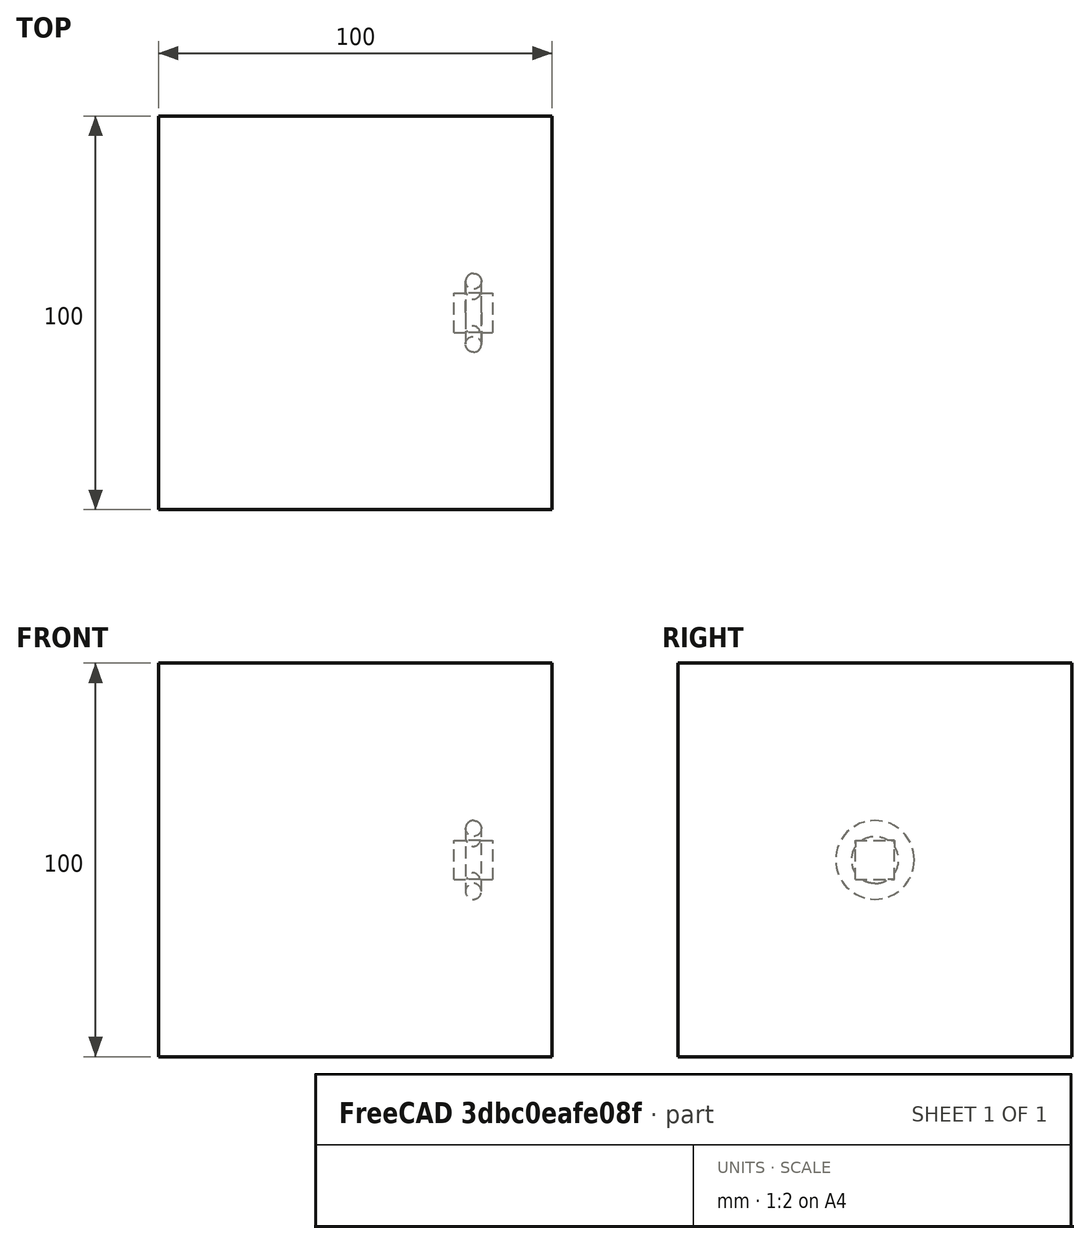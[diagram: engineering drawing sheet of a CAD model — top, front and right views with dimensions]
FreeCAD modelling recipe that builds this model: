
FCSTD DOCUMENT  (FreeCAD 0.21R33694 (Git))
Label: polarArray-7
License: All rights reserved
objects: App::DocumentObjectGroupPython×1251, Part::FeaturePython×4, App::Part×2, Part::MultiFuse×1
note: 4 computed .brp shape members not serialized (recipe doc carries the construction recipe); baked Part::Feature solids carry a one-line shape summary decoded from their .brp

FEATURE [App::DocumentObjectGroupPython] HALFPI  # scripted group (container) (typed FeaturePython)
  name = HALFPI
  value = pi/2.
FEATURE [App::DocumentObjectGroupPython] PI  # scripted group (container) (typed FeaturePython)
  name = PI
  value = 1.*pi
FEATURE [App::DocumentObjectGroupPython] TWOPI  # scripted group (container) (typed FeaturePython)
  name = TWOPI
  value = 2.*pi
FEATURE [App::DocumentObjectGroupPython] Constants  # scripted group (container) (typed FeaturePython)
  Group = -> [HALFPI,PI,TWOPI]
FEATURE [App::DocumentObjectGroupPython] Variables  # scripted group (container) (typed FeaturePython)
FEATURE [App::DocumentObjectGroupPython] Quantities  # scripted group (container) (typed FeaturePython)
FEATURE [App::DocumentObjectGroupPython] Isotopes  # scripted group (container) (typed FeaturePython)
FEATURE [App::DocumentObjectGroupPython] Elements  # scripted group (container) (typed FeaturePython)
FEATURE [App::DocumentObjectGroupPython] Matrix  # scripted group (container) (typed FeaturePython)
FEATURE [App::DocumentObjectGroupPython] Surfaces  # scripted group (container) (typed FeaturePython)
FEATURE [App::DocumentObjectGroupPython] Opticals  # scripted group (container) (typed FeaturePython)
  Group = -> [Matrix,Surfaces]
FEATURE [App::DocumentObjectGroupPython] G4Isotopes  # scripted group (container) (typed FeaturePython)
FEATURE [App::DocumentObjectGroupPython] H_element  # scripted group (container) (typed FeaturePython)
  Z = 1
  atom_value = 1.008
  formula = H
  name = H_element
FEATURE [App::DocumentObjectGroupPython] He_element  # scripted group (container) (typed FeaturePython)
  Z = 2
  atom_value = 4.0026
  formula = He
  name = He_element
FEATURE [App::DocumentObjectGroupPython] Li_element  # scripted group (container) (typed FeaturePython)
  Z = 3
  atom_value = 6.94
  formula = Li
  name = Li_element
FEATURE [App::DocumentObjectGroupPython] Be_element  # scripted group (container) (typed FeaturePython)
  Z = 4
  atom_value = 9.01218
  formula = Be
  name = Be_element
FEATURE [App::DocumentObjectGroupPython] B_element  # scripted group (container) (typed FeaturePython)
  Z = 5
  atom_value = 10.81
  formula = B
  name = B_element
FEATURE [App::DocumentObjectGroupPython] C_element  # scripted group (container) (typed FeaturePython)
  Z = 6
  atom_value = 12.011
  formula = C
  name = C_element
FEATURE [App::DocumentObjectGroupPython] N_element  # scripted group (container) (typed FeaturePython)
  Z = 7
  atom_value = 14.007
  formula = N
  name = N_element
FEATURE [App::DocumentObjectGroupPython] O_element  # scripted group (container) (typed FeaturePython)
  Z = 8
  atom_value = 15.999
  formula = O
  name = O_element
FEATURE [App::DocumentObjectGroupPython] F_element  # scripted group (container) (typed FeaturePython)
  Z = 9
  atom_value = 18.9984
  formula = F
  name = F_element
FEATURE [App::DocumentObjectGroupPython] Ne_element  # scripted group (container) (typed FeaturePython)
  Z = 10
  atom_value = 20.1797
  formula = Ne
  name = Ne_element
FEATURE [App::DocumentObjectGroupPython] Na_element  # scripted group (container) (typed FeaturePython)
  Z = 11
  atom_value = 22.9898
  formula = Na
  name = Na_element
FEATURE [App::DocumentObjectGroupPython] Mg_element  # scripted group (container) (typed FeaturePython)
  Z = 12
  atom_value = 24.305
  formula = Mg
  name = Mg_element
FEATURE [App::DocumentObjectGroupPython] Al_element  # scripted group (container) (typed FeaturePython)
  Z = 13
  atom_value = 26.9815
  formula = Al
  name = Al_element
FEATURE [App::DocumentObjectGroupPython] Si_element  # scripted group (container) (typed FeaturePython)
  Z = 14
  atom_value = 28.085
  formula = Si
  name = Si_element
FEATURE [App::DocumentObjectGroupPython] P_element  # scripted group (container) (typed FeaturePython)
  Z = 15
  atom_value = 30.9738
  formula = P
  name = P_element
FEATURE [App::DocumentObjectGroupPython] S_element  # scripted group (container) (typed FeaturePython)
  Z = 16
  atom_value = 32.06
  formula = S
  name = S_element
FEATURE [App::DocumentObjectGroupPython] Cl_element  # scripted group (container) (typed FeaturePython)
  Z = 17
  atom_value = 35.45
  formula = Cl
  name = Cl_element
FEATURE [App::DocumentObjectGroupPython] Ar_element  # scripted group (container) (typed FeaturePython)
  Z = 18
  atom_value = 39.95
  formula = Ar
  name = Ar_element
FEATURE [App::DocumentObjectGroupPython] K_element  # scripted group (container) (typed FeaturePython)
  Z = 19
  atom_value = 39.0983
  formula = K
  name = K_element
FEATURE [App::DocumentObjectGroupPython] Ca_element  # scripted group (container) (typed FeaturePython)
  Z = 20
  atom_value = 40.078
  formula = Ca
  name = Ca_element
FEATURE [App::DocumentObjectGroupPython] Sc_element  # scripted group (container) (typed FeaturePython)
  Z = 21
  atom_value = 44.9559
  formula = Sc
  name = Sc_element
FEATURE [App::DocumentObjectGroupPython] Ti_element  # scripted group (container) (typed FeaturePython)
  Z = 22
  atom_value = 47.867
  formula = Ti
  name = Ti_element
FEATURE [App::DocumentObjectGroupPython] V_element  # scripted group (container) (typed FeaturePython)
  Z = 23
  atom_value = 50.9415
  formula = V
  name = V_element
FEATURE [App::DocumentObjectGroupPython] Cr_element  # scripted group (container) (typed FeaturePython)
  Z = 24
  atom_value = 51.9961
  formula = Cr
  name = Cr_element
FEATURE [App::DocumentObjectGroupPython] Mn_element  # scripted group (container) (typed FeaturePython)
  Z = 25
  atom_value = 54.938
  formula = Mn
  name = Mn_element
FEATURE [App::DocumentObjectGroupPython] Fe_element  # scripted group (container) (typed FeaturePython)
  Z = 26
  atom_value = 55.845
  formula = Fe
  name = Fe_element
FEATURE [App::DocumentObjectGroupPython] Co_element  # scripted group (container) (typed FeaturePython)
  Z = 27
  atom_value = 58.9332
  formula = Co
  name = Co_element
FEATURE [App::DocumentObjectGroupPython] Ni_element  # scripted group (container) (typed FeaturePython)
  Z = 28
  atom_value = 58.6934
  formula = Ni
  name = Ni_element
FEATURE [App::DocumentObjectGroupPython] Cu_element  # scripted group (container) (typed FeaturePython)
  Z = 29
  atom_value = 63.546
  formula = Cu
  name = Cu_element
FEATURE [App::DocumentObjectGroupPython] Zn_element  # scripted group (container) (typed FeaturePython)
  Z = 30
  atom_value = 65.38
  formula = Zn
  name = Zn_element
FEATURE [App::DocumentObjectGroupPython] Ga_element  # scripted group (container) (typed FeaturePython)
  Z = 31
  atom_value = 69.723
  formula = Ga
  name = Ga_element
FEATURE [App::DocumentObjectGroupPython] Ge_element  # scripted group (container) (typed FeaturePython)
  Z = 32
  atom_value = 72.63
  formula = Ge
  name = Ge_element
FEATURE [App::DocumentObjectGroupPython] As_element  # scripted group (container) (typed FeaturePython)
  Z = 33
  atom_value = 74.9216
  formula = As
  name = As_element
FEATURE [App::DocumentObjectGroupPython] Se_element  # scripted group (container) (typed FeaturePython)
  Z = 34
  atom_value = 78.971
  formula = Se
  name = Se_element
FEATURE [App::DocumentObjectGroupPython] Br_element  # scripted group (container) (typed FeaturePython)
  Z = 35
  atom_value = 79.904
  formula = Br
  name = Br_element
FEATURE [App::DocumentObjectGroupPython] Kr_element  # scripted group (container) (typed FeaturePython)
  Z = 36
  atom_value = 83.798
  formula = Kr
  name = Kr_element
FEATURE [App::DocumentObjectGroupPython] Rb_element  # scripted group (container) (typed FeaturePython)
  Z = 37
  atom_value = 85.4678
  formula = Rb
  name = Rb_element
FEATURE [App::DocumentObjectGroupPython] Sr_element  # scripted group (container) (typed FeaturePython)
  Z = 38
  atom_value = 87.62
  formula = Sr
  name = Sr_element
FEATURE [App::DocumentObjectGroupPython] Y_element  # scripted group (container) (typed FeaturePython)
  Z = 39
  atom_value = 88.9058
  formula = Y
  name = Y_element
FEATURE [App::DocumentObjectGroupPython] Zr_element  # scripted group (container) (typed FeaturePython)
  Z = 40
  atom_value = 91.224
  formula = Zr
  name = Zr_element
FEATURE [App::DocumentObjectGroupPython] Nb_element  # scripted group (container) (typed FeaturePython)
  Z = 41
  atom_value = 92.9064
  formula = Nb
  name = Nb_element
FEATURE [App::DocumentObjectGroupPython] Mo_element  # scripted group (container) (typed FeaturePython)
  Z = 42
  atom_value = 95.95
  formula = Mo
  name = Mo_element
FEATURE [App::DocumentObjectGroupPython] Tc_element  # scripted group (container) (typed FeaturePython)
  Z = 43
  atom_value = 97
  formula = Tc
  name = Tc_element
FEATURE [App::DocumentObjectGroupPython] Ru_element  # scripted group (container) (typed FeaturePython)
  Z = 44
  atom_value = 101.07
  formula = Ru
  name = Ru_element
FEATURE [App::DocumentObjectGroupPython] Rh_element  # scripted group (container) (typed FeaturePython)
  Z = 45
  atom_value = 102.905
  formula = Rh
  name = Rh_element
FEATURE [App::DocumentObjectGroupPython] Pd_element  # scripted group (container) (typed FeaturePython)
  Z = 46
  atom_value = 106.42
  formula = Pd
  name = Pd_element
FEATURE [App::DocumentObjectGroupPython] Ag_element  # scripted group (container) (typed FeaturePython)
  Z = 47
  atom_value = 107.868
  formula = Ag
  name = Ag_element
FEATURE [App::DocumentObjectGroupPython] Cd_element  # scripted group (container) (typed FeaturePython)
  Z = 48
  atom_value = 112.414
  formula = Cd
  name = Cd_element
FEATURE [App::DocumentObjectGroupPython] In_element  # scripted group (container) (typed FeaturePython)
  Z = 49
  atom_value = 114.818
  formula = In
  name = In_element
FEATURE [App::DocumentObjectGroupPython] Sn_element  # scripted group (container) (typed FeaturePython)
  Z = 50
  atom_value = 118.71
  formula = Sn
  name = Sn_element
FEATURE [App::DocumentObjectGroupPython] Sb_element  # scripted group (container) (typed FeaturePython)
  Z = 51
  atom_value = 121.76
  formula = Sb
  name = Sb_element
FEATURE [App::DocumentObjectGroupPython] Te_element  # scripted group (container) (typed FeaturePython)
  Z = 52
  atom_value = 127.6
  formula = Te
  name = Te_element
FEATURE [App::DocumentObjectGroupPython] I_element  # scripted group (container) (typed FeaturePython)
  Z = 53
  atom_value = 126.904
  formula = I
  name = I_element
FEATURE [App::DocumentObjectGroupPython] Xe_element  # scripted group (container) (typed FeaturePython)
  Z = 54
  atom_value = 131.293
  formula = Xe
  name = Xe_element
FEATURE [App::DocumentObjectGroupPython] Cs_element  # scripted group (container) (typed FeaturePython)
  Z = 55
  atom_value = 132.905
  formula = Cs
  name = Cs_element
FEATURE [App::DocumentObjectGroupPython] Ba_element  # scripted group (container) (typed FeaturePython)
  Z = 56
  atom_value = 137.327
  formula = Ba
  name = Ba_element
FEATURE [App::DocumentObjectGroupPython] La_element  # scripted group (container) (typed FeaturePython)
  Z = 57
  atom_value = 138.905
  formula = La
  name = La_element
FEATURE [App::DocumentObjectGroupPython] Ce_element  # scripted group (container) (typed FeaturePython)
  Z = 58
  atom_value = 140.116
  formula = Ce
  name = Ce_element
FEATURE [App::DocumentObjectGroupPython] Pr_element  # scripted group (container) (typed FeaturePython)
  Z = 59
  atom_value = 140.908
  formula = Pr
  name = Pr_element
FEATURE [App::DocumentObjectGroupPython] Nd_element  # scripted group (container) (typed FeaturePython)
  Z = 60
  atom_value = 144.242
  formula = Nd
  name = Nd_element
FEATURE [App::DocumentObjectGroupPython] Pm_element  # scripted group (container) (typed FeaturePython)
  Z = 61
  atom_value = 145
  formula = Pm
  name = Pm_element
FEATURE [App::DocumentObjectGroupPython] Sm_element  # scripted group (container) (typed FeaturePython)
  Z = 62
  atom_value = 150.36
  formula = Sm
  name = Sm_element
FEATURE [App::DocumentObjectGroupPython] Eu_element  # scripted group (container) (typed FeaturePython)
  Z = 63
  atom_value = 151.964
  formula = Eu
  name = Eu_element
FEATURE [App::DocumentObjectGroupPython] Gd_element  # scripted group (container) (typed FeaturePython)
  Z = 64
  atom_value = 157.25
  formula = Gd
  name = Gd_element
FEATURE [App::DocumentObjectGroupPython] Tb_element  # scripted group (container) (typed FeaturePython)
  Z = 65
  atom_value = 158.925
  formula = Tb
  name = Tb_element
FEATURE [App::DocumentObjectGroupPython] Dy_element  # scripted group (container) (typed FeaturePython)
  Z = 66
  atom_value = 162.5
  formula = Dy
  name = Dy_element
FEATURE [App::DocumentObjectGroupPython] Ho_element  # scripted group (container) (typed FeaturePython)
  Z = 67
  atom_value = 164.93
  formula = Ho
  name = Ho_element
FEATURE [App::DocumentObjectGroupPython] Er_element  # scripted group (container) (typed FeaturePython)
  Z = 68
  atom_value = 167.259
  formula = Er
  name = Er_element
FEATURE [App::DocumentObjectGroupPython] Tm_element  # scripted group (container) (typed FeaturePython)
  Z = 69
  atom_value = 168.934
  formula = Tm
  name = Tm_element
FEATURE [App::DocumentObjectGroupPython] Yb_element  # scripted group (container) (typed FeaturePython)
  Z = 70
  atom_value = 173.045
  formula = Yb
  name = Yb_element
FEATURE [App::DocumentObjectGroupPython] Lu_element  # scripted group (container) (typed FeaturePython)
  Z = 71
  atom_value = 174.967
  formula = Lu
  name = Lu_element
FEATURE [App::DocumentObjectGroupPython] Hf_element  # scripted group (container) (typed FeaturePython)
  Z = 72
  atom_value = 178.49
  formula = Hf
  name = Hf_element
FEATURE [App::DocumentObjectGroupPython] Ta_element  # scripted group (container) (typed FeaturePython)
  Z = 73
  atom_value = 180.948
  formula = Ta
  name = Ta_element
FEATURE [App::DocumentObjectGroupPython] W_element  # scripted group (container) (typed FeaturePython)
  Z = 74
  atom_value = 183.84
  formula = W
  name = W_element
FEATURE [App::DocumentObjectGroupPython] Re_element  # scripted group (container) (typed FeaturePython)
  Z = 75
  atom_value = 186.207
  formula = Re
  name = Re_element
FEATURE [App::DocumentObjectGroupPython] Os_element  # scripted group (container) (typed FeaturePython)
  Z = 76
  atom_value = 190.23
  formula = Os
  name = Os_element
FEATURE [App::DocumentObjectGroupPython] Ir_element  # scripted group (container) (typed FeaturePython)
  Z = 77
  atom_value = 192.217
  formula = Ir
  name = Ir_element
FEATURE [App::DocumentObjectGroupPython] Pt_element  # scripted group (container) (typed FeaturePython)
  Z = 78
  atom_value = 195.084
  formula = Pt
  name = Pt_element
FEATURE [App::DocumentObjectGroupPython] Au_element  # scripted group (container) (typed FeaturePython)
  Z = 79
  atom_value = 196.967
  formula = Au
  name = Au_element
FEATURE [App::DocumentObjectGroupPython] Hg_element  # scripted group (container) (typed FeaturePython)
  Z = 80
  atom_value = 200.592
  formula = Hg
  name = Hg_element
FEATURE [App::DocumentObjectGroupPython] Tl_element  # scripted group (container) (typed FeaturePython)
  Z = 81
  atom_value = 204.38
  formula = Tl
  name = Tl_element
FEATURE [App::DocumentObjectGroupPython] Pb_element  # scripted group (container) (typed FeaturePython)
  Z = 82
  atom_value = 207.2
  formula = Pb
  name = Pb_element
FEATURE [App::DocumentObjectGroupPython] Bi_element  # scripted group (container) (typed FeaturePython)
  Z = 83
  atom_value = 208.98
  formula = Bi
  name = Bi_element
FEATURE [App::DocumentObjectGroupPython] Po_element  # scripted group (container) (typed FeaturePython)
  Z = 84
  atom_value = 209
  formula = Po
  name = Po_element
FEATURE [App::DocumentObjectGroupPython] At_element  # scripted group (container) (typed FeaturePython)
  Z = 85
  atom_value = 210
  formula = At
  name = At_element
FEATURE [App::DocumentObjectGroupPython] Rn_element  # scripted group (container) (typed FeaturePython)
  Z = 86
  atom_value = 222
  formula = Rn
  name = Rn_element
FEATURE [App::DocumentObjectGroupPython] Fr_element  # scripted group (container) (typed FeaturePython)
  Z = 87
  atom_value = 223
  formula = Fr
  name = Fr_element
FEATURE [App::DocumentObjectGroupPython] Ra_element  # scripted group (container) (typed FeaturePython)
  Z = 88
  atom_value = 226
  formula = Ra
  name = Ra_element
FEATURE [App::DocumentObjectGroupPython] Ac_element  # scripted group (container) (typed FeaturePython)
  Z = 89
  atom_value = 227
  formula = Ac
  name = Ac_element
FEATURE [App::DocumentObjectGroupPython] Th_element  # scripted group (container) (typed FeaturePython)
  Z = 90
  atom_value = 232.038
  formula = Th
  name = Th_element
FEATURE [App::DocumentObjectGroupPython] Pa_element  # scripted group (container) (typed FeaturePython)
  Z = 91
  atom_value = 231.036
  formula = Pa
  name = Pa_element
FEATURE [App::DocumentObjectGroupPython] U_element  # scripted group (container) (typed FeaturePython)
  Z = 92
  atom_value = 238.029
  formula = U
  name = U_element
FEATURE [App::DocumentObjectGroupPython] Np_element  # scripted group (container) (typed FeaturePython)
  Z = 93
  atom_value = 237
  formula = Np
  name = Np_element
FEATURE [App::DocumentObjectGroupPython] Pu_element  # scripted group (container) (typed FeaturePython)
  Z = 94
  atom_value = 244
  formula = Pu
  name = Pu_element
FEATURE [App::DocumentObjectGroupPython] Am_element  # scripted group (container) (typed FeaturePython)
  Z = 95
  atom_value = 243
  formula = Am
  name = Am_element
FEATURE [App::DocumentObjectGroupPython] Cm_element  # scripted group (container) (typed FeaturePython)
  Z = 96
  atom_value = 247
  formula = Cm
  name = Cm_element
FEATURE [App::DocumentObjectGroupPython] Bk_element  # scripted group (container) (typed FeaturePython)
  Z = 97
  atom_value = 247
  formula = Bk
  name = Bk_element
FEATURE [App::DocumentObjectGroupPython] Cf_element  # scripted group (container) (typed FeaturePython)
  Z = 98
  atom_value = 251
  formula = Cf
  name = Cf_element
FEATURE [App::DocumentObjectGroupPython] G4Elements  # scripted group (container) (typed FeaturePython)
  Group = -> [H_element,He_element,Li_element,Be_element,B_element,C_element,N_element,O_element,F_element,Ne_element,Na_element,Mg_element,Al_element,Si_element,P_element,S_element,Cl_element,Ar_element,K_element,Ca_element,Sc_element,Ti_element,V_element,Cr_element,Mn_element,Fe_element,Co_element,Ni_element,Cu_element,Zn_element,Ga_element,Ge_element,As_element,Se_element,Br_element,Kr_element,Rb_element,+61 more]
FEATURE [App::DocumentObjectGroupPython] H_element001  label="H_element : 0.101"  # scripted group (container) (typed FeaturePython)
  n = 0.101327
FEATURE [App::DocumentObjectGroupPython] C_element001  label="C_element : 0.775"  # scripted group (container) (typed FeaturePython)
  n = 0.7755
FEATURE [App::DocumentObjectGroupPython] N_element001  label="N_element : 0.035"  # scripted group (container) (typed FeaturePython)
  n = 0.035057
FEATURE [App::DocumentObjectGroupPython] O_element001  label="O_element : 0.052"  # scripted group (container) (typed FeaturePython)
  n = 0.0523159
FEATURE [App::DocumentObjectGroupPython] F_element001  label="F_element : 0.017"  # scripted group (container) (typed FeaturePython)
  n = 0.017422
FEATURE [App::DocumentObjectGroupPython] Ca_element001  label="Ca_element : 0.018"  # scripted group (container) (typed FeaturePython)
  n = 0.018378
FEATURE [App::DocumentObjectGroupPython] G4_A_150_TISSUE  label="G4_A-150_TISSUE"  # scripted group (container) (typed FeaturePython)
  Dunit = g/cm3
  Dvalue = 1.127
  Group = -> [H_element001,C_element001,N_element001,O_element001,F_element001,Ca_element001]
  conduct = 2
  density = 1
  expand = 3
  formula = G4_A-150_TISSUE
  name = G4_A-150_TISSUE
  specific = 4
FEATURE [App::DocumentObjectGroupPython] C_element002  label="C_element : 3"  # scripted group (container) (typed FeaturePython)
  n = 3
  ref = C_element
FEATURE [App::DocumentObjectGroupPython] H_element002  label="H_element : 6"  # scripted group (container) (typed FeaturePython)
  n = 6
  ref = H_element
FEATURE [App::DocumentObjectGroupPython] O_element002  label="O_element : 1"  # scripted group (container) (typed FeaturePython)
  n = 1
  ref = O_element
FEATURE [App::DocumentObjectGroupPython] G4_ACETONE  # scripted group (container) (typed FeaturePython)
  Dunit = g/cm3
  Dvalue = 0.7899
  Group = -> [C_element002,H_element002,O_element002]
  conduct = 2
  density = 1
  expand = 3
  formula = G4_ACETONE
  name = G4_ACETONE
  specific = 4
FEATURE [App::DocumentObjectGroupPython] C_element003  label="C_element : 2"  # scripted group (container) (typed FeaturePython)
  n = 2
  ref = C_element
FEATURE [App::DocumentObjectGroupPython] H_element003  label="H_element : 2"  # scripted group (container) (typed FeaturePython)
  n = 2
  ref = H_element
FEATURE [App::DocumentObjectGroupPython] G4_ACETYLENE  # scripted group (container) (typed FeaturePython)
  Dunit = g/cm3
  Dvalue = 0.0010967
  Group = -> [C_element003,H_element003]
  conduct = 2
  density = 1
  expand = 3
  formula = G4_ACETYLENE
  name = G4_ACETYLENE
  specific = 4
FEATURE [App::DocumentObjectGroupPython] C_element004  label="C_element : 5"  # scripted group (container) (typed FeaturePython)
  n = 5
  ref = C_element
FEATURE [App::DocumentObjectGroupPython] H_element004  label="H_element : 5"  # scripted group (container) (typed FeaturePython)
  n = 5
  ref = H_element
FEATURE [App::DocumentObjectGroupPython] N_element002  label="N_element : 5"  # scripted group (container) (typed FeaturePython)
  n = 5
  ref = N_element
FEATURE [App::DocumentObjectGroupPython] G4_ADENINE  # scripted group (container) (typed FeaturePython)
  Dunit = g/cm3
  Dvalue = 1.6
  Group = -> [C_element004,H_element004,N_element002]
  conduct = 2
  density = 1
  expand = 3
  formula = G4_ADENINE
  name = G4_ADENINE
  specific = 4
FEATURE [App::DocumentObjectGroupPython] H_element005  label="H_element : 0.114"  # scripted group (container) (typed FeaturePython)
  n = 0.114
FEATURE [App::DocumentObjectGroupPython] C_element005  label="C_element : 0.598"  # scripted group (container) (typed FeaturePython)
  n = 0.598
FEATURE [App::DocumentObjectGroupPython] N_element003  label="N_element : 0.007"  # scripted group (container) (typed FeaturePython)
  n = 0.007
FEATURE [App::DocumentObjectGroupPython] O_element003  label="O_element : 0.278"  # scripted group (container) (typed FeaturePython)
  n = 0.278
FEATURE [App::DocumentObjectGroupPython] Na_element001  label="Na_element : 0.001"  # scripted group (container) (typed FeaturePython)
  n = 0.001
FEATURE [App::DocumentObjectGroupPython] S_element001  label="S_element : 0.001"  # scripted group (container) (typed FeaturePython)
  n = 0.001
FEATURE [App::DocumentObjectGroupPython] Cl_element001  label="Cl_element : 0.001"  # scripted group (container) (typed FeaturePython)
  n = 0.001
FEATURE [App::DocumentObjectGroupPython] G4_ADIPOSE_TISSUE_ICRP  # scripted group (container) (typed FeaturePython)
  Dunit = g/cm3
  Dvalue = 0.95
  Group = -> [H_element005,C_element005,N_element003,O_element003,Na_element001,S_element001,Cl_element001]
  conduct = 2
  density = 1
  expand = 3
  formula = G4_ADIPOSE_TISSUE_ICRP
  name = G4_ADIPOSE_TISSUE_ICRP
  specific = 4
FEATURE [App::DocumentObjectGroupPython] C_element006  label="C_element : 0.000"  # scripted group (container) (typed FeaturePython)
  n = 0.000124
FEATURE [App::DocumentObjectGroupPython] N_element004  label="N_element : 0.755"  # scripted group (container) (typed FeaturePython)
  n = 0.755268
FEATURE [App::DocumentObjectGroupPython] O_element004  label="O_element : 0.232"  # scripted group (container) (typed FeaturePython)
  n = 0.231781
FEATURE [App::DocumentObjectGroupPython] Ar_element001  label="Ar_element : 0.013"  # scripted group (container) (typed FeaturePython)
  n = 0.012827
FEATURE [App::DocumentObjectGroupPython] G4_AIR  # scripted group (container) (typed FeaturePython)
  Dunit = g/cm3
  Dvalue = 0.00120479
  Group = -> [C_element006,N_element004,O_element004,Ar_element001]
  conduct = 2
  density = 1
  expand = 3
  formula = G4_AIR
  name = G4_AIR
  specific = 4
FEATURE [App::DocumentObjectGroupPython] C_element007  label="C_element : 006"  # scripted group (container) (typed FeaturePython)
  n = 3
  ref = C_element
FEATURE [App::DocumentObjectGroupPython] H_element006  label="H_element : 7"  # scripted group (container) (typed FeaturePython)
  n = 7
  ref = H_element
FEATURE [App::DocumentObjectGroupPython] N_element005  label="N_element : 1"  # scripted group (container) (typed FeaturePython)
  n = 1
  ref = N_element
FEATURE [App::DocumentObjectGroupPython] O_element005  label="O_element : 2"  # scripted group (container) (typed FeaturePython)
  n = 2
  ref = O_element
FEATURE [App::DocumentObjectGroupPython] G4_ALANINE  # scripted group (container) (typed FeaturePython)
  Dunit = g/cm3
  Dvalue = 1.42
  Group = -> [C_element007,H_element006,N_element005,O_element005]
  conduct = 2
  density = 1
  expand = 3
  formula = G4_ALANINE
  name = G4_ALANINE
  specific = 4
FEATURE [App::DocumentObjectGroupPython] Al_element001  label="Al_element : 2"  # scripted group (container) (typed FeaturePython)
  n = 2
  ref = Al_element
FEATURE [App::DocumentObjectGroupPython] O_element006  label="O_element : 3"  # scripted group (container) (typed FeaturePython)
  n = 3
  ref = O_element
FEATURE [App::DocumentObjectGroupPython] G4_ALUMINUM_OXIDE  # scripted group (container) (typed FeaturePython)
  Dunit = g/cm3
  Dvalue = 3.97
  Group = -> [Al_element001,O_element006]
  conduct = 2
  density = 1
  expand = 3
  formula = G4_ALUMINUM_OXIDE
  name = G4_ALUMINUM_OXIDE
  specific = 4
FEATURE [App::DocumentObjectGroupPython] H_element007  label="H_element : 0.106"  # scripted group (container) (typed FeaturePython)
  n = 0.10593
FEATURE [App::DocumentObjectGroupPython] C_element008  label="C_element : 0.789"  # scripted group (container) (typed FeaturePython)
  n = 0.788974
FEATURE [App::DocumentObjectGroupPython] O_element007  label="O_element : 0.105"  # scripted group (container) (typed FeaturePython)
  n = 0.105096
FEATURE [App::DocumentObjectGroupPython] G4_AMBER  # scripted group (container) (typed FeaturePython)
  Dunit = g/cm3
  Dvalue = 1.1
  Group = -> [H_element007,C_element008,O_element007]
  conduct = 2
  density = 1
  expand = 3
  formula = G4_AMBER
  name = G4_AMBER
  specific = 4
FEATURE [App::DocumentObjectGroupPython] N_element006  label="N_element : 006"  # scripted group (container) (typed FeaturePython)
  n = 1
  ref = N_element
FEATURE [App::DocumentObjectGroupPython] H_element008  label="H_element : 3"  # scripted group (container) (typed FeaturePython)
  n = 3
  ref = H_element
FEATURE [App::DocumentObjectGroupPython] G4_AMMONIA  # scripted group (container) (typed FeaturePython)
  Dunit = g/cm3
  Dvalue = 0.000826019
  Group = -> [N_element006,H_element008]
  conduct = 2
  density = 1
  expand = 3
  formula = G4_AMMONIA
  name = G4_AMMONIA
  specific = 4
FEATURE [App::DocumentObjectGroupPython] C_element009  label="C_element : 6"  # scripted group (container) (typed FeaturePython)
  n = 6
  ref = C_element
FEATURE [App::DocumentObjectGroupPython] H_element009  label="H_element : 008"  # scripted group (container) (typed FeaturePython)
  n = 7
  ref = H_element
FEATURE [App::DocumentObjectGroupPython] N_element007  label="N_element : 007"  # scripted group (container) (typed FeaturePython)
  n = 1
  ref = N_element
FEATURE [App::DocumentObjectGroupPython] G4_ANILINE  # scripted group (container) (typed FeaturePython)
  Dunit = g/cm3
  Dvalue = 1.0235
  Group = -> [C_element009,H_element009,N_element007]
  conduct = 2
  density = 1
  expand = 3
  formula = G4_ANILINE
  name = G4_ANILINE
  specific = 4
FEATURE [App::DocumentObjectGroupPython] C_element010  label="C_element : 14"  # scripted group (container) (typed FeaturePython)
  n = 14
  ref = C_element
FEATURE [App::DocumentObjectGroupPython] H_element010  label="H_element : 10"  # scripted group (container) (typed FeaturePython)
  n = 10
  ref = H_element
FEATURE [App::DocumentObjectGroupPython] G4_ANTHRACENE  # scripted group (container) (typed FeaturePython)
  Dunit = g/cm3
  Dvalue = 1.283
  Group = -> [C_element010,H_element010]
  conduct = 2
  density = 1
  expand = 3
  formula = G4_ANTHRACENE
  name = G4_ANTHRACENE
  specific = 4
FEATURE [App::DocumentObjectGroupPython] H_element011  label="H_element : 0.065"  # scripted group (container) (typed FeaturePython)
  n = 0.0654709
FEATURE [App::DocumentObjectGroupPython] C_element011  label="C_element : 0.537"  # scripted group (container) (typed FeaturePython)
  n = 0.536944
FEATURE [App::DocumentObjectGroupPython] N_element008  label="N_element : 0.021"  # scripted group (container) (typed FeaturePython)
  n = 0.0215
FEATURE [App::DocumentObjectGroupPython] O_element008  label="O_element : 0.032"  # scripted group (container) (typed FeaturePython)
  n = 0.032085
FEATURE [App::DocumentObjectGroupPython] F_element002  label="F_element : 0.167"  # scripted group (container) (typed FeaturePython)
  n = 0.167411
FEATURE [App::DocumentObjectGroupPython] Ca_element002  label="Ca_element : 0.177"  # scripted group (container) (typed FeaturePython)
  n = 0.176589
FEATURE [App::DocumentObjectGroupPython] G4_B_100_BONE  label="G4_B-100_BONE"  # scripted group (container) (typed FeaturePython)
  Dunit = g/cm3
  Dvalue = 1.45
  Group = -> [H_element011,C_element011,N_element008,O_element008,F_element002,Ca_element002]
  conduct = 2
  density = 1
  expand = 3
  formula = G4_B-100_BONE
  name = G4_B-100_BONE
  specific = 4
FEATURE [App::DocumentObjectGroupPython] H_element012  label="H_element : 0.057"  # scripted group (container) (typed FeaturePython)
  n = 0.057441
FEATURE [App::DocumentObjectGroupPython] C_element012  label="C_element : 0.790"  # scripted group (container) (typed FeaturePython)
  n = 0.774591
FEATURE [App::DocumentObjectGroupPython] O_element009  label="O_element : 0.168"  # scripted group (container) (typed FeaturePython)
  n = 0.167968
FEATURE [App::DocumentObjectGroupPython] G4_BAKELITE  # scripted group (container) (typed FeaturePython)
  Dunit = g/cm3
  Dvalue = 1.25
  Group = -> [H_element012,C_element012,O_element009]
  conduct = 2
  density = 1
  expand = 3
  formula = G4_BAKELITE
  name = G4_BAKELITE
  specific = 4
FEATURE [App::DocumentObjectGroupPython] Ba_element001  label="Ba_element : 1"  # scripted group (container) (typed FeaturePython)
  n = 1
  ref = Ba_element
FEATURE [App::DocumentObjectGroupPython] F_element003  label="F_element : 2"  # scripted group (container) (typed FeaturePython)
  n = 2
  ref = F_element
FEATURE [App::DocumentObjectGroupPython] G4_BARIUM_FLUORIDE  # scripted group (container) (typed FeaturePython)
  Dunit = g/cm3
  Dvalue = 4.89
  Group = -> [Ba_element001,F_element003]
  conduct = 2
  density = 1
  expand = 3
  formula = G4_BARIUM_FLUORIDE
  name = G4_BARIUM_FLUORIDE
  specific = 4
FEATURE [App::DocumentObjectGroupPython] Ba_element002  label="Ba_element : 002"  # scripted group (container) (typed FeaturePython)
  n = 1
  ref = Ba_element
FEATURE [App::DocumentObjectGroupPython] S_element002  label="S_element : 1"  # scripted group (container) (typed FeaturePython)
  n = 1
  ref = S_element
FEATURE [App::DocumentObjectGroupPython] O_element010  label="O_element : 4"  # scripted group (container) (typed FeaturePython)
  n = 4
  ref = O_element
FEATURE [App::DocumentObjectGroupPython] G4_BARIUM_SULFATE  # scripted group (container) (typed FeaturePython)
  Dunit = g/cm3
  Dvalue = 4.5
  Group = -> [Ba_element002,S_element002,O_element010]
  conduct = 2
  density = 1
  expand = 3
  formula = G4_BARIUM_SULFATE
  name = G4_BARIUM_SULFATE
  specific = 4
FEATURE [App::DocumentObjectGroupPython] C_element013  label="C_element : 007"  # scripted group (container) (typed FeaturePython)
  n = 6
  ref = C_element
FEATURE [App::DocumentObjectGroupPython] H_element013  label="H_element : 009"  # scripted group (container) (typed FeaturePython)
  n = 6
  ref = H_element
FEATURE [App::DocumentObjectGroupPython] G4_BENZENE  # scripted group (container) (typed FeaturePython)
  Dunit = g/cm3
  Dvalue = 0.87865
  Group = -> [C_element013,H_element013]
  conduct = 2
  density = 1
  expand = 3
  formula = G4_BENZENE
  name = G4_BENZENE
  specific = 4
FEATURE [App::DocumentObjectGroupPython] Be_element001  label="Be_element : 1"  # scripted group (container) (typed FeaturePython)
  n = 1
  ref = Be_element
FEATURE [App::DocumentObjectGroupPython] O_element011  label="O_element : 005"  # scripted group (container) (typed FeaturePython)
  n = 1
  ref = O_element
FEATURE [App::DocumentObjectGroupPython] G4_BERYLLIUM_OXIDE  # scripted group (container) (typed FeaturePython)
  Dunit = g/cm3
  Dvalue = 3.01
  Group = -> [Be_element001,O_element011]
  conduct = 2
  density = 1
  expand = 3
  formula = G4_BERYLLIUM_OXIDE
  name = G4_BERYLLIUM_OXIDE
  specific = 4
FEATURE [App::DocumentObjectGroupPython] Bi_element001  label="Bi_element : 4"  # scripted group (container) (typed FeaturePython)
  n = 4
  ref = Bi_element
FEATURE [App::DocumentObjectGroupPython] Ge_element001  label="Ge_element : 3"  # scripted group (container) (typed FeaturePython)
  n = 3
  ref = Ge_element
FEATURE [App::DocumentObjectGroupPython] O_element012  label="O_element : 12"  # scripted group (container) (typed FeaturePython)
  n = 12
  ref = O_element
FEATURE [App::DocumentObjectGroupPython] G4_BGO  # scripted group (container) (typed FeaturePython)
  Dunit = g/cm3
  Dvalue = 7.13
  Group = -> [Bi_element001,Ge_element001,O_element012]
  conduct = 2
  density = 1
  expand = 3
  formula = G4_BGO
  name = G4_BGO
  specific = 4
FEATURE [App::DocumentObjectGroupPython] H_element014  label="H_element : 0.102"  # scripted group (container) (typed FeaturePython)
  n = 0.102
FEATURE [App::DocumentObjectGroupPython] C_element014  label="C_element : 0.110"  # scripted group (container) (typed FeaturePython)
  n = 0.11
FEATURE [App::DocumentObjectGroupPython] N_element009  label="N_element : 0.033"  # scripted group (container) (typed FeaturePython)
  n = 0.033
FEATURE [App::DocumentObjectGroupPython] O_element013  label="O_element : 0.745"  # scripted group (container) (typed FeaturePython)
  n = 0.745
FEATURE [App::DocumentObjectGroupPython] Na_element002  label="Na_element : 0.002"  # scripted group (container) (typed FeaturePython)
  n = 0.001
FEATURE [App::DocumentObjectGroupPython] P_element001  label="P_element : 0.001"  # scripted group (container) (typed FeaturePython)
  n = 0.001
FEATURE [App::DocumentObjectGroupPython] S_element003  label="S_element : 0.002"  # scripted group (container) (typed FeaturePython)
  n = 0.002
FEATURE [App::DocumentObjectGroupPython] Cl_element002  label="Cl_element : 0.003"  # scripted group (container) (typed FeaturePython)
  n = 0.003
FEATURE [App::DocumentObjectGroupPython] K_element001  label="K_element : 0.002"  # scripted group (container) (typed FeaturePython)
  n = 0.002
FEATURE [App::DocumentObjectGroupPython] Fe_element001  label="Fe_element : 0.001"  # scripted group (container) (typed FeaturePython)
  n = 0.001
FEATURE [App::DocumentObjectGroupPython] G4_BLOOD_ICRP  # scripted group (container) (typed FeaturePython)
  Dunit = g/cm3
  Dvalue = 1.06
  Group = -> [H_element014,C_element014,N_element009,O_element013,Na_element002,P_element001,S_element003,Cl_element002,K_element001,Fe_element001]
  conduct = 2
  density = 1
  expand = 3
  formula = G4_BLOOD_ICRP
  name = G4_BLOOD_ICRP
  specific = 4
FEATURE [App::DocumentObjectGroupPython] H_element015  label="H_element : 0.064"  # scripted group (container) (typed FeaturePython)
  n = 0.064
FEATURE [App::DocumentObjectGroupPython] C_element015  label="C_element : 0.278"  # scripted group (container) (typed FeaturePython)
  n = 0.278
FEATURE [App::DocumentObjectGroupPython] N_element010  label="N_element : 0.027"  # scripted group (container) (typed FeaturePython)
  n = 0.027
FEATURE [App::DocumentObjectGroupPython] O_element014  label="O_element : 0.410"  # scripted group (container) (typed FeaturePython)
  n = 0.41
FEATURE [App::DocumentObjectGroupPython] Mg_element001  label="Mg_element : 0.002"  # scripted group (container) (typed FeaturePython)
  n = 0.002
FEATURE [App::DocumentObjectGroupPython] P_element002  label="P_element : 0.070"  # scripted group (container) (typed FeaturePython)
  n = 0.07
FEATURE [App::DocumentObjectGroupPython] S_element004  label="S_element : 0.003"  # scripted group (container) (typed FeaturePython)
  n = 0.002
FEATURE [App::DocumentObjectGroupPython] Ca_element003  label="Ca_element : 0.147"  # scripted group (container) (typed FeaturePython)
  n = 0.147
FEATURE [App::DocumentObjectGroupPython] G4_BONE_COMPACT_ICRU  # scripted group (container) (typed FeaturePython)
  Dunit = g/cm3
  Dvalue = 1.85
  Group = -> [H_element015,C_element015,N_element010,O_element014,Mg_element001,P_element002,S_element004,Ca_element003]
  conduct = 2
  density = 1
  expand = 3
  formula = G4_BONE_COMPACT_ICRU
  name = G4_BONE_COMPACT_ICRU
  specific = 4
FEATURE [App::DocumentObjectGroupPython] H_element016  label="H_element : 0.034"  # scripted group (container) (typed FeaturePython)
  n = 0.034
FEATURE [App::DocumentObjectGroupPython] C_element016  label="C_element : 0.155"  # scripted group (container) (typed FeaturePython)
  n = 0.155
FEATURE [App::DocumentObjectGroupPython] N_element011  label="N_element : 0.042"  # scripted group (container) (typed FeaturePython)
  n = 0.042
FEATURE [App::DocumentObjectGroupPython] O_element015  label="O_element : 0.435"  # scripted group (container) (typed FeaturePython)
  n = 0.435
FEATURE [App::DocumentObjectGroupPython] Na_element003  label="Na_element : 0.003"  # scripted group (container) (typed FeaturePython)
  n = 0.001
FEATURE [App::DocumentObjectGroupPython] Mg_element002  label="Mg_element : 0.003"  # scripted group (container) (typed FeaturePython)
  n = 0.002
FEATURE [App::DocumentObjectGroupPython] P_element003  label="P_element : 0.103"  # scripted group (container) (typed FeaturePython)
  n = 0.103
FEATURE [App::DocumentObjectGroupPython] S_element005  label="S_element : 0.004"  # scripted group (container) (typed FeaturePython)
  n = 0.003
FEATURE [App::DocumentObjectGroupPython] Ca_element004  label="Ca_element : 0.225"  # scripted group (container) (typed FeaturePython)
  n = 0.225
FEATURE [App::DocumentObjectGroupPython] G4_BONE_CORTICAL_ICRP  # scripted group (container) (typed FeaturePython)
  Dunit = g/cm3
  Dvalue = 1.92
  Group = -> [H_element016,C_element016,N_element011,O_element015,Na_element003,Mg_element002,P_element003,S_element005,Ca_element004]
  conduct = 2
  density = 1
  expand = 3
  formula = G4_BONE_CORTICAL_ICRP
  name = G4_BONE_CORTICAL_ICRP
  specific = 4
FEATURE [App::DocumentObjectGroupPython] B_element001  label="B_element : 4"  # scripted group (container) (typed FeaturePython)
  n = 4
  ref = B_element
FEATURE [App::DocumentObjectGroupPython] C_element017  label="C_element : 1"  # scripted group (container) (typed FeaturePython)
  n = 1
  ref = C_element
FEATURE [App::DocumentObjectGroupPython] G4_BORON_CARBIDE  # scripted group (container) (typed FeaturePython)
  Dunit = g/cm3
  Dvalue = 2.52
  Group = -> [B_element001,C_element017]
  conduct = 2
  density = 1
  expand = 3
  formula = G4_BORON_CARBIDE
  name = G4_BORON_CARBIDE
  specific = 4
FEATURE [App::DocumentObjectGroupPython] B_element002  label="B_element : 2"  # scripted group (container) (typed FeaturePython)
  n = 2
  ref = B_element
FEATURE [App::DocumentObjectGroupPython] O_element016  label="O_element : 006"  # scripted group (container) (typed FeaturePython)
  n = 3
  ref = O_element
FEATURE [App::DocumentObjectGroupPython] G4_BORON_OXIDE  # scripted group (container) (typed FeaturePython)
  Dunit = g/cm3
  Dvalue = 1.812
  Group = -> [B_element002,O_element016]
  conduct = 2
  density = 1
  expand = 3
  formula = G4_BORON_OXIDE
  name = G4_BORON_OXIDE
  specific = 4
FEATURE [App::DocumentObjectGroupPython] H_element017  label="H_element : 0.107"  # scripted group (container) (typed FeaturePython)
  n = 0.107
FEATURE [App::DocumentObjectGroupPython] C_element018  label="C_element : 0.145"  # scripted group (container) (typed FeaturePython)
  n = 0.145
FEATURE [App::DocumentObjectGroupPython] N_element012  label="N_element : 0.022"  # scripted group (container) (typed FeaturePython)
  n = 0.022
FEATURE [App::DocumentObjectGroupPython] O_element017  label="O_element : 0.712"  # scripted group (container) (typed FeaturePython)
  n = 0.712
FEATURE [App::DocumentObjectGroupPython] Na_element004  label="Na_element : 0.004"  # scripted group (container) (typed FeaturePython)
  n = 0.002
FEATURE [App::DocumentObjectGroupPython] P_element004  label="P_element : 0.004"  # scripted group (container) (typed FeaturePython)
  n = 0.004
FEATURE [App::DocumentObjectGroupPython] S_element006  label="S_element : 0.005"  # scripted group (container) (typed FeaturePython)
  n = 0.002
FEATURE [App::DocumentObjectGroupPython] Cl_element003  label="Cl_element : 0.004"  # scripted group (container) (typed FeaturePython)
  n = 0.003
FEATURE [App::DocumentObjectGroupPython] K_element002  label="K_element : 0.003"  # scripted group (container) (typed FeaturePython)
  n = 0.003
FEATURE [App::DocumentObjectGroupPython] G4_BRAIN_ICRP  # scripted group (container) (typed FeaturePython)
  Dunit = g/cm3
  Dvalue = 1.04
  Group = -> [H_element017,C_element018,N_element012,O_element017,Na_element004,P_element004,S_element006,Cl_element003,K_element002]
  conduct = 2
  density = 1
  expand = 3
  formula = G4_BRAIN_ICRP
  name = G4_BRAIN_ICRP
  specific = 4
FEATURE [App::DocumentObjectGroupPython] C_element019  label="C_element : 4"  # scripted group (container) (typed FeaturePython)
  n = 4
  ref = C_element
FEATURE [App::DocumentObjectGroupPython] H_element018  label="H_element : 010"  # scripted group (container) (typed FeaturePython)
  n = 10
  ref = H_element
FEATURE [App::DocumentObjectGroupPython] G4_BUTANE  # scripted group (container) (typed FeaturePython)
  Dunit = g/cm3
  Dvalue = 0.00249343
  Group = -> [C_element019,H_element018]
  conduct = 2
  density = 1
  expand = 3
  formula = G4_BUTANE
  name = G4_BUTANE
  specific = 4
FEATURE [App::DocumentObjectGroupPython] C_element020  label="C_element : 008"  # scripted group (container) (typed FeaturePython)
  n = 4
  ref = C_element
FEATURE [App::DocumentObjectGroupPython] H_element019  label="H_element : 011"  # scripted group (container) (typed FeaturePython)
  n = 10
  ref = H_element
FEATURE [App::DocumentObjectGroupPython] O_element018  label="O_element : 007"  # scripted group (container) (typed FeaturePython)
  n = 1
  ref = O_element
FEATURE [App::DocumentObjectGroupPython] G4_N_BUTYL_ALCOHOL  label="G4_N-BUTYL_ALCOHOL"  # scripted group (container) (typed FeaturePython)
  Dunit = g/cm3
  Dvalue = 0.8098
  Group = -> [C_element020,H_element019,O_element018]
  conduct = 2
  density = 1
  expand = 3
  formula = G4_N-BUTYL_ALCOHOL
  name = G4_N-BUTYL_ALCOHOL
  specific = 4
FEATURE [App::DocumentObjectGroupPython] H_element020  label="H_element : 0.025"  # scripted group (container) (typed FeaturePython)
  n = 0.02468
FEATURE [App::DocumentObjectGroupPython] C_element021  label="C_element : 0.502"  # scripted group (container) (typed FeaturePython)
  n = 0.501611
FEATURE [App::DocumentObjectGroupPython] O_element019  label="O_element : 0.005"  # scripted group (container) (typed FeaturePython)
  n = 0.004527
FEATURE [App::DocumentObjectGroupPython] F_element004  label="F_element : 0.465"  # scripted group (container) (typed FeaturePython)
  n = 0.465209
FEATURE [App::DocumentObjectGroupPython] Si_element001  label="Si_element : 0.004"  # scripted group (container) (typed FeaturePython)
  n = 0.003973
FEATURE [App::DocumentObjectGroupPython] G4_C_552  label="G4_C-552"  # scripted group (container) (typed FeaturePython)
  Dunit = g/cm3
  Dvalue = 1.76
  Group = -> [H_element020,C_element021,O_element019,F_element004,Si_element001]
  conduct = 2
  density = 1
  expand = 3
  formula = G4_C-552
  name = G4_C-552
  specific = 4
FEATURE [App::DocumentObjectGroupPython] Cd_element001  label="Cd_element : 1"  # scripted group (container) (typed FeaturePython)
  n = 1
  ref = Cd_element
FEATURE [App::DocumentObjectGroupPython] Te_element001  label="Te_element : 1"  # scripted group (container) (typed FeaturePython)
  n = 1
  ref = Te_element
FEATURE [App::DocumentObjectGroupPython] G4_CADMIUM_TELLURIDE  # scripted group (container) (typed FeaturePython)
  Dunit = g/cm3
  Dvalue = 6.2
  Group = -> [Cd_element001,Te_element001]
  conduct = 2
  density = 1
  expand = 3
  formula = G4_CADMIUM_TELLURIDE
  name = G4_CADMIUM_TELLURIDE
  specific = 4
FEATURE [App::DocumentObjectGroupPython] Cd_element002  label="Cd_element : 002"  # scripted group (container) (typed FeaturePython)
  n = 1
  ref = Cd_element
FEATURE [App::DocumentObjectGroupPython] W_element001  label="W_element : 1"  # scripted group (container) (typed FeaturePython)
  n = 1
  ref = W_element
FEATURE [App::DocumentObjectGroupPython] O_element020  label="O_element : 008"  # scripted group (container) (typed FeaturePython)
  n = 4
  ref = O_element
FEATURE [App::DocumentObjectGroupPython] G4_CADMIUM_TUNGSTATE  # scripted group (container) (typed FeaturePython)
  Dunit = g/cm3
  Dvalue = 7.9
  Group = -> [Cd_element002,W_element001,O_element020]
  conduct = 2
  density = 1
  expand = 3
  formula = G4_CADMIUM_TUNGSTATE
  name = G4_CADMIUM_TUNGSTATE
  specific = 4
FEATURE [App::DocumentObjectGroupPython] Ca_element005  label="Ca_element : 1"  # scripted group (container) (typed FeaturePython)
  n = 1
  ref = Ca_element
FEATURE [App::DocumentObjectGroupPython] C_element022  label="C_element : 009"  # scripted group (container) (typed FeaturePython)
  n = 1
  ref = C_element
FEATURE [App::DocumentObjectGroupPython] O_element021  label="O_element : 009"  # scripted group (container) (typed FeaturePython)
  n = 3
  ref = O_element
FEATURE [App::DocumentObjectGroupPython] G4_CALCIUM_CARBONATE  # scripted group (container) (typed FeaturePython)
  Dunit = g/cm3
  Dvalue = 2.8
  Group = -> [Ca_element005,C_element022,O_element021]
  conduct = 2
  density = 1
  expand = 3
  formula = G4_CALCIUM_CARBONATE
  name = G4_CALCIUM_CARBONATE
  specific = 4
FEATURE [App::DocumentObjectGroupPython] Ca_element006  label="Ca_element : 002"  # scripted group (container) (typed FeaturePython)
  n = 1
  ref = Ca_element
FEATURE [App::DocumentObjectGroupPython] F_element005  label="F_element : 003"  # scripted group (container) (typed FeaturePython)
  n = 2
  ref = F_element
FEATURE [App::DocumentObjectGroupPython] G4_CALCIUM_FLUORIDE  # scripted group (container) (typed FeaturePython)
  Dunit = g/cm3
  Dvalue = 3.18
  Group = -> [Ca_element006,F_element005]
  conduct = 2
  density = 1
  expand = 3
  formula = G4_CALCIUM_FLUORIDE
  name = G4_CALCIUM_FLUORIDE
  specific = 4
FEATURE [App::DocumentObjectGroupPython] Ca_element007  label="Ca_element : 003"  # scripted group (container) (typed FeaturePython)
  n = 1
  ref = Ca_element
FEATURE [App::DocumentObjectGroupPython] O_element022  label="O_element : 010"  # scripted group (container) (typed FeaturePython)
  n = 1
  ref = O_element
FEATURE [App::DocumentObjectGroupPython] G4_CALCIUM_OXIDE  # scripted group (container) (typed FeaturePython)
  Dunit = g/cm3
  Dvalue = 3.3
  Group = -> [Ca_element007,O_element022]
  conduct = 2
  density = 1
  expand = 3
  formula = G4_CALCIUM_OXIDE
  name = G4_CALCIUM_OXIDE
  specific = 4
FEATURE [App::DocumentObjectGroupPython] Ca_element008  label="Ca_element : 004"  # scripted group (container) (typed FeaturePython)
  n = 1
  ref = Ca_element
FEATURE [App::DocumentObjectGroupPython] S_element007  label="S_element : 002"  # scripted group (container) (typed FeaturePython)
  n = 1
  ref = S_element
FEATURE [App::DocumentObjectGroupPython] O_element023  label="O_element : 011"  # scripted group (container) (typed FeaturePython)
  n = 4
  ref = O_element
FEATURE [App::DocumentObjectGroupPython] G4_CALCIUM_SULFATE  # scripted group (container) (typed FeaturePython)
  Dunit = g/cm3
  Dvalue = 2.96
  Group = -> [Ca_element008,S_element007,O_element023]
  conduct = 2
  density = 1
  expand = 3
  formula = G4_CALCIUM_SULFATE
  name = G4_CALCIUM_SULFATE
  specific = 4
FEATURE [App::DocumentObjectGroupPython] Ca_element009  label="Ca_element : 005"  # scripted group (container) (typed FeaturePython)
  n = 1
  ref = Ca_element
FEATURE [App::DocumentObjectGroupPython] W_element002  label="W_element : 002"  # scripted group (container) (typed FeaturePython)
  n = 1
  ref = W_element
FEATURE [App::DocumentObjectGroupPython] O_element024  label="O_element : 012"  # scripted group (container) (typed FeaturePython)
  n = 4
  ref = O_element
FEATURE [App::DocumentObjectGroupPython] G4_CALCIUM_TUNGSTATE  # scripted group (container) (typed FeaturePython)
  Dunit = g/cm3
  Dvalue = 6.062
  Group = -> [Ca_element009,W_element002,O_element024]
  conduct = 2
  density = 1
  expand = 3
  formula = G4_CALCIUM_TUNGSTATE
  name = G4_CALCIUM_TUNGSTATE
  specific = 4
FEATURE [App::DocumentObjectGroupPython] C_element023  label="C_element : 010"  # scripted group (container) (typed FeaturePython)
  n = 1
  ref = C_element
FEATURE [App::DocumentObjectGroupPython] O_element025  label="O_element : 013"  # scripted group (container) (typed FeaturePython)
  n = 2
  ref = O_element
FEATURE [App::DocumentObjectGroupPython] G4_CARBON_DIOXIDE  # scripted group (container) (typed FeaturePython)
  Dunit = g/cm3
  Dvalue = 0.00184212
  Group = -> [C_element023,O_element025]
  conduct = 2
  density = 1
  expand = 3
  formula = G4_CARBON_DIOXIDE
  name = G4_CARBON_DIOXIDE
  specific = 4
FEATURE [App::DocumentObjectGroupPython] C_element024  label="C_element : 011"  # scripted group (container) (typed FeaturePython)
  n = 1
  ref = C_element
FEATURE [App::DocumentObjectGroupPython] Cl_element004  label="Cl_element : 4"  # scripted group (container) (typed FeaturePython)
  n = 4
  ref = Cl_element
FEATURE [App::DocumentObjectGroupPython] G4_CARBON_TETRACHLORIDE  # scripted group (container) (typed FeaturePython)
  Dunit = g/cm3
  Dvalue = 1.594
  Group = -> [C_element024,Cl_element004]
  conduct = 2
  density = 1
  expand = 3
  formula = G4_CARBON_TETRACHLORIDE
  name = G4_CARBON_TETRACHLORIDE
  specific = 4
FEATURE [App::DocumentObjectGroupPython] C_element025  label="C_element : 012"  # scripted group (container) (typed FeaturePython)
  n = 6
  ref = C_element
FEATURE [App::DocumentObjectGroupPython] H_element021  label="H_element : 012"  # scripted group (container) (typed FeaturePython)
  n = 10
  ref = H_element
FEATURE [App::DocumentObjectGroupPython] O_element026  label="O_element : 5"  # scripted group (container) (typed FeaturePython)
  n = 5
  ref = O_element
FEATURE [App::DocumentObjectGroupPython] G4_CELLULOSE_CELLOPHANE  # scripted group (container) (typed FeaturePython)
  Dunit = g/cm3
  Dvalue = 1.42
  Group = -> [C_element025,H_element021,O_element026]
  conduct = 2
  density = 1
  expand = 3
  formula = G4_CELLULOSE_CELLOPHANE
  name = G4_CELLULOSE_CELLOPHANE
  specific = 4
FEATURE [App::DocumentObjectGroupPython] H_element022  label="H_element : 0.067"  # scripted group (container) (typed FeaturePython)
  n = 0.067125
FEATURE [App::DocumentObjectGroupPython] C_element026  label="C_element : 0.545"  # scripted group (container) (typed FeaturePython)
  n = 0.545403
FEATURE [App::DocumentObjectGroupPython] O_element027  label="O_element : 0.387"  # scripted group (container) (typed FeaturePython)
  n = 0.387472
FEATURE [App::DocumentObjectGroupPython] G4_CELLULOSE_BUTYRATE  # scripted group (container) (typed FeaturePython)
  Dunit = g/cm3
  Dvalue = 1.2
  Group = -> [H_element022,C_element026,O_element027]
  conduct = 2
  density = 1
  expand = 3
  formula = G4_CELLULOSE_BUTYRATE
  name = G4_CELLULOSE_BUTYRATE
  specific = 4
FEATURE [App::DocumentObjectGroupPython] H_element023  label="H_element : 0.029"  # scripted group (container) (typed FeaturePython)
  n = 0.029216
FEATURE [App::DocumentObjectGroupPython] C_element027  label="C_element : 0.271"  # scripted group (container) (typed FeaturePython)
  n = 0.271296
FEATURE [App::DocumentObjectGroupPython] N_element013  label="N_element : 0.121"  # scripted group (container) (typed FeaturePython)
  n = 0.121276
FEATURE [App::DocumentObjectGroupPython] O_element028  label="O_element : 0.578"  # scripted group (container) (typed FeaturePython)
  n = 0.578212
FEATURE [App::DocumentObjectGroupPython] G4_CELLULOSE_NITRATE  # scripted group (container) (typed FeaturePython)
  Dunit = g/cm3
  Dvalue = 1.49
  Group = -> [H_element023,C_element027,N_element013,O_element028]
  conduct = 2
  density = 1
  expand = 3
  formula = G4_CELLULOSE_NITRATE
  name = G4_CELLULOSE_NITRATE
  specific = 4
FEATURE [App::DocumentObjectGroupPython] H_element024  label="H_element : 0.108"  # scripted group (container) (typed FeaturePython)
  n = 0.107596
FEATURE [App::DocumentObjectGroupPython] N_element014  label="N_element : 0.001"  # scripted group (container) (typed FeaturePython)
  n = 0.0008
FEATURE [App::DocumentObjectGroupPython] O_element029  label="O_element : 0.875"  # scripted group (container) (typed FeaturePython)
  n = 0.874976
FEATURE [App::DocumentObjectGroupPython] S_element008  label="S_element : 0.015"  # scripted group (container) (typed FeaturePython)
  n = 0.014627
FEATURE [App::DocumentObjectGroupPython] Ce_element001  label="Ce_element : 0.002"  # scripted group (container) (typed FeaturePython)
  n = 0.002001
FEATURE [App::DocumentObjectGroupPython] G4_CERIC_SULFATE  # scripted group (container) (typed FeaturePython)
  Dunit = g/cm3
  Dvalue = 1.03
  Group = -> [H_element024,N_element014,O_element029,S_element008,Ce_element001]
  conduct = 2
  density = 1
  expand = 3
  formula = G4_CERIC_SULFATE
  name = G4_CERIC_SULFATE
  specific = 4
FEATURE [App::DocumentObjectGroupPython] Cs_element001  label="Cs_element : 1"  # scripted group (container) (typed FeaturePython)
  n = 1
  ref = Cs_element
FEATURE [App::DocumentObjectGroupPython] F_element006  label="F_element : 1"  # scripted group (container) (typed FeaturePython)
  n = 1
  ref = F_element
FEATURE [App::DocumentObjectGroupPython] G4_CESIUM_FLUORIDE  # scripted group (container) (typed FeaturePython)
  Dunit = g/cm3
  Dvalue = 4.115
  Group = -> [Cs_element001,F_element006]
  conduct = 2
  density = 1
  expand = 3
  formula = G4_CESIUM_FLUORIDE
  name = G4_CESIUM_FLUORIDE
  specific = 4
FEATURE [App::DocumentObjectGroupPython] Cs_element002  label="Cs_element : 002"  # scripted group (container) (typed FeaturePython)
  n = 1
  ref = Cs_element
FEATURE [App::DocumentObjectGroupPython] I_element001  label="I_element : 1"  # scripted group (container) (typed FeaturePython)
  n = 1
  ref = I_element
FEATURE [App::DocumentObjectGroupPython] G4_CESIUM_IODIDE  # scripted group (container) (typed FeaturePython)
  Dunit = g/cm3
  Dvalue = 4.51
  Group = -> [Cs_element002,I_element001]
  conduct = 2
  density = 1
  expand = 3
  formula = G4_CESIUM_IODIDE
  name = G4_CESIUM_IODIDE
  specific = 4
FEATURE [App::DocumentObjectGroupPython] C_element028  label="C_element : 013"  # scripted group (container) (typed FeaturePython)
  n = 6
  ref = C_element
FEATURE [App::DocumentObjectGroupPython] H_element025  label="H_element : 013"  # scripted group (container) (typed FeaturePython)
  n = 5
  ref = H_element
FEATURE [App::DocumentObjectGroupPython] Cl_element005  label="Cl_element : 1"  # scripted group (container) (typed FeaturePython)
  n = 1
  ref = Cl_element
FEATURE [App::DocumentObjectGroupPython] G4_CHLOROBENZENE  # scripted group (container) (typed FeaturePython)
  Dunit = g/cm3
  Dvalue = 1.1058
  Group = -> [C_element028,H_element025,Cl_element005]
  conduct = 2
  density = 1
  expand = 3
  formula = G4_CHLOROBENZENE
  name = G4_CHLOROBENZENE
  specific = 4
FEATURE [App::DocumentObjectGroupPython] C_element029  label="C_element : 014"  # scripted group (container) (typed FeaturePython)
  n = 1
  ref = C_element
FEATURE [App::DocumentObjectGroupPython] H_element026  label="H_element : 1"  # scripted group (container) (typed FeaturePython)
  n = 1
  ref = H_element
FEATURE [App::DocumentObjectGroupPython] Cl_element006  label="Cl_element : 3"  # scripted group (container) (typed FeaturePython)
  n = 3
  ref = Cl_element
FEATURE [App::DocumentObjectGroupPython] G4_CHLOROFORM  # scripted group (container) (typed FeaturePython)
  Dunit = g/cm3
  Dvalue = 1.4832
  Group = -> [C_element029,H_element026,Cl_element006]
  conduct = 2
  density = 1
  expand = 3
  formula = G4_CHLOROFORM
  name = G4_CHLOROFORM
  specific = 4
FEATURE [App::DocumentObjectGroupPython] H_element027  label="H_element : 0.010"  # scripted group (container) (typed FeaturePython)
  n = 0.01
FEATURE [App::DocumentObjectGroupPython] C_element030  label="C_element : 0.001"  # scripted group (container) (typed FeaturePython)
  n = 0.001
FEATURE [App::DocumentObjectGroupPython] O_element030  label="O_element : 0.529"  # scripted group (container) (typed FeaturePython)
  n = 0.529107
FEATURE [App::DocumentObjectGroupPython] Na_element005  label="Na_element : 0.016"  # scripted group (container) (typed FeaturePython)
  n = 0.016
FEATURE [App::DocumentObjectGroupPython] Mg_element003  label="Mg_element : 0.004"  # scripted group (container) (typed FeaturePython)
  n = 0.002
FEATURE [App::DocumentObjectGroupPython] Al_element002  label="Al_element : 0.034"  # scripted group (container) (typed FeaturePython)
  n = 0.033872
FEATURE [App::DocumentObjectGroupPython] Si_element002  label="Si_element : 0.337"  # scripted group (container) (typed FeaturePython)
  n = 0.337021
FEATURE [App::DocumentObjectGroupPython] K_element003  label="K_element : 0.013"  # scripted group (container) (typed FeaturePython)
  n = 0.013
FEATURE [App::DocumentObjectGroupPython] Ca_element010  label="Ca_element : 0.044"  # scripted group (container) (typed FeaturePython)
  n = 0.044
FEATURE [App::DocumentObjectGroupPython] Fe_element002  label="Fe_element : 0.014"  # scripted group (container) (typed FeaturePython)
  n = 0.014
FEATURE [App::DocumentObjectGroupPython] G4_CONCRETE  # scripted group (container) (typed FeaturePython)
  Dunit = g/cm3
  Dvalue = 2.3
  Group = -> [H_element027,C_element030,O_element030,Na_element005,Mg_element003,Al_element002,Si_element002,K_element003,Ca_element010,Fe_element002]
  conduct = 2
  density = 1
  expand = 3
  formula = G4_CONCRETE
  name = G4_CONCRETE
  specific = 4
FEATURE [App::DocumentObjectGroupPython] C_element031  label="C_element : 015"  # scripted group (container) (typed FeaturePython)
  n = 6
  ref = C_element
FEATURE [App::DocumentObjectGroupPython] H_element028  label="H_element : 12"  # scripted group (container) (typed FeaturePython)
  n = 12
  ref = H_element
FEATURE [App::DocumentObjectGroupPython] G4_CYCLOHEXANE  # scripted group (container) (typed FeaturePython)
  Dunit = g/cm3
  Dvalue = 0.779
  Group = -> [C_element031,H_element028]
  conduct = 2
  density = 1
  expand = 3
  formula = G4_CYCLOHEXANE
  name = G4_CYCLOHEXANE
  specific = 4
FEATURE [App::DocumentObjectGroupPython] C_element032  label="C_element : 016"  # scripted group (container) (typed FeaturePython)
  n = 6
  ref = C_element
FEATURE [App::DocumentObjectGroupPython] H_element029  label="H_element : 4"  # scripted group (container) (typed FeaturePython)
  n = 4
  ref = H_element
FEATURE [App::DocumentObjectGroupPython] Cl_element007  label="Cl_element : 2"  # scripted group (container) (typed FeaturePython)
  n = 2
  ref = Cl_element
FEATURE [App::DocumentObjectGroupPython] G4_1_2_DICHLOROBENZENE  label="G4_1.2-DICHLOROBENZENE"  # scripted group (container) (typed FeaturePython)
  Dunit = g/cm3
  Dvalue = 1.3048
  Group = -> [C_element032,H_element029,Cl_element007]
  conduct = 2
  density = 1
  expand = 3
  formula = G4_1.2-DICHLOROBENZENE
  name = G4_1.2-DICHLOROBENZENE
  specific = 4
FEATURE [App::DocumentObjectGroupPython] C_element033  label="C_element : 017"  # scripted group (container) (typed FeaturePython)
  n = 4
  ref = C_element
FEATURE [App::DocumentObjectGroupPython] H_element030  label="H_element : 8"  # scripted group (container) (typed FeaturePython)
  n = 8
  ref = H_element
FEATURE [App::DocumentObjectGroupPython] O_element031  label="O_element : 014"  # scripted group (container) (typed FeaturePython)
  n = 1
  ref = O_element
FEATURE [App::DocumentObjectGroupPython] Cl_element008  label="Cl_element : 005"  # scripted group (container) (typed FeaturePython)
  n = 2
  ref = Cl_element
FEATURE [App::DocumentObjectGroupPython] G4_DICHLORODIETHYL_ETHER  # scripted group (container) (typed FeaturePython)
  Dunit = g/cm3
  Dvalue = 1.2199
  Group = -> [C_element033,H_element030,O_element031,Cl_element008]
  conduct = 2
  density = 1
  expand = 3
  formula = G4_DICHLORODIETHYL_ETHER
  name = G4_DICHLORODIETHYL_ETHER
  specific = 4
FEATURE [App::DocumentObjectGroupPython] C_element034  label="C_element : 018"  # scripted group (container) (typed FeaturePython)
  n = 2
  ref = C_element
FEATURE [App::DocumentObjectGroupPython] H_element031  label="H_element : 014"  # scripted group (container) (typed FeaturePython)
  n = 4
  ref = H_element
FEATURE [App::DocumentObjectGroupPython] Cl_element009  label="Cl_element : 006"  # scripted group (container) (typed FeaturePython)
  n = 2
  ref = Cl_element
FEATURE [App::DocumentObjectGroupPython] G4_1_2_DICHLOROETHANE  label="G4_1.2-DICHLOROETHANE"  # scripted group (container) (typed FeaturePython)
  Dunit = g/cm3
  Dvalue = 1.2351
  Group = -> [C_element034,H_element031,Cl_element009]
  conduct = 2
  density = 1
  expand = 3
  formula = G4_1.2-DICHLOROETHANE
  name = G4_1.2-DICHLOROETHANE
  specific = 4
FEATURE [App::DocumentObjectGroupPython] C_element035  label="C_element : 019"  # scripted group (container) (typed FeaturePython)
  n = 4
  ref = C_element
FEATURE [App::DocumentObjectGroupPython] H_element032  label="H_element : 015"  # scripted group (container) (typed FeaturePython)
  n = 10
  ref = H_element
FEATURE [App::DocumentObjectGroupPython] O_element032  label="O_element : 015"  # scripted group (container) (typed FeaturePython)
  n = 1
  ref = O_element
FEATURE [App::DocumentObjectGroupPython] G4_DIETHYL_ETHER  # scripted group (container) (typed FeaturePython)
  Dunit = g/cm3
  Dvalue = 0.71378
  Group = -> [C_element035,H_element032,O_element032]
  conduct = 2
  density = 1
  expand = 3
  formula = G4_DIETHYL_ETHER
  name = G4_DIETHYL_ETHER
  specific = 4
FEATURE [App::DocumentObjectGroupPython] C_element036  label="C_element : 020"  # scripted group (container) (typed FeaturePython)
  n = 3
  ref = C_element
FEATURE [App::DocumentObjectGroupPython] H_element033  label="H_element : 016"  # scripted group (container) (typed FeaturePython)
  n = 7
  ref = H_element
FEATURE [App::DocumentObjectGroupPython] N_element015  label="N_element : 008"  # scripted group (container) (typed FeaturePython)
  n = 1
  ref = N_element
FEATURE [App::DocumentObjectGroupPython] O_element033  label="O_element : 016"  # scripted group (container) (typed FeaturePython)
  n = 1
  ref = O_element
FEATURE [App::DocumentObjectGroupPython] G4_N_N_DIMETHYL_FORMAMIDE  label="G4_N.N-DIMETHYL_FORMAMIDE"  # scripted group (container) (typed FeaturePython)
  Dunit = g/cm3
  Dvalue = 0.9487
  Group = -> [C_element036,H_element033,N_element015,O_element033]
  conduct = 2
  density = 1
  expand = 3
  formula = G4_N.N-DIMETHYL_FORMAMIDE
  name = G4_N.N-DIMETHYL_FORMAMIDE
  specific = 4
FEATURE [App::DocumentObjectGroupPython] C_element037  label="C_element : 021"  # scripted group (container) (typed FeaturePython)
  n = 2
  ref = C_element
FEATURE [App::DocumentObjectGroupPython] H_element034  label="H_element : 017"  # scripted group (container) (typed FeaturePython)
  n = 6
  ref = H_element
FEATURE [App::DocumentObjectGroupPython] O_element034  label="O_element : 017"  # scripted group (container) (typed FeaturePython)
  n = 1
  ref = O_element
FEATURE [App::DocumentObjectGroupPython] S_element009  label="S_element : 003"  # scripted group (container) (typed FeaturePython)
  n = 1
  ref = S_element
FEATURE [App::DocumentObjectGroupPython] G4_DIMETHYL_SULFOXIDE  # scripted group (container) (typed FeaturePython)
  Dunit = g/cm3
  Dvalue = 1.1014
  Group = -> [C_element037,H_element034,O_element034,S_element009]
  conduct = 2
  density = 1
  expand = 3
  formula = G4_DIMETHYL_SULFOXIDE
  name = G4_DIMETHYL_SULFOXIDE
  specific = 4
FEATURE [App::DocumentObjectGroupPython] C_element038  label="C_element : 022"  # scripted group (container) (typed FeaturePython)
  n = 2
  ref = C_element
FEATURE [App::DocumentObjectGroupPython] H_element035  label="H_element : 018"  # scripted group (container) (typed FeaturePython)
  n = 6
  ref = H_element
FEATURE [App::DocumentObjectGroupPython] G4_ETHANE  # scripted group (container) (typed FeaturePython)
  Dunit = g/cm3
  Dvalue = 0.00125324
  Group = -> [C_element038,H_element035]
  conduct = 2
  density = 1
  expand = 3
  formula = G4_ETHANE
  name = G4_ETHANE
  specific = 4
FEATURE [App::DocumentObjectGroupPython] C_element039  label="C_element : 023"  # scripted group (container) (typed FeaturePython)
  n = 2
  ref = C_element
FEATURE [App::DocumentObjectGroupPython] H_element036  label="H_element : 019"  # scripted group (container) (typed FeaturePython)
  n = 6
  ref = H_element
FEATURE [App::DocumentObjectGroupPython] O_element035  label="O_element : 018"  # scripted group (container) (typed FeaturePython)
  n = 1
  ref = O_element
FEATURE [App::DocumentObjectGroupPython] G4_ETHYL_ALCOHOL  # scripted group (container) (typed FeaturePython)
  Dunit = g/cm3
  Dvalue = 0.7893
  Group = -> [C_element039,H_element036,O_element035]
  conduct = 2
  density = 1
  expand = 3
  formula = G4_ETHYL_ALCOHOL
  name = G4_ETHYL_ALCOHOL
  specific = 4
FEATURE [App::DocumentObjectGroupPython] H_element037  label="H_element : 0.090"  # scripted group (container) (typed FeaturePython)
  n = 0.090027
FEATURE [App::DocumentObjectGroupPython] C_element040  label="C_element : 0.585"  # scripted group (container) (typed FeaturePython)
  n = 0.585182
FEATURE [App::DocumentObjectGroupPython] O_element036  label="O_element : 0.325"  # scripted group (container) (typed FeaturePython)
  n = 0.324791
FEATURE [App::DocumentObjectGroupPython] G4_ETHYL_CELLULOSE  # scripted group (container) (typed FeaturePython)
  Dunit = g/cm3
  Dvalue = 1.13
  Group = -> [H_element037,C_element040,O_element036]
  conduct = 2
  density = 1
  expand = 3
  formula = G4_ETHYL_CELLULOSE
  name = G4_ETHYL_CELLULOSE
  specific = 4
FEATURE [App::DocumentObjectGroupPython] C_element041  label="C_element : 024"  # scripted group (container) (typed FeaturePython)
  n = 2
  ref = C_element
FEATURE [App::DocumentObjectGroupPython] H_element038  label="H_element : 020"  # scripted group (container) (typed FeaturePython)
  n = 4
  ref = H_element
FEATURE [App::DocumentObjectGroupPython] G4_ETHYLENE  # scripted group (container) (typed FeaturePython)
  Dunit = g/cm3
  Dvalue = 0.00117497
  Group = -> [C_element041,H_element038]
  conduct = 2
  density = 1
  expand = 3
  formula = G4_ETHYLENE
  name = G4_ETHYLENE
  specific = 4
FEATURE [App::DocumentObjectGroupPython] H_element039  label="H_element : 0.096"  # scripted group (container) (typed FeaturePython)
  n = 0.096
FEATURE [App::DocumentObjectGroupPython] C_element042  label="C_element : 0.195"  # scripted group (container) (typed FeaturePython)
  n = 0.195
FEATURE [App::DocumentObjectGroupPython] N_element016  label="N_element : 0.057"  # scripted group (container) (typed FeaturePython)
  n = 0.057
FEATURE [App::DocumentObjectGroupPython] O_element037  label="O_element : 0.646"  # scripted group (container) (typed FeaturePython)
  n = 0.646
FEATURE [App::DocumentObjectGroupPython] Na_element006  label="Na_element : 0.017"  # scripted group (container) (typed FeaturePython)
  n = 0.001
FEATURE [App::DocumentObjectGroupPython] P_element005  label="P_element : 0.104"  # scripted group (container) (typed FeaturePython)
  n = 0.001
FEATURE [App::DocumentObjectGroupPython] S_element010  label="S_element : 0.016"  # scripted group (container) (typed FeaturePython)
  n = 0.003
FEATURE [App::DocumentObjectGroupPython] Cl_element010  label="Cl_element : 0.005"  # scripted group (container) (typed FeaturePython)
  n = 0.001
FEATURE [App::DocumentObjectGroupPython] G4_EYE_LENS_ICRP  # scripted group (container) (typed FeaturePython)
  Dunit = g/cm3
  Dvalue = 1.07
  Group = -> [H_element039,C_element042,N_element016,O_element037,Na_element006,P_element005,S_element010,Cl_element010]
  conduct = 2
  density = 1
  expand = 3
  formula = G4_EYE_LENS_ICRP
  name = G4_EYE_LENS_ICRP
  specific = 4
FEATURE [App::DocumentObjectGroupPython] Fe_element003  label="Fe_element : 2"  # scripted group (container) (typed FeaturePython)
  n = 2
  ref = Fe_element
FEATURE [App::DocumentObjectGroupPython] O_element038  label="O_element : 019"  # scripted group (container) (typed FeaturePython)
  n = 3
  ref = O_element
FEATURE [App::DocumentObjectGroupPython] G4_FERRIC_OXIDE  # scripted group (container) (typed FeaturePython)
  Dunit = g/cm3
  Dvalue = 5.2
  Group = -> [Fe_element003,O_element038]
  conduct = 2
  density = 1
  expand = 3
  formula = G4_FERRIC_OXIDE
  name = G4_FERRIC_OXIDE
  specific = 4
FEATURE [App::DocumentObjectGroupPython] Fe_element004  label="Fe_element : 1"  # scripted group (container) (typed FeaturePython)
  n = 1
  ref = Fe_element
FEATURE [App::DocumentObjectGroupPython] B_element003  label="B_element : 1"  # scripted group (container) (typed FeaturePython)
  n = 1
  ref = B_element
FEATURE [App::DocumentObjectGroupPython] G4_FERROBORIDE  # scripted group (container) (typed FeaturePython)
  Dunit = g/cm3
  Dvalue = 7.15
  Group = -> [Fe_element004,B_element003]
  conduct = 2
  density = 1
  expand = 3
  formula = G4_FERROBORIDE
  name = G4_FERROBORIDE
  specific = 4
FEATURE [App::DocumentObjectGroupPython] Fe_element005  label="Fe_element : 003"  # scripted group (container) (typed FeaturePython)
  n = 1
  ref = Fe_element
FEATURE [App::DocumentObjectGroupPython] O_element039  label="O_element : 020"  # scripted group (container) (typed FeaturePython)
  n = 1
  ref = O_element
FEATURE [App::DocumentObjectGroupPython] G4_FERROUS_OXIDE  # scripted group (container) (typed FeaturePython)
  Dunit = g/cm3
  Dvalue = 5.7
  Group = -> [Fe_element005,O_element039]
  conduct = 2
  density = 1
  expand = 3
  formula = G4_FERROUS_OXIDE
  name = G4_FERROUS_OXIDE
  specific = 4
FEATURE [App::DocumentObjectGroupPython] H_element040  label="H_element : 0.115"  # scripted group (container) (typed FeaturePython)
  n = 0.108259
FEATURE [App::DocumentObjectGroupPython] N_element017  label="N_element : 0.000"  # scripted group (container) (typed FeaturePython)
  n = 2.7e-05
FEATURE [App::DocumentObjectGroupPython] O_element040  label="O_element : 0.879"  # scripted group (container) (typed FeaturePython)
  n = 0.878636
FEATURE [App::DocumentObjectGroupPython] Na_element007  label="Na_element : 0.000"  # scripted group (container) (typed FeaturePython)
  n = 2.2e-05
FEATURE [App::DocumentObjectGroupPython] S_element011  label="S_element : 0.013"  # scripted group (container) (typed FeaturePython)
  n = 0.012968
FEATURE [App::DocumentObjectGroupPython] Cl_element011  label="Cl_element : 0.000"  # scripted group (container) (typed FeaturePython)
  n = 3.4e-05
FEATURE [App::DocumentObjectGroupPython] Fe_element006  label="Fe_element : 0.000"  # scripted group (container) (typed FeaturePython)
  n = 5.4e-05
FEATURE [App::DocumentObjectGroupPython] G4_FERROUS_SULFATE  # scripted group (container) (typed FeaturePython)
  Dunit = g/cm3
  Dvalue = 1.024
  Group = -> [H_element040,N_element017,O_element040,Na_element007,S_element011,Cl_element011,Fe_element006]
  conduct = 2
  density = 1
  expand = 3
  formula = G4_FERROUS_SULFATE
  name = G4_FERROUS_SULFATE
  specific = 4
FEATURE [App::DocumentObjectGroupPython] C_element043  label="C_element : 0.099"  # scripted group (container) (typed FeaturePython)
  n = 0.099335
FEATURE [App::DocumentObjectGroupPython] F_element007  label="F_element : 0.314"  # scripted group (container) (typed FeaturePython)
  n = 0.314247
FEATURE [App::DocumentObjectGroupPython] Cl_element012  label="Cl_element : 0.586"  # scripted group (container) (typed FeaturePython)
  n = 0.586418
FEATURE [App::DocumentObjectGroupPython] G4_FREON_12  label="G4_FREON-12"  # scripted group (container) (typed FeaturePython)
  Dunit = g/cm3
  Dvalue = 1.12
  Group = -> [C_element043,F_element007,Cl_element012]
  conduct = 2
  density = 1
  expand = 3
  formula = G4_FREON-12
  name = G4_FREON-12
  specific = 4
FEATURE [App::DocumentObjectGroupPython] C_element044  label="C_element : 0.057"  # scripted group (container) (typed FeaturePython)
  n = 0.057245
FEATURE [App::DocumentObjectGroupPython] F_element008  label="F_element : 0.181"  # scripted group (container) (typed FeaturePython)
  n = 0.181096
FEATURE [App::DocumentObjectGroupPython] Br_element001  label="Br_element : 0.762"  # scripted group (container) (typed FeaturePython)
  n = 0.761659
FEATURE [App::DocumentObjectGroupPython] G4_FREON_12B2  label="G4_FREON-12B2"  # scripted group (container) (typed FeaturePython)
  Dunit = g/cm3
  Dvalue = 1.8
  Group = -> [C_element044,F_element008,Br_element001]
  conduct = 2
  density = 1
  expand = 3
  formula = G4_FREON-12B2
  name = G4_FREON-12B2
  specific = 4
FEATURE [App::DocumentObjectGroupPython] C_element045  label="C_element : 0.115"  # scripted group (container) (typed FeaturePython)
  n = 0.114983
FEATURE [App::DocumentObjectGroupPython] F_element009  label="F_element : 0.546"  # scripted group (container) (typed FeaturePython)
  n = 0.545621
FEATURE [App::DocumentObjectGroupPython] Cl_element013  label="Cl_element : 0.339"  # scripted group (container) (typed FeaturePython)
  n = 0.339396
FEATURE [App::DocumentObjectGroupPython] G4_FREON_13  label="G4_FREON-13"  # scripted group (container) (typed FeaturePython)
  Dunit = g/cm3
  Dvalue = 0.95
  Group = -> [C_element045,F_element009,Cl_element013]
  conduct = 2
  density = 1
  expand = 3
  formula = G4_FREON-13
  name = G4_FREON-13
  specific = 4
FEATURE [App::DocumentObjectGroupPython] C_element046  label="C_element : 025"  # scripted group (container) (typed FeaturePython)
  n = 1
  ref = C_element
FEATURE [App::DocumentObjectGroupPython] F_element010  label="F_element : 3"  # scripted group (container) (typed FeaturePython)
  n = 3
  ref = F_element
FEATURE [App::DocumentObjectGroupPython] Br_element002  label="Br_element : 1"  # scripted group (container) (typed FeaturePython)
  n = 1
  ref = Br_element
FEATURE [App::DocumentObjectGroupPython] G4_FREON_13B1  label="G4_FREON-13B1"  # scripted group (container) (typed FeaturePython)
  Dunit = g/cm3
  Dvalue = 1.5
  Group = -> [C_element046,F_element010,Br_element002]
  conduct = 2
  density = 1
  expand = 3
  formula = G4_FREON-13B1
  name = G4_FREON-13B1
  specific = 4
FEATURE [App::DocumentObjectGroupPython] C_element047  label="C_element : 0.061"  # scripted group (container) (typed FeaturePython)
  n = 0.061309
FEATURE [App::DocumentObjectGroupPython] F_element011  label="F_element : 0.291"  # scripted group (container) (typed FeaturePython)
  n = 0.290924
FEATURE [App::DocumentObjectGroupPython] I_element002  label="I_element : 0.648"  # scripted group (container) (typed FeaturePython)
  n = 0.647767
FEATURE [App::DocumentObjectGroupPython] G4_FREON_13I1  label="G4_FREON-13I1"  # scripted group (container) (typed FeaturePython)
  Dunit = g/cm3
  Dvalue = 1.8
  Group = -> [C_element047,F_element011,I_element002]
  conduct = 2
  density = 1
  expand = 3
  formula = G4_FREON-13I1
  name = G4_FREON-13I1
  specific = 4
FEATURE [App::DocumentObjectGroupPython] Gd_element001  label="Gd_element : 2"  # scripted group (container) (typed FeaturePython)
  n = 2
  ref = Gd_element
FEATURE [App::DocumentObjectGroupPython] O_element041  label="O_element : 021"  # scripted group (container) (typed FeaturePython)
  n = 2
  ref = O_element
FEATURE [App::DocumentObjectGroupPython] S_element012  label="S_element : 004"  # scripted group (container) (typed FeaturePython)
  n = 1
  ref = S_element
FEATURE [App::DocumentObjectGroupPython] G4_GADOLINIUM_OXYSULFIDE  # scripted group (container) (typed FeaturePython)
  Dunit = g/cm3
  Dvalue = 7.44
  Group = -> [Gd_element001,O_element041,S_element012]
  conduct = 2
  density = 1
  expand = 3
  formula = G4_GADOLINIUM_OXYSULFIDE
  name = G4_GADOLINIUM_OXYSULFIDE
  specific = 4
FEATURE [App::DocumentObjectGroupPython] Ga_element001  label="Ga_element : 1"  # scripted group (container) (typed FeaturePython)
  n = 1
  ref = Ga_element
FEATURE [App::DocumentObjectGroupPython] As_element001  label="As_element : 1"  # scripted group (container) (typed FeaturePython)
  n = 1
  ref = As_element
FEATURE [App::DocumentObjectGroupPython] G4_GALLIUM_ARSENIDE  # scripted group (container) (typed FeaturePython)
  Dunit = g/cm3
  Dvalue = 5.31
  Group = -> [Ga_element001,As_element001]
  conduct = 2
  density = 1
  expand = 3
  formula = G4_GALLIUM_ARSENIDE
  name = G4_GALLIUM_ARSENIDE
  specific = 4
FEATURE [App::DocumentObjectGroupPython] H_element041  label="H_element : 0.081"  # scripted group (container) (typed FeaturePython)
  n = 0.08118
FEATURE [App::DocumentObjectGroupPython] C_element048  label="C_element : 0.416"  # scripted group (container) (typed FeaturePython)
  n = 0.41606
FEATURE [App::DocumentObjectGroupPython] N_element018  label="N_element : 0.111"  # scripted group (container) (typed FeaturePython)
  n = 0.11124
FEATURE [App::DocumentObjectGroupPython] O_element042  label="O_element : 0.381"  # scripted group (container) (typed FeaturePython)
  n = 0.38064
FEATURE [App::DocumentObjectGroupPython] S_element013  label="S_element : 0.011"  # scripted group (container) (typed FeaturePython)
  n = 0.01088
FEATURE [App::DocumentObjectGroupPython] G4_GEL_PHOTO_EMULSION  # scripted group (container) (typed FeaturePython)
  Dunit = g/cm3
  Dvalue = 1.2914
  Group = -> [H_element041,C_element048,N_element018,O_element042,S_element013]
  conduct = 2
  density = 1
  expand = 3
  formula = G4_GEL_PHOTO_EMULSION
  name = G4_GEL_PHOTO_EMULSION
  specific = 4
FEATURE [App::DocumentObjectGroupPython] B_element004  label="B_element : 0.040"  # scripted group (container) (typed FeaturePython)
  n = 0.0400639
FEATURE [App::DocumentObjectGroupPython] O_element043  label="O_element : 0.540"  # scripted group (container) (typed FeaturePython)
  n = 0.539561
FEATURE [App::DocumentObjectGroupPython] Na_element008  label="Na_element : 0.028"  # scripted group (container) (typed FeaturePython)
  n = 0.0281909
FEATURE [App::DocumentObjectGroupPython] Al_element003  label="Al_element : 0.012"  # scripted group (container) (typed FeaturePython)
  n = 0.011644
FEATURE [App::DocumentObjectGroupPython] Si_element003  label="Si_element : 0.377"  # scripted group (container) (typed FeaturePython)
  n = 0.377219
FEATURE [App::DocumentObjectGroupPython] K_element004  label="K_element : 0.014"  # scripted group (container) (typed FeaturePython)
  n = 0.00332099
FEATURE [App::DocumentObjectGroupPython] G4_Pyrex_Glass  # scripted group (container) (typed FeaturePython)
  Dunit = g/cm3
  Dvalue = 2.23
  Group = -> [B_element004,O_element043,Na_element008,Al_element003,Si_element003,K_element004]
  conduct = 2
  density = 1
  expand = 3
  formula = G4_Pyrex_Glass
  name = G4_Pyrex_Glass
  specific = 4
FEATURE [App::DocumentObjectGroupPython] O_element044  label="O_element : 0.156"  # scripted group (container) (typed FeaturePython)
  n = 0.156453
FEATURE [App::DocumentObjectGroupPython] Si_element004  label="Si_element : 0.081"  # scripted group (container) (typed FeaturePython)
  n = 0.080866
FEATURE [App::DocumentObjectGroupPython] Ti_element001  label="Ti_element : 0.008"  # scripted group (container) (typed FeaturePython)
  n = 0.008092
FEATURE [App::DocumentObjectGroupPython] As_element002  label="As_element : 0.003"  # scripted group (container) (typed FeaturePython)
  n = 0.002651
FEATURE [App::DocumentObjectGroupPython] Pb_element001  label="Pb_element : 0.752"  # scripted group (container) (typed FeaturePython)
  n = 0.751938
FEATURE [App::DocumentObjectGroupPython] G4_GLASS_LEAD  # scripted group (container) (typed FeaturePython)
  Dunit = g/cm3
  Dvalue = 6.22
  Group = -> [O_element044,Si_element004,Ti_element001,As_element002,Pb_element001]
  conduct = 2
  density = 1
  expand = 3
  formula = G4_GLASS_LEAD
  name = G4_GLASS_LEAD
  specific = 4
FEATURE [App::DocumentObjectGroupPython] O_element045  label="O_element : 0.460"  # scripted group (container) (typed FeaturePython)
  n = 0.4598
FEATURE [App::DocumentObjectGroupPython] Na_element009  label="Na_element : 0.096"  # scripted group (container) (typed FeaturePython)
  n = 0.0964411
FEATURE [App::DocumentObjectGroupPython] Si_element005  label="Si_element : 0.378"  # scripted group (container) (typed FeaturePython)
  n = 0.336553
FEATURE [App::DocumentObjectGroupPython] Ca_element011  label="Ca_element : 0.107"  # scripted group (container) (typed FeaturePython)
  n = 0.107205
FEATURE [App::DocumentObjectGroupPython] G4_GLASS_PLATE  # scripted group (container) (typed FeaturePython)
  Dunit = g/cm3
  Dvalue = 2.4
  Group = -> [O_element045,Na_element009,Si_element005,Ca_element011]
  conduct = 2
  density = 1
  expand = 3
  formula = G4_GLASS_PLATE
  name = G4_GLASS_PLATE
  specific = 4
FEATURE [App::DocumentObjectGroupPython] C_element049  label="C_element : 026"  # scripted group (container) (typed FeaturePython)
  n = 5
  ref = C_element
FEATURE [App::DocumentObjectGroupPython] H_element042  label="H_element : 021"  # scripted group (container) (typed FeaturePython)
  n = 10
  ref = H_element
FEATURE [App::DocumentObjectGroupPython] N_element019  label="N_element : 2"  # scripted group (container) (typed FeaturePython)
  n = 2
  ref = N_element
FEATURE [App::DocumentObjectGroupPython] O_element046  label="O_element : 022"  # scripted group (container) (typed FeaturePython)
  n = 3
  ref = O_element
FEATURE [App::DocumentObjectGroupPython] G4_GLUTAMINE  # scripted group (container) (typed FeaturePython)
  Dunit = g/cm3
  Dvalue = 1.46
  Group = -> [C_element049,H_element042,N_element019,O_element046]
  conduct = 2
  density = 1
  expand = 3
  formula = G4_GLUTAMINE
  name = G4_GLUTAMINE
  specific = 4
FEATURE [App::DocumentObjectGroupPython] C_element050  label="C_element : 027"  # scripted group (container) (typed FeaturePython)
  n = 3
  ref = C_element
FEATURE [App::DocumentObjectGroupPython] H_element043  label="H_element : 022"  # scripted group (container) (typed FeaturePython)
  n = 8
  ref = H_element
FEATURE [App::DocumentObjectGroupPython] O_element047  label="O_element : 023"  # scripted group (container) (typed FeaturePython)
  n = 3
  ref = O_element
FEATURE [App::DocumentObjectGroupPython] G4_GLYCEROL  # scripted group (container) (typed FeaturePython)
  Dunit = g/cm3
  Dvalue = 1.2613
  Group = -> [C_element050,H_element043,O_element047]
  conduct = 2
  density = 1
  expand = 3
  formula = G4_GLYCEROL
  name = G4_GLYCEROL
  specific = 4
FEATURE [App::DocumentObjectGroupPython] C_element051  label="C_element : 028"  # scripted group (container) (typed FeaturePython)
  n = 5
  ref = C_element
FEATURE [App::DocumentObjectGroupPython] H_element044  label="H_element : 023"  # scripted group (container) (typed FeaturePython)
  n = 5
  ref = H_element
FEATURE [App::DocumentObjectGroupPython] N_element020  label="N_element : 009"  # scripted group (container) (typed FeaturePython)
  n = 5
  ref = N_element
FEATURE [App::DocumentObjectGroupPython] O_element048  label="O_element : 024"  # scripted group (container) (typed FeaturePython)
  n = 1
  ref = O_element
FEATURE [App::DocumentObjectGroupPython] G4_GUANINE  # scripted group (container) (typed FeaturePython)
  Dunit = g/cm3
  Dvalue = 2.2
  Group = -> [C_element051,H_element044,N_element020,O_element048]
  conduct = 2
  density = 1
  expand = 3
  formula = G4_GUANINE
  name = G4_GUANINE
  specific = 4
FEATURE [App::DocumentObjectGroupPython] Ca_element012  label="Ca_element : 006"  # scripted group (container) (typed FeaturePython)
  n = 1
  ref = Ca_element
FEATURE [App::DocumentObjectGroupPython] S_element014  label="S_element : 005"  # scripted group (container) (typed FeaturePython)
  n = 1
  ref = S_element
FEATURE [App::DocumentObjectGroupPython] O_element049  label="O_element : 6"  # scripted group (container) (typed FeaturePython)
  n = 6
  ref = O_element
FEATURE [App::DocumentObjectGroupPython] H_element045  label="H_element : 024"  # scripted group (container) (typed FeaturePython)
  n = 4
  ref = H_element
FEATURE [App::DocumentObjectGroupPython] G4_GYPSUM  # scripted group (container) (typed FeaturePython)
  Dunit = g/cm3
  Dvalue = 2.32
  Group = -> [Ca_element012,S_element014,O_element049,H_element045]
  conduct = 2
  density = 1
  expand = 3
  formula = G4_GYPSUM
  name = G4_GYPSUM
  specific = 4
FEATURE [App::DocumentObjectGroupPython] C_element052  label="C_element : 7"  # scripted group (container) (typed FeaturePython)
  n = 7
  ref = C_element
FEATURE [App::DocumentObjectGroupPython] H_element046  label="H_element : 16"  # scripted group (container) (typed FeaturePython)
  n = 16
  ref = H_element
FEATURE [App::DocumentObjectGroupPython] G4_N_HEPTANE  label="G4_N-HEPTANE"  # scripted group (container) (typed FeaturePython)
  Dunit = g/cm3
  Dvalue = 0.68376
  Group = -> [C_element052,H_element046]
  conduct = 2
  density = 1
  expand = 3
  formula = G4_N-HEPTANE
  name = G4_N-HEPTANE
  specific = 4
FEATURE [App::DocumentObjectGroupPython] C_element053  label="C_element : 029"  # scripted group (container) (typed FeaturePython)
  n = 6
  ref = C_element
FEATURE [App::DocumentObjectGroupPython] H_element047  label="H_element : 14"  # scripted group (container) (typed FeaturePython)
  n = 14
  ref = H_element
FEATURE [App::DocumentObjectGroupPython] G4_N_HEXANE  label="G4_N-HEXANE"  # scripted group (container) (typed FeaturePython)
  Dunit = g/cm3
  Dvalue = 0.6603
  Group = -> [C_element053,H_element047]
  conduct = 2
  density = 1
  expand = 3
  formula = G4_N-HEXANE
  name = G4_N-HEXANE
  specific = 4
FEATURE [App::DocumentObjectGroupPython] C_element054  label="C_element : 22"  # scripted group (container) (typed FeaturePython)
  n = 22
  ref = C_element
FEATURE [App::DocumentObjectGroupPython] H_element048  label="H_element : 025"  # scripted group (container) (typed FeaturePython)
  n = 10
  ref = H_element
FEATURE [App::DocumentObjectGroupPython] N_element021  label="N_element : 010"  # scripted group (container) (typed FeaturePython)
  n = 2
  ref = N_element
FEATURE [App::DocumentObjectGroupPython] O_element050  label="O_element : 025"  # scripted group (container) (typed FeaturePython)
  n = 5
  ref = O_element
FEATURE [App::DocumentObjectGroupPython] G4_KAPTON  # scripted group (container) (typed FeaturePython)
  Dunit = g/cm3
  Dvalue = 1.42
  Group = -> [C_element054,H_element048,N_element021,O_element050]
  conduct = 2
  density = 1
  expand = 3
  formula = G4_KAPTON
  name = G4_KAPTON
  specific = 4
FEATURE [App::DocumentObjectGroupPython] La_element001  label="La_element : 1"  # scripted group (container) (typed FeaturePython)
  n = 1
  ref = La_element
FEATURE [App::DocumentObjectGroupPython] Br_element003  label="Br_element : 002"  # scripted group (container) (typed FeaturePython)
  n = 1
  ref = Br_element
FEATURE [App::DocumentObjectGroupPython] O_element051  label="O_element : 026"  # scripted group (container) (typed FeaturePython)
  n = 1
  ref = O_element
FEATURE [App::DocumentObjectGroupPython] G4_LANTHANUM_OXYBROMIDE  # scripted group (container) (typed FeaturePython)
  Dunit = g/cm3
  Dvalue = 6.28
  Group = -> [La_element001,Br_element003,O_element051]
  conduct = 2
  density = 1
  expand = 3
  formula = G4_LANTHANUM_OXYBROMIDE
  name = G4_LANTHANUM_OXYBROMIDE
  specific = 4
FEATURE [App::DocumentObjectGroupPython] La_element002  label="La_element : 2"  # scripted group (container) (typed FeaturePython)
  n = 2
  ref = La_element
FEATURE [App::DocumentObjectGroupPython] O_element052  label="O_element : 027"  # scripted group (container) (typed FeaturePython)
  n = 2
  ref = O_element
FEATURE [App::DocumentObjectGroupPython] S_element015  label="S_element : 006"  # scripted group (container) (typed FeaturePython)
  n = 1
  ref = S_element
FEATURE [App::DocumentObjectGroupPython] G4_LANTHANUM_OXYSULFIDE  # scripted group (container) (typed FeaturePython)
  Dunit = g/cm3
  Dvalue = 5.86
  Group = -> [La_element002,O_element052,S_element015]
  conduct = 2
  density = 1
  expand = 3
  formula = G4_LANTHANUM_OXYSULFIDE
  name = G4_LANTHANUM_OXYSULFIDE
  specific = 4
FEATURE [App::DocumentObjectGroupPython] O_element053  label="O_element : 0.072"  # scripted group (container) (typed FeaturePython)
  n = 0.071682
FEATURE [App::DocumentObjectGroupPython] Pb_element002  label="Pb_element : 0.928"  # scripted group (container) (typed FeaturePython)
  n = 0.928318
FEATURE [App::DocumentObjectGroupPython] G4_LEAD_OXIDE  # scripted group (container) (typed FeaturePython)
  Dunit = g/cm3
  Dvalue = 9.53
  Group = -> [O_element053,Pb_element002]
  conduct = 2
  density = 1
  expand = 3
  formula = G4_LEAD_OXIDE
  name = G4_LEAD_OXIDE
  specific = 4
FEATURE [App::DocumentObjectGroupPython] Li_element001  label="Li_element : 1"  # scripted group (container) (typed FeaturePython)
  n = 1
  ref = Li_element
FEATURE [App::DocumentObjectGroupPython] N_element022  label="N_element : 011"  # scripted group (container) (typed FeaturePython)
  n = 1
  ref = N_element
FEATURE [App::DocumentObjectGroupPython] H_element049  label="H_element : 026"  # scripted group (container) (typed FeaturePython)
  n = 2
  ref = H_element
FEATURE [App::DocumentObjectGroupPython] G4_LITHIUM_AMIDE  # scripted group (container) (typed FeaturePython)
  Dunit = g/cm3
  Dvalue = 1.178
  Group = -> [Li_element001,N_element022,H_element049]
  conduct = 2
  density = 1
  expand = 3
  formula = G4_LITHIUM_AMIDE
  name = G4_LITHIUM_AMIDE
  specific = 4
FEATURE [App::DocumentObjectGroupPython] Li_element002  label="Li_element : 2"  # scripted group (container) (typed FeaturePython)
  n = 2
  ref = Li_element
FEATURE [App::DocumentObjectGroupPython] C_element055  label="C_element : 030"  # scripted group (container) (typed FeaturePython)
  n = 1
  ref = C_element
FEATURE [App::DocumentObjectGroupPython] O_element054  label="O_element : 028"  # scripted group (container) (typed FeaturePython)
  n = 3
  ref = O_element
FEATURE [App::DocumentObjectGroupPython] G4_LITHIUM_CARBONATE  # scripted group (container) (typed FeaturePython)
  Dunit = g/cm3
  Dvalue = 2.11
  Group = -> [Li_element002,C_element055,O_element054]
  conduct = 2
  density = 1
  expand = 3
  formula = G4_LITHIUM_CARBONATE
  name = G4_LITHIUM_CARBONATE
  specific = 4
FEATURE [App::DocumentObjectGroupPython] Li_element003  label="Li_element : 003"  # scripted group (container) (typed FeaturePython)
  n = 1
  ref = Li_element
FEATURE [App::DocumentObjectGroupPython] F_element012  label="F_element : 004"  # scripted group (container) (typed FeaturePython)
  n = 1
  ref = F_element
FEATURE [App::DocumentObjectGroupPython] G4_LITHIUM_FLUORIDE  # scripted group (container) (typed FeaturePython)
  Dunit = g/cm3
  Dvalue = 2.635
  Group = -> [Li_element003,F_element012]
  conduct = 2
  density = 1
  expand = 3
  formula = G4_LITHIUM_FLUORIDE
  name = G4_LITHIUM_FLUORIDE
  specific = 4
FEATURE [App::DocumentObjectGroupPython] Li_element004  label="Li_element : 004"  # scripted group (container) (typed FeaturePython)
  n = 1
  ref = Li_element
FEATURE [App::DocumentObjectGroupPython] H_element050  label="H_element : 027"  # scripted group (container) (typed FeaturePython)
  n = 1
  ref = H_element
FEATURE [App::DocumentObjectGroupPython] G4_LITHIUM_HYDRIDE  # scripted group (container) (typed FeaturePython)
  Dunit = g/cm3
  Dvalue = 0.82
  Group = -> [Li_element004,H_element050]
  conduct = 2
  density = 1
  expand = 3
  formula = G4_LITHIUM_HYDRIDE
  name = G4_LITHIUM_HYDRIDE
  specific = 4
FEATURE [App::DocumentObjectGroupPython] Li_element005  label="Li_element : 005"  # scripted group (container) (typed FeaturePython)
  n = 1
  ref = Li_element
FEATURE [App::DocumentObjectGroupPython] I_element003  label="I_element : 002"  # scripted group (container) (typed FeaturePython)
  n = 1
  ref = I_element
FEATURE [App::DocumentObjectGroupPython] G4_LITHIUM_IODIDE  # scripted group (container) (typed FeaturePython)
  Dunit = g/cm3
  Dvalue = 3.494
  Group = -> [Li_element005,I_element003]
  conduct = 2
  density = 1
  expand = 3
  formula = G4_LITHIUM_IODIDE
  name = G4_LITHIUM_IODIDE
  specific = 4
FEATURE [App::DocumentObjectGroupPython] Li_element006  label="Li_element : 006"  # scripted group (container) (typed FeaturePython)
  n = 2
  ref = Li_element
FEATURE [App::DocumentObjectGroupPython] O_element055  label="O_element : 029"  # scripted group (container) (typed FeaturePython)
  n = 1
  ref = O_element
FEATURE [App::DocumentObjectGroupPython] G4_LITHIUM_OXIDE  # scripted group (container) (typed FeaturePython)
  Dunit = g/cm3
  Dvalue = 2.013
  Group = -> [Li_element006,O_element055]
  conduct = 2
  density = 1
  expand = 3
  formula = G4_LITHIUM_OXIDE
  name = G4_LITHIUM_OXIDE
  specific = 4
FEATURE [App::DocumentObjectGroupPython] Li_element007  label="Li_element : 007"  # scripted group (container) (typed FeaturePython)
  n = 2
  ref = Li_element
FEATURE [App::DocumentObjectGroupPython] B_element005  label="B_element : 005"  # scripted group (container) (typed FeaturePython)
  n = 4
  ref = B_element
FEATURE [App::DocumentObjectGroupPython] O_element056  label="O_element : 7"  # scripted group (container) (typed FeaturePython)
  n = 7
  ref = O_element
FEATURE [App::DocumentObjectGroupPython] G4_LITHIUM_TETRABORATE  # scripted group (container) (typed FeaturePython)
  Dunit = g/cm3
  Dvalue = 2.44
  Group = -> [Li_element007,B_element005,O_element056]
  conduct = 2
  density = 1
  expand = 3
  formula = G4_LITHIUM_TETRABORATE
  name = G4_LITHIUM_TETRABORATE
  specific = 4
FEATURE [App::DocumentObjectGroupPython] H_element051  label="H_element : 0.105"  # scripted group (container) (typed FeaturePython)
  n = 0.105
FEATURE [App::DocumentObjectGroupPython] C_element056  label="C_element : 0.083"  # scripted group (container) (typed FeaturePython)
  n = 0.083
FEATURE [App::DocumentObjectGroupPython] N_element023  label="N_element : 0.023"  # scripted group (container) (typed FeaturePython)
  n = 0.023
FEATURE [App::DocumentObjectGroupPython] O_element057  label="O_element : 0.779"  # scripted group (container) (typed FeaturePython)
  n = 0.779
FEATURE [App::DocumentObjectGroupPython] Na_element010  label="Na_element : 0.097"  # scripted group (container) (typed FeaturePython)
  n = 0.002
FEATURE [App::DocumentObjectGroupPython] P_element006  label="P_element : 0.105"  # scripted group (container) (typed FeaturePython)
  n = 0.001
FEATURE [App::DocumentObjectGroupPython] S_element016  label="S_element : 0.017"  # scripted group (container) (typed FeaturePython)
  n = 0.002
FEATURE [App::DocumentObjectGroupPython] Cl_element014  label="Cl_element : 0.587"  # scripted group (container) (typed FeaturePython)
  n = 0.003
FEATURE [App::DocumentObjectGroupPython] K_element005  label="K_element : 0.015"  # scripted group (container) (typed FeaturePython)
  n = 0.002
FEATURE [App::DocumentObjectGroupPython] G4_LUNG_ICRP  # scripted group (container) (typed FeaturePython)
  Dunit = g/cm3
  Dvalue = 1.04
  Group = -> [H_element051,C_element056,N_element023,O_element057,Na_element010,P_element006,S_element016,Cl_element014,K_element005]
  conduct = 2
  density = 1
  expand = 3
  formula = G4_LUNG_ICRP
  name = G4_LUNG_ICRP
  specific = 4
FEATURE [App::DocumentObjectGroupPython] H_element052  label="H_element : 0.116"  # scripted group (container) (typed FeaturePython)
  n = 0.114318
FEATURE [App::DocumentObjectGroupPython] C_element057  label="C_element : 0.656"  # scripted group (container) (typed FeaturePython)
  n = 0.655824
FEATURE [App::DocumentObjectGroupPython] O_element058  label="O_element : 0.092"  # scripted group (container) (typed FeaturePython)
  n = 0.0921831
FEATURE [App::DocumentObjectGroupPython] Mg_element004  label="Mg_element : 0.135"  # scripted group (container) (typed FeaturePython)
  n = 0.134792
FEATURE [App::DocumentObjectGroupPython] Ca_element013  label="Ca_element : 0.003"  # scripted group (container) (typed FeaturePython)
  n = 0.002883
FEATURE [App::DocumentObjectGroupPython] G4_M3_WAX  # scripted group (container) (typed FeaturePython)
  Dunit = g/cm3
  Dvalue = 1.05
  Group = -> [H_element052,C_element057,O_element058,Mg_element004,Ca_element013]
  conduct = 2
  density = 1
  expand = 3
  formula = G4_M3_WAX
  name = G4_M3_WAX
  specific = 4
FEATURE [App::DocumentObjectGroupPython] Mg_element005  label="Mg_element : 1"  # scripted group (container) (typed FeaturePython)
  n = 1
  ref = Mg_element
FEATURE [App::DocumentObjectGroupPython] C_element058  label="C_element : 031"  # scripted group (container) (typed FeaturePython)
  n = 1
  ref = C_element
FEATURE [App::DocumentObjectGroupPython] O_element059  label="O_element : 030"  # scripted group (container) (typed FeaturePython)
  n = 3
  ref = O_element
FEATURE [App::DocumentObjectGroupPython] G4_MAGNESIUM_CARBONATE  # scripted group (container) (typed FeaturePython)
  Dunit = g/cm3
  Dvalue = 2.958
  Group = -> [Mg_element005,C_element058,O_element059]
  conduct = 2
  density = 1
  expand = 3
  formula = G4_MAGNESIUM_CARBONATE
  name = G4_MAGNESIUM_CARBONATE
  specific = 4
FEATURE [App::DocumentObjectGroupPython] Mg_element006  label="Mg_element : 002"  # scripted group (container) (typed FeaturePython)
  n = 1
  ref = Mg_element
FEATURE [App::DocumentObjectGroupPython] F_element013  label="F_element : 005"  # scripted group (container) (typed FeaturePython)
  n = 2
  ref = F_element
FEATURE [App::DocumentObjectGroupPython] G4_MAGNESIUM_FLUORIDE  # scripted group (container) (typed FeaturePython)
  Dunit = g/cm3
  Dvalue = 3
  Group = -> [Mg_element006,F_element013]
  conduct = 2
  density = 1
  expand = 3
  formula = G4_MAGNESIUM_FLUORIDE
  name = G4_MAGNESIUM_FLUORIDE
  specific = 4
FEATURE [App::DocumentObjectGroupPython] Mg_element007  label="Mg_element : 003"  # scripted group (container) (typed FeaturePython)
  n = 1
  ref = Mg_element
FEATURE [App::DocumentObjectGroupPython] O_element060  label="O_element : 031"  # scripted group (container) (typed FeaturePython)
  n = 1
  ref = O_element
FEATURE [App::DocumentObjectGroupPython] G4_MAGNESIUM_OXIDE  # scripted group (container) (typed FeaturePython)
  Dunit = g/cm3
  Dvalue = 3.58
  Group = -> [Mg_element007,O_element060]
  conduct = 2
  density = 1
  expand = 3
  formula = G4_MAGNESIUM_OXIDE
  name = G4_MAGNESIUM_OXIDE
  specific = 4
FEATURE [App::DocumentObjectGroupPython] Mg_element008  label="Mg_element : 004"  # scripted group (container) (typed FeaturePython)
  n = 1
  ref = Mg_element
FEATURE [App::DocumentObjectGroupPython] B_element006  label="B_element : 006"  # scripted group (container) (typed FeaturePython)
  n = 4
  ref = B_element
FEATURE [App::DocumentObjectGroupPython] O_element061  label="O_element : 032"  # scripted group (container) (typed FeaturePython)
  n = 7
  ref = O_element
FEATURE [App::DocumentObjectGroupPython] G4_MAGNESIUM_TETRABORATE  # scripted group (container) (typed FeaturePython)
  Dunit = g/cm3
  Dvalue = 2.53
  Group = -> [Mg_element008,B_element006,O_element061]
  conduct = 2
  density = 1
  expand = 3
  formula = G4_MAGNESIUM_TETRABORATE
  name = G4_MAGNESIUM_TETRABORATE
  specific = 4
FEATURE [App::DocumentObjectGroupPython] Hg_element001  label="Hg_element : 1"  # scripted group (container) (typed FeaturePython)
  n = 1
  ref = Hg_element
FEATURE [App::DocumentObjectGroupPython] I_element004  label="I_element : 2"  # scripted group (container) (typed FeaturePython)
  n = 2
  ref = I_element
FEATURE [App::DocumentObjectGroupPython] G4_MERCURIC_IODIDE  # scripted group (container) (typed FeaturePython)
  Dunit = g/cm3
  Dvalue = 6.36
  Group = -> [Hg_element001,I_element004]
  conduct = 2
  density = 1
  expand = 3
  formula = G4_MERCURIC_IODIDE
  name = G4_MERCURIC_IODIDE
  specific = 4
FEATURE [App::DocumentObjectGroupPython] C_element059  label="C_element : 032"  # scripted group (container) (typed FeaturePython)
  n = 1
  ref = C_element
FEATURE [App::DocumentObjectGroupPython] H_element053  label="H_element : 028"  # scripted group (container) (typed FeaturePython)
  n = 4
  ref = H_element
FEATURE [App::DocumentObjectGroupPython] G4_METHANE  # scripted group (container) (typed FeaturePython)
  Dunit = g/cm3
  Dvalue = 0.000667151
  Group = -> [C_element059,H_element053]
  conduct = 2
  density = 1
  expand = 3
  formula = G4_METHANE
  name = G4_METHANE
  specific = 4
FEATURE [App::DocumentObjectGroupPython] C_element060  label="C_element : 033"  # scripted group (container) (typed FeaturePython)
  n = 1
  ref = C_element
FEATURE [App::DocumentObjectGroupPython] H_element054  label="H_element : 029"  # scripted group (container) (typed FeaturePython)
  n = 4
  ref = H_element
FEATURE [App::DocumentObjectGroupPython] O_element062  label="O_element : 033"  # scripted group (container) (typed FeaturePython)
  n = 1
  ref = O_element
FEATURE [App::DocumentObjectGroupPython] G4_METHANOL  # scripted group (container) (typed FeaturePython)
  Dunit = g/cm3
  Dvalue = 0.7914
  Group = -> [C_element060,H_element054,O_element062]
  conduct = 2
  density = 1
  expand = 3
  formula = G4_METHANOL
  name = G4_METHANOL
  specific = 4
FEATURE [App::DocumentObjectGroupPython] H_element055  label="H_element : 0.134"  # scripted group (container) (typed FeaturePython)
  n = 0.13404
FEATURE [App::DocumentObjectGroupPython] C_element061  label="C_element : 0.778"  # scripted group (container) (typed FeaturePython)
  n = 0.77796
FEATURE [App::DocumentObjectGroupPython] O_element063  label="O_element : 0.035"  # scripted group (container) (typed FeaturePython)
  n = 0.03502
FEATURE [App::DocumentObjectGroupPython] Mg_element009  label="Mg_element : 0.039"  # scripted group (container) (typed FeaturePython)
  n = 0.038594
FEATURE [App::DocumentObjectGroupPython] Ti_element002  label="Ti_element : 0.014"  # scripted group (container) (typed FeaturePython)
  n = 0.014386
FEATURE [App::DocumentObjectGroupPython] G4_MIX_D_WAX  # scripted group (container) (typed FeaturePython)
  Dunit = g/cm3
  Dvalue = 0.99
  Group = -> [H_element055,C_element061,O_element063,Mg_element009,Ti_element002]
  conduct = 2
  density = 1
  expand = 3
  formula = G4_MIX_D_WAX
  name = G4_MIX_D_WAX
  specific = 4
FEATURE [App::DocumentObjectGroupPython] H_element056  label="H_element : 0.135"  # scripted group (container) (typed FeaturePython)
  n = 0.081192
FEATURE [App::DocumentObjectGroupPython] C_element062  label="C_element : 0.583"  # scripted group (container) (typed FeaturePython)
  n = 0.583442
FEATURE [App::DocumentObjectGroupPython] N_element024  label="N_element : 0.018"  # scripted group (container) (typed FeaturePython)
  n = 0.017798
FEATURE [App::DocumentObjectGroupPython] O_element064  label="O_element : 0.186"  # scripted group (container) (typed FeaturePython)
  n = 0.186381
FEATURE [App::DocumentObjectGroupPython] Mg_element010  label="Mg_element : 0.130"  # scripted group (container) (typed FeaturePython)
  n = 0.130287
FEATURE [App::DocumentObjectGroupPython] Cl_element015  label="Cl_element : 0.588"  # scripted group (container) (typed FeaturePython)
  n = 0.0009
FEATURE [App::DocumentObjectGroupPython] G4_MS20_TISSUE  # scripted group (container) (typed FeaturePython)
  Dunit = g/cm3
  Dvalue = 1
  Group = -> [H_element056,C_element062,N_element024,O_element064,Mg_element010,Cl_element015]
  conduct = 2
  density = 1
  expand = 3
  formula = G4_MS20_TISSUE
  name = G4_MS20_TISSUE
  specific = 4
FEATURE [App::DocumentObjectGroupPython] H_element057  label="H_element : 0.136"  # scripted group (container) (typed FeaturePython)
  n = 0.102
FEATURE [App::DocumentObjectGroupPython] C_element063  label="C_element : 0.143"  # scripted group (container) (typed FeaturePython)
  n = 0.143
FEATURE [App::DocumentObjectGroupPython] N_element025  label="N_element : 0.034"  # scripted group (container) (typed FeaturePython)
  n = 0.034
FEATURE [App::DocumentObjectGroupPython] O_element065  label="O_element : 0.710"  # scripted group (container) (typed FeaturePython)
  n = 0.71
FEATURE [App::DocumentObjectGroupPython] Na_element011  label="Na_element : 0.098"  # scripted group (container) (typed FeaturePython)
  n = 0.001
FEATURE [App::DocumentObjectGroupPython] P_element007  label="P_element : 0.002"  # scripted group (container) (typed FeaturePython)
  n = 0.002
FEATURE [App::DocumentObjectGroupPython] S_element017  label="S_element : 0.018"  # scripted group (container) (typed FeaturePython)
  n = 0.003
FEATURE [App::DocumentObjectGroupPython] Cl_element016  label="Cl_element : 0.589"  # scripted group (container) (typed FeaturePython)
  n = 0.001
FEATURE [App::DocumentObjectGroupPython] K_element006  label="K_element : 0.004"  # scripted group (container) (typed FeaturePython)
  n = 0.004
FEATURE [App::DocumentObjectGroupPython] G4_MUSCLE_SKELETAL_ICRP  # scripted group (container) (typed FeaturePython)
  Dunit = g/cm3
  Dvalue = 1.05
  Group = -> [H_element057,C_element063,N_element025,O_element065,Na_element011,P_element007,S_element017,Cl_element016,K_element006]
  conduct = 2
  density = 1
  expand = 3
  formula = G4_MUSCLE_SKELETAL_ICRP
  name = G4_MUSCLE_SKELETAL_ICRP
  specific = 4
FEATURE [App::DocumentObjectGroupPython] H_element058  label="H_element : 0.137"  # scripted group (container) (typed FeaturePython)
  n = 0.102102
FEATURE [App::DocumentObjectGroupPython] C_element064  label="C_element : 0.123"  # scripted group (container) (typed FeaturePython)
  n = 0.123123
FEATURE [App::DocumentObjectGroupPython] N_element026  label="N_element : 0.756"  # scripted group (container) (typed FeaturePython)
  n = 0.035035
FEATURE [App::DocumentObjectGroupPython] O_element066  label="O_element : 0.730"  # scripted group (container) (typed FeaturePython)
  n = 0.72973
FEATURE [App::DocumentObjectGroupPython] Na_element012  label="Na_element : 0.099"  # scripted group (container) (typed FeaturePython)
  n = 0.001001
FEATURE [App::DocumentObjectGroupPython] P_element008  label="P_element : 0.106"  # scripted group (container) (typed FeaturePython)
  n = 0.002002
FEATURE [App::DocumentObjectGroupPython] S_element018  label="S_element : 0.019"  # scripted group (container) (typed FeaturePython)
  n = 0.004004
FEATURE [App::DocumentObjectGroupPython] K_element007  label="K_element : 0.016"  # scripted group (container) (typed FeaturePython)
  n = 0.003003
FEATURE [App::DocumentObjectGroupPython] G4_MUSCLE_STRIATED_ICRU  # scripted group (container) (typed FeaturePython)
  Dunit = g/cm3
  Dvalue = 1.04
  Group = -> [H_element058,C_element064,N_element026,O_element066,Na_element012,P_element008,S_element018,K_element007]
  conduct = 2
  density = 1
  expand = 3
  formula = G4_MUSCLE_STRIATED_ICRU
  name = G4_MUSCLE_STRIATED_ICRU
  specific = 4
FEATURE [App::DocumentObjectGroupPython] H_element059  label="H_element : 0.098"  # scripted group (container) (typed FeaturePython)
  n = 0.0982341
FEATURE [App::DocumentObjectGroupPython] C_element065  label="C_element : 0.156"  # scripted group (container) (typed FeaturePython)
  n = 0.156214
FEATURE [App::DocumentObjectGroupPython] N_element027  label="N_element : 0.757"  # scripted group (container) (typed FeaturePython)
  n = 0.035451
FEATURE [App::DocumentObjectGroupPython] O_element067  label="O_element : 0.880"  # scripted group (container) (typed FeaturePython)
  n = 0.710101
FEATURE [App::DocumentObjectGroupPython] G4_MUSCLE_WITH_SUCROSE  # scripted group (container) (typed FeaturePython)
  Dunit = g/cm3
  Dvalue = 1.11
  Group = -> [H_element059,C_element065,N_element027,O_element067]
  conduct = 2
  density = 1
  expand = 3
  formula = G4_MUSCLE_WITH_SUCROSE
  name = G4_MUSCLE_WITH_SUCROSE
  specific = 4
FEATURE [App::DocumentObjectGroupPython] H_element060  label="H_element : 0.138"  # scripted group (container) (typed FeaturePython)
  n = 0.101969
FEATURE [App::DocumentObjectGroupPython] C_element066  label="C_element : 0.120"  # scripted group (container) (typed FeaturePython)
  n = 0.120058
FEATURE [App::DocumentObjectGroupPython] N_element028  label="N_element : 0.758"  # scripted group (container) (typed FeaturePython)
  n = 0.035451
FEATURE [App::DocumentObjectGroupPython] O_element068  label="O_element : 0.743"  # scripted group (container) (typed FeaturePython)
  n = 0.742522
FEATURE [App::DocumentObjectGroupPython] G4_MUSCLE_WITHOUT_SUCROSE  # scripted group (container) (typed FeaturePython)
  Dunit = g/cm3
  Dvalue = 1.07
  Group = -> [H_element060,C_element066,N_element028,O_element068]
  conduct = 2
  density = 1
  expand = 3
  formula = G4_MUSCLE_WITHOUT_SUCROSE
  name = G4_MUSCLE_WITHOUT_SUCROSE
  specific = 4
FEATURE [App::DocumentObjectGroupPython] C_element067  label="C_element : 10"  # scripted group (container) (typed FeaturePython)
  n = 10
  ref = C_element
FEATURE [App::DocumentObjectGroupPython] H_element061  label="H_element : 030"  # scripted group (container) (typed FeaturePython)
  n = 8
  ref = H_element
FEATURE [App::DocumentObjectGroupPython] G4_NAPHTHALENE  # scripted group (container) (typed FeaturePython)
  Dunit = g/cm3
  Dvalue = 1.145
  Group = -> [C_element067,H_element061]
  conduct = 2
  density = 1
  expand = 3
  formula = G4_NAPHTHALENE
  name = G4_NAPHTHALENE
  specific = 4
FEATURE [App::DocumentObjectGroupPython] C_element068  label="C_element : 034"  # scripted group (container) (typed FeaturePython)
  n = 6
  ref = C_element
FEATURE [App::DocumentObjectGroupPython] H_element062  label="H_element : 031"  # scripted group (container) (typed FeaturePython)
  n = 5
  ref = H_element
FEATURE [App::DocumentObjectGroupPython] N_element029  label="N_element : 012"  # scripted group (container) (typed FeaturePython)
  n = 1
  ref = N_element
FEATURE [App::DocumentObjectGroupPython] O_element069  label="O_element : 034"  # scripted group (container) (typed FeaturePython)
  n = 2
  ref = O_element
FEATURE [App::DocumentObjectGroupPython] G4_NITROBENZENE  # scripted group (container) (typed FeaturePython)
  Dunit = g/cm3
  Dvalue = 1.19867
  Group = -> [C_element068,H_element062,N_element029,O_element069]
  conduct = 2
  density = 1
  expand = 3
  formula = G4_NITROBENZENE
  name = G4_NITROBENZENE
  specific = 4
FEATURE [App::DocumentObjectGroupPython] N_element030  label="N_element : 013"  # scripted group (container) (typed FeaturePython)
  n = 2
  ref = N_element
FEATURE [App::DocumentObjectGroupPython] O_element070  label="O_element : 035"  # scripted group (container) (typed FeaturePython)
  n = 1
  ref = O_element
FEATURE [App::DocumentObjectGroupPython] G4_NITROUS_OXIDE  # scripted group (container) (typed FeaturePython)
  Dunit = g/cm3
  Dvalue = 0.00183094
  Group = -> [N_element030,O_element070]
  conduct = 2
  density = 1
  expand = 3
  formula = G4_NITROUS_OXIDE
  name = G4_NITROUS_OXIDE
  specific = 4
FEATURE [App::DocumentObjectGroupPython] H_element063  label="H_element : 0.104"  # scripted group (container) (typed FeaturePython)
  n = 0.103509
FEATURE [App::DocumentObjectGroupPython] C_element069  label="C_element : 0.648"  # scripted group (container) (typed FeaturePython)
  n = 0.648416
FEATURE [App::DocumentObjectGroupPython] N_element031  label="N_element : 0.100"  # scripted group (container) (typed FeaturePython)
  n = 0.0995361
FEATURE [App::DocumentObjectGroupPython] O_element071  label="O_element : 0.149"  # scripted group (container) (typed FeaturePython)
  n = 0.148539
FEATURE [App::DocumentObjectGroupPython] G4_NYLON_8062  label="G4_NYLON-8062"  # scripted group (container) (typed FeaturePython)
  Dunit = g/cm3
  Dvalue = 1.08
  Group = -> [H_element063,C_element069,N_element031,O_element071]
  conduct = 2
  density = 1
  expand = 3
  formula = G4_NYLON-8062
  name = G4_NYLON-8062
  specific = 4
FEATURE [App::DocumentObjectGroupPython] C_element070  label="C_element : 035"  # scripted group (container) (typed FeaturePython)
  n = 6
  ref = C_element
FEATURE [App::DocumentObjectGroupPython] H_element064  label="H_element : 11"  # scripted group (container) (typed FeaturePython)
  n = 11
  ref = H_element
FEATURE [App::DocumentObjectGroupPython] N_element032  label="N_element : 014"  # scripted group (container) (typed FeaturePython)
  n = 1
  ref = N_element
FEATURE [App::DocumentObjectGroupPython] O_element072  label="O_element : 036"  # scripted group (container) (typed FeaturePython)
  n = 1
  ref = O_element
FEATURE [App::DocumentObjectGroupPython] G4_NYLON_6_6  label="G4_NYLON-6-6"  # scripted group (container) (typed FeaturePython)
  Dunit = g/cm3
  Dvalue = 1.14
  Group = -> [C_element070,H_element064,N_element032,O_element072]
  conduct = 2
  density = 1
  expand = 3
  formula = G4_NYLON-6-6
  name = G4_NYLON-6-6
  specific = 4
FEATURE [App::DocumentObjectGroupPython] H_element065  label="H_element : 0.139"  # scripted group (container) (typed FeaturePython)
  n = 0.107062
FEATURE [App::DocumentObjectGroupPython] C_element071  label="C_element : 0.680"  # scripted group (container) (typed FeaturePython)
  n = 0.680449
FEATURE [App::DocumentObjectGroupPython] N_element033  label="N_element : 0.099"  # scripted group (container) (typed FeaturePython)
  n = 0.099189
FEATURE [App::DocumentObjectGroupPython] O_element073  label="O_element : 0.113"  # scripted group (container) (typed FeaturePython)
  n = 0.1133
FEATURE [App::DocumentObjectGroupPython] G4_NYLON_6_10  label="G4_NYLON-6-10"  # scripted group (container) (typed FeaturePython)
  Dunit = g/cm3
  Dvalue = 1.14
  Group = -> [H_element065,C_element071,N_element033,O_element073]
  conduct = 2
  density = 1
  expand = 3
  formula = G4_NYLON-6-10
  name = G4_NYLON-6-10
  specific = 4
FEATURE [App::DocumentObjectGroupPython] H_element066  label="H_element : 0.140"  # scripted group (container) (typed FeaturePython)
  n = 0.115476
FEATURE [App::DocumentObjectGroupPython] C_element072  label="C_element : 0.721"  # scripted group (container) (typed FeaturePython)
  n = 0.720818
FEATURE [App::DocumentObjectGroupPython] N_element034  label="N_element : 0.076"  # scripted group (container) (typed FeaturePython)
  n = 0.0764169
FEATURE [App::DocumentObjectGroupPython] O_element074  label="O_element : 0.087"  # scripted group (container) (typed FeaturePython)
  n = 0.0872889
FEATURE [App::DocumentObjectGroupPython] G4_NYLON_11_RILSAN  label="G4_NYLON-11_RILSAN"  # scripted group (container) (typed FeaturePython)
  Dunit = g/cm3
  Dvalue = 1.425
  Group = -> [H_element066,C_element072,N_element034,O_element074]
  conduct = 2
  density = 1
  expand = 3
  formula = G4_NYLON-11_RILSAN
  name = G4_NYLON-11_RILSAN
  specific = 4
FEATURE [App::DocumentObjectGroupPython] C_element073  label="C_element : 8"  # scripted group (container) (typed FeaturePython)
  n = 8
  ref = C_element
FEATURE [App::DocumentObjectGroupPython] H_element067  label="H_element : 18"  # scripted group (container) (typed FeaturePython)
  n = 18
  ref = H_element
FEATURE [App::DocumentObjectGroupPython] G4_OCTANE  # scripted group (container) (typed FeaturePython)
  Dunit = g/cm3
  Dvalue = 0.7026
  Group = -> [C_element073,H_element067]
  conduct = 2
  density = 1
  expand = 3
  formula = G4_OCTANE
  name = G4_OCTANE
  specific = 4
FEATURE [App::DocumentObjectGroupPython] C_element074  label="C_element : 25"  # scripted group (container) (typed FeaturePython)
  n = 25
  ref = C_element
FEATURE [App::DocumentObjectGroupPython] H_element068  label="H_element : 52"  # scripted group (container) (typed FeaturePython)
  n = 52
  ref = H_element
FEATURE [App::DocumentObjectGroupPython] G4_PARAFFIN  # scripted group (container) (typed FeaturePython)
  Dunit = g/cm3
  Dvalue = 0.93
  Group = -> [C_element074,H_element068]
  conduct = 2
  density = 1
  expand = 3
  formula = G4_PARAFFIN
  name = G4_PARAFFIN
  specific = 4
FEATURE [App::DocumentObjectGroupPython] C_element075  label="C_element : 036"  # scripted group (container) (typed FeaturePython)
  n = 5
  ref = C_element
FEATURE [App::DocumentObjectGroupPython] H_element069  label="H_element : 032"  # scripted group (container) (typed FeaturePython)
  n = 12
  ref = H_element
FEATURE [App::DocumentObjectGroupPython] G4_N_PENTANE  label="G4_N-PENTANE"  # scripted group (container) (typed FeaturePython)
  Dunit = g/cm3
  Dvalue = 0.6262
  Group = -> [C_element075,H_element069]
  conduct = 2
  density = 1
  expand = 3
  formula = G4_N-PENTANE
  name = G4_N-PENTANE
  specific = 4
FEATURE [App::DocumentObjectGroupPython] H_element070  label="H_element : 0.014"  # scripted group (container) (typed FeaturePython)
  n = 0.0141
FEATURE [App::DocumentObjectGroupPython] C_element076  label="C_element : 0.072"  # scripted group (container) (typed FeaturePython)
  n = 0.072261
FEATURE [App::DocumentObjectGroupPython] N_element035  label="N_element : 0.019"  # scripted group (container) (typed FeaturePython)
  n = 0.01932
FEATURE [App::DocumentObjectGroupPython] O_element075  label="O_element : 0.066"  # scripted group (container) (typed FeaturePython)
  n = 0.066101
FEATURE [App::DocumentObjectGroupPython] S_element019  label="S_element : 0.020"  # scripted group (container) (typed FeaturePython)
  n = 0.00189
FEATURE [App::DocumentObjectGroupPython] Br_element004  label="Br_element : 0.349"  # scripted group (container) (typed FeaturePython)
  n = 0.349103
FEATURE [App::DocumentObjectGroupPython] Ag_element001  label="Ag_element : 0.474"  # scripted group (container) (typed FeaturePython)
  n = 0.474105
FEATURE [App::DocumentObjectGroupPython] I_element005  label="I_element : 0.003"  # scripted group (container) (typed FeaturePython)
  n = 0.00312
FEATURE [App::DocumentObjectGroupPython] G4_PHOTO_EMULSION  # scripted group (container) (typed FeaturePython)
  Dunit = g/cm3
  Dvalue = 3.815
  Group = -> [H_element070,C_element076,N_element035,O_element075,S_element019,Br_element004,Ag_element001,I_element005]
  conduct = 2
  density = 1
  expand = 3
  formula = G4_PHOTO_EMULSION
  name = G4_PHOTO_EMULSION
  specific = 4
FEATURE [App::DocumentObjectGroupPython] C_element077  label="C_element : 9"  # scripted group (container) (typed FeaturePython)
  n = 9
  ref = C_element
FEATURE [App::DocumentObjectGroupPython] H_element071  label="H_element : 033"  # scripted group (container) (typed FeaturePython)
  n = 10
  ref = H_element
FEATURE [App::DocumentObjectGroupPython] G4_PLASTIC_SC_VINYLTOLUENE  # scripted group (container) (typed FeaturePython)
  Dunit = g/cm3
  Dvalue = 1.032
  Group = -> [C_element077,H_element071]
  conduct = 2
  density = 1
  expand = 3
  formula = G4_PLASTIC_SC_VINYLTOLUENE
  name = G4_PLASTIC_SC_VINYLTOLUENE
  specific = 4
FEATURE [App::DocumentObjectGroupPython] Pu_element001  label="Pu_element : 1"  # scripted group (container) (typed FeaturePython)
  n = 1
  ref = Pu_element
FEATURE [App::DocumentObjectGroupPython] O_element076  label="O_element : 037"  # scripted group (container) (typed FeaturePython)
  n = 2
  ref = O_element
FEATURE [App::DocumentObjectGroupPython] G4_PLUTONIUM_DIOXIDE  # scripted group (container) (typed FeaturePython)
  Dunit = g/cm3
  Dvalue = 11.46
  Group = -> [Pu_element001,O_element076]
  conduct = 2
  density = 1
  expand = 3
  formula = G4_PLUTONIUM_DIOXIDE
  name = G4_PLUTONIUM_DIOXIDE
  specific = 4
FEATURE [App::DocumentObjectGroupPython] C_element078  label="C_element : 037"  # scripted group (container) (typed FeaturePython)
  n = 3
  ref = C_element
FEATURE [App::DocumentObjectGroupPython] H_element072  label="H_element : 034"  # scripted group (container) (typed FeaturePython)
  n = 3
  ref = H_element
FEATURE [App::DocumentObjectGroupPython] N_element036  label="N_element : 015"  # scripted group (container) (typed FeaturePython)
  n = 1
  ref = N_element
FEATURE [App::DocumentObjectGroupPython] G4_POLYACRYLONITRILE  # scripted group (container) (typed FeaturePython)
  Dunit = g/cm3
  Dvalue = 1.17
  Group = -> [C_element078,H_element072,N_element036]
  conduct = 2
  density = 1
  expand = 3
  formula = G4_POLYACRYLONITRILE
  name = G4_POLYACRYLONITRILE
  specific = 4
FEATURE [App::DocumentObjectGroupPython] C_element079  label="C_element : 16"  # scripted group (container) (typed FeaturePython)
  n = 16
  ref = C_element
FEATURE [App::DocumentObjectGroupPython] H_element073  label="H_element : 035"  # scripted group (container) (typed FeaturePython)
  n = 14
  ref = H_element
FEATURE [App::DocumentObjectGroupPython] O_element077  label="O_element : 038"  # scripted group (container) (typed FeaturePython)
  n = 3
  ref = O_element
FEATURE [App::DocumentObjectGroupPython] G4_POLYCARBONATE  # scripted group (container) (typed FeaturePython)
  Dunit = g/cm3
  Dvalue = 1.2
  Group = -> [C_element079,H_element073,O_element077]
  conduct = 2
  density = 1
  expand = 3
  formula = G4_POLYCARBONATE
  name = G4_POLYCARBONATE
  specific = 4
FEATURE [App::DocumentObjectGroupPython] C_element080  label="C_element : 038"  # scripted group (container) (typed FeaturePython)
  n = 8
  ref = C_element
FEATURE [App::DocumentObjectGroupPython] H_element074  label="H_element : 036"  # scripted group (container) (typed FeaturePython)
  n = 7
  ref = H_element
FEATURE [App::DocumentObjectGroupPython] Cl_element017  label="Cl_element : 007"  # scripted group (container) (typed FeaturePython)
  n = 1
  ref = Cl_element
FEATURE [App::DocumentObjectGroupPython] G4_POLYCHLOROSTYRENE  # scripted group (container) (typed FeaturePython)
  Dunit = g/cm3
  Dvalue = 1.3
  Group = -> [C_element080,H_element074,Cl_element017]
  conduct = 2
  density = 1
  expand = 3
  formula = G4_POLYCHLOROSTYRENE
  name = G4_POLYCHLOROSTYRENE
  specific = 4
FEATURE [App::DocumentObjectGroupPython] C_element081  label="C_element : 039"  # scripted group (container) (typed FeaturePython)
  n = 1
  ref = C_element
FEATURE [App::DocumentObjectGroupPython] H_element075  label="H_element : 037"  # scripted group (container) (typed FeaturePython)
  n = 2
  ref = H_element
FEATURE [App::DocumentObjectGroupPython] G4_POLYETHYLENE  # scripted group (container) (typed FeaturePython)
  Dunit = g/cm3
  Dvalue = 0.94
  Group = -> [C_element081,H_element075]
  conduct = 2
  density = 1
  expand = 3
  formula = G4_POLYETHYLENE
  name = G4_POLYETHYLENE
  specific = 4
FEATURE [App::DocumentObjectGroupPython] C_element082  label="C_element : 040"  # scripted group (container) (typed FeaturePython)
  n = 10
  ref = C_element
FEATURE [App::DocumentObjectGroupPython] H_element076  label="H_element : 038"  # scripted group (container) (typed FeaturePython)
  n = 8
  ref = H_element
FEATURE [App::DocumentObjectGroupPython] O_element078  label="O_element : 039"  # scripted group (container) (typed FeaturePython)
  n = 4
  ref = O_element
FEATURE [App::DocumentObjectGroupPython] G4_MYLAR  # scripted group (container) (typed FeaturePython)
  Dunit = g/cm3
  Dvalue = 1.4
  Group = -> [C_element082,H_element076,O_element078]
  conduct = 2
  density = 1
  expand = 3
  formula = G4_MYLAR
  name = G4_MYLAR
  specific = 4
FEATURE [App::DocumentObjectGroupPython] C_element083  label="C_element : 041"  # scripted group (container) (typed FeaturePython)
  n = 5
  ref = C_element
FEATURE [App::DocumentObjectGroupPython] H_element077  label="H_element : 039"  # scripted group (container) (typed FeaturePython)
  n = 8
  ref = H_element
FEATURE [App::DocumentObjectGroupPython] O_element079  label="O_element : 040"  # scripted group (container) (typed FeaturePython)
  n = 2
  ref = O_element
FEATURE [App::DocumentObjectGroupPython] G4_PLEXIGLASS  # scripted group (container) (typed FeaturePython)
  Dunit = g/cm3
  Dvalue = 1.19
  Group = -> [C_element083,H_element077,O_element079]
  conduct = 2
  density = 1
  expand = 3
  formula = G4_PLEXIGLASS
  name = G4_PLEXIGLASS
  specific = 4
FEATURE [App::DocumentObjectGroupPython] C_element084  label="C_element : 042"  # scripted group (container) (typed FeaturePython)
  n = 1
  ref = C_element
FEATURE [App::DocumentObjectGroupPython] H_element078  label="H_element : 040"  # scripted group (container) (typed FeaturePython)
  n = 2
  ref = H_element
FEATURE [App::DocumentObjectGroupPython] O_element080  label="O_element : 041"  # scripted group (container) (typed FeaturePython)
  n = 1
  ref = O_element
FEATURE [App::DocumentObjectGroupPython] G4_POLYOXYMETHYLENE  # scripted group (container) (typed FeaturePython)
  Dunit = g/cm3
  Dvalue = 1.425
  Group = -> [C_element084,H_element078,O_element080]
  conduct = 2
  density = 1
  expand = 3
  formula = G4_POLYOXYMETHYLENE
  name = G4_POLYOXYMETHYLENE
  specific = 4
FEATURE [App::DocumentObjectGroupPython] C_element085  label="C_element : 043"  # scripted group (container) (typed FeaturePython)
  n = 2
  ref = C_element
FEATURE [App::DocumentObjectGroupPython] H_element079  label="H_element : 041"  # scripted group (container) (typed FeaturePython)
  n = 4
  ref = H_element
FEATURE [App::DocumentObjectGroupPython] G4_POLYPROPYLENE  # scripted group (container) (typed FeaturePython)
  Dunit = g/cm3
  Dvalue = 0.9
  Group = -> [C_element085,H_element079]
  conduct = 2
  density = 1
  expand = 3
  formula = G4_POLYPROPYLENE
  name = G4_POLYPROPYLENE
  specific = 4
FEATURE [App::DocumentObjectGroupPython] C_element086  label="C_element : 044"  # scripted group (container) (typed FeaturePython)
  n = 8
  ref = C_element
FEATURE [App::DocumentObjectGroupPython] H_element080  label="H_element : 042"  # scripted group (container) (typed FeaturePython)
  n = 8
  ref = H_element
FEATURE [App::DocumentObjectGroupPython] G4_POLYSTYRENE  # scripted group (container) (typed FeaturePython)
  Dunit = g/cm3
  Dvalue = 1.06
  Group = -> [C_element086,H_element080]
  conduct = 2
  density = 1
  expand = 3
  formula = G4_POLYSTYRENE
  name = G4_POLYSTYRENE
  specific = 4
FEATURE [App::DocumentObjectGroupPython] C_element087  label="C_element : 045"  # scripted group (container) (typed FeaturePython)
  n = 2
  ref = C_element
FEATURE [App::DocumentObjectGroupPython] F_element014  label="F_element : 4"  # scripted group (container) (typed FeaturePython)
  n = 4
  ref = F_element
FEATURE [App::DocumentObjectGroupPython] G4_TEFLON  # scripted group (container) (typed FeaturePython)
  Dunit = g/cm3
  Dvalue = 2.2
  Group = -> [C_element087,F_element014]
  conduct = 2
  density = 1
  expand = 3
  formula = G4_TEFLON
  name = G4_TEFLON
  specific = 4
FEATURE [App::DocumentObjectGroupPython] C_element088  label="C_element : 046"  # scripted group (container) (typed FeaturePython)
  n = 2
  ref = C_element
FEATURE [App::DocumentObjectGroupPython] F_element015  label="F_element : 006"  # scripted group (container) (typed FeaturePython)
  n = 3
  ref = F_element
FEATURE [App::DocumentObjectGroupPython] Cl_element018  label="Cl_element : 008"  # scripted group (container) (typed FeaturePython)
  n = 1
  ref = Cl_element
FEATURE [App::DocumentObjectGroupPython] G4_POLYTRIFLUOROCHLOROETHYLENE  # scripted group (container) (typed FeaturePython)
  Dunit = g/cm3
  Dvalue = 2.1
  Group = -> [C_element088,F_element015,Cl_element018]
  conduct = 2
  density = 1
  expand = 3
  formula = G4_POLYTRIFLUOROCHLOROETHYLENE
  name = G4_POLYTRIFLUOROCHLOROETHYLENE
  specific = 4
FEATURE [App::DocumentObjectGroupPython] C_element089  label="C_element : 047"  # scripted group (container) (typed FeaturePython)
  n = 4
  ref = C_element
FEATURE [App::DocumentObjectGroupPython] H_element081  label="H_element : 043"  # scripted group (container) (typed FeaturePython)
  n = 6
  ref = H_element
FEATURE [App::DocumentObjectGroupPython] O_element081  label="O_element : 042"  # scripted group (container) (typed FeaturePython)
  n = 2
  ref = O_element
FEATURE [App::DocumentObjectGroupPython] G4_POLYVINYL_ACETATE  # scripted group (container) (typed FeaturePython)
  Dunit = g/cm3
  Dvalue = 1.19
  Group = -> [C_element089,H_element081,O_element081]
  conduct = 2
  density = 1
  expand = 3
  formula = G4_POLYVINYL_ACETATE
  name = G4_POLYVINYL_ACETATE
  specific = 4
FEATURE [App::DocumentObjectGroupPython] C_element090  label="C_element : 048"  # scripted group (container) (typed FeaturePython)
  n = 2
  ref = C_element
FEATURE [App::DocumentObjectGroupPython] H_element082  label="H_element : 044"  # scripted group (container) (typed FeaturePython)
  n = 4
  ref = H_element
FEATURE [App::DocumentObjectGroupPython] O_element082  label="O_element : 043"  # scripted group (container) (typed FeaturePython)
  n = 1
  ref = O_element
FEATURE [App::DocumentObjectGroupPython] G4_POLYVINYL_ALCOHOL  # scripted group (container) (typed FeaturePython)
  Dunit = g/cm3
  Dvalue = 1.3
  Group = -> [C_element090,H_element082,O_element082]
  conduct = 2
  density = 1
  expand = 3
  formula = G4_POLYVINYL_ALCOHOL
  name = G4_POLYVINYL_ALCOHOL
  specific = 4
FEATURE [App::DocumentObjectGroupPython] C_element091  label="C_element : 049"  # scripted group (container) (typed FeaturePython)
  n = 8
  ref = C_element
FEATURE [App::DocumentObjectGroupPython] H_element083  label="H_element : 045"  # scripted group (container) (typed FeaturePython)
  n = 14
  ref = H_element
FEATURE [App::DocumentObjectGroupPython] O_element083  label="O_element : 044"  # scripted group (container) (typed FeaturePython)
  n = 2
  ref = O_element
FEATURE [App::DocumentObjectGroupPython] G4_POLYVINYL_BUTYRAL  # scripted group (container) (typed FeaturePython)
  Dunit = g/cm3
  Dvalue = 1.12
  Group = -> [C_element091,H_element083,O_element083]
  conduct = 2
  density = 1
  expand = 3
  formula = G4_POLYVINYL_BUTYRAL
  name = G4_POLYVINYL_BUTYRAL
  specific = 4
FEATURE [App::DocumentObjectGroupPython] C_element092  label="C_element : 050"  # scripted group (container) (typed FeaturePython)
  n = 2
  ref = C_element
FEATURE [App::DocumentObjectGroupPython] H_element084  label="H_element : 046"  # scripted group (container) (typed FeaturePython)
  n = 3
  ref = H_element
FEATURE [App::DocumentObjectGroupPython] Cl_element019  label="Cl_element : 009"  # scripted group (container) (typed FeaturePython)
  n = 1
  ref = Cl_element
FEATURE [App::DocumentObjectGroupPython] G4_POLYVINYL_CHLORIDE  # scripted group (container) (typed FeaturePython)
  Dunit = g/cm3
  Dvalue = 1.3
  Group = -> [C_element092,H_element084,Cl_element019]
  conduct = 2
  density = 1
  expand = 3
  formula = G4_POLYVINYL_CHLORIDE
  name = G4_POLYVINYL_CHLORIDE
  specific = 4
FEATURE [App::DocumentObjectGroupPython] C_element093  label="C_element : 051"  # scripted group (container) (typed FeaturePython)
  n = 2
  ref = C_element
FEATURE [App::DocumentObjectGroupPython] H_element085  label="H_element : 047"  # scripted group (container) (typed FeaturePython)
  n = 2
  ref = H_element
FEATURE [App::DocumentObjectGroupPython] Cl_element020  label="Cl_element : 010"  # scripted group (container) (typed FeaturePython)
  n = 2
  ref = Cl_element
FEATURE [App::DocumentObjectGroupPython] G4_POLYVINYLIDENE_CHLORIDE  # scripted group (container) (typed FeaturePython)
  Dunit = g/cm3
  Dvalue = 1.7
  Group = -> [C_element093,H_element085,Cl_element020]
  conduct = 2
  density = 1
  expand = 3
  formula = G4_POLYVINYLIDENE_CHLORIDE
  name = G4_POLYVINYLIDENE_CHLORIDE
  specific = 4
FEATURE [App::DocumentObjectGroupPython] C_element094  label="C_element : 052"  # scripted group (container) (typed FeaturePython)
  n = 2
  ref = C_element
FEATURE [App::DocumentObjectGroupPython] H_element086  label="H_element : 048"  # scripted group (container) (typed FeaturePython)
  n = 2
  ref = H_element
FEATURE [App::DocumentObjectGroupPython] F_element016  label="F_element : 007"  # scripted group (container) (typed FeaturePython)
  n = 2
  ref = F_element
FEATURE [App::DocumentObjectGroupPython] G4_POLYVINYLIDENE_FLUORIDE  # scripted group (container) (typed FeaturePython)
  Dunit = g/cm3
  Dvalue = 1.76
  Group = -> [C_element094,H_element086,F_element016]
  conduct = 2
  density = 1
  expand = 3
  formula = G4_POLYVINYLIDENE_FLUORIDE
  name = G4_POLYVINYLIDENE_FLUORIDE
  specific = 4
FEATURE [App::DocumentObjectGroupPython] C_element095  label="C_element : 053"  # scripted group (container) (typed FeaturePython)
  n = 6
  ref = C_element
FEATURE [App::DocumentObjectGroupPython] H_element087  label="H_element : 9"  # scripted group (container) (typed FeaturePython)
  n = 9
  ref = H_element
FEATURE [App::DocumentObjectGroupPython] N_element037  label="N_element : 016"  # scripted group (container) (typed FeaturePython)
  n = 1
  ref = N_element
FEATURE [App::DocumentObjectGroupPython] O_element084  label="O_element : 045"  # scripted group (container) (typed FeaturePython)
  n = 1
  ref = O_element
FEATURE [App::DocumentObjectGroupPython] G4_POLYVINYL_PYRROLIDONE  # scripted group (container) (typed FeaturePython)
  Dunit = g/cm3
  Dvalue = 1.25
  Group = -> [C_element095,H_element087,N_element037,O_element084]
  conduct = 2
  density = 1
  expand = 3
  formula = G4_POLYVINYL_PYRROLIDONE
  name = G4_POLYVINYL_PYRROLIDONE
  specific = 4
FEATURE [App::DocumentObjectGroupPython] K_element008  label="K_element : 1"  # scripted group (container) (typed FeaturePython)
  n = 1
  ref = K_element
FEATURE [App::DocumentObjectGroupPython] I_element006  label="I_element : 003"  # scripted group (container) (typed FeaturePython)
  n = 1
  ref = I_element
FEATURE [App::DocumentObjectGroupPython] G4_POTASSIUM_IODIDE  # scripted group (container) (typed FeaturePython)
  Dunit = g/cm3
  Dvalue = 3.13
  Group = -> [K_element008,I_element006]
  conduct = 2
  density = 1
  expand = 3
  formula = G4_POTASSIUM_IODIDE
  name = G4_POTASSIUM_IODIDE
  specific = 4
FEATURE [App::DocumentObjectGroupPython] K_element009  label="K_element : 2"  # scripted group (container) (typed FeaturePython)
  n = 2
  ref = K_element
FEATURE [App::DocumentObjectGroupPython] O_element085  label="O_element : 046"  # scripted group (container) (typed FeaturePython)
  n = 1
  ref = O_element
FEATURE [App::DocumentObjectGroupPython] G4_POTASSIUM_OXIDE  # scripted group (container) (typed FeaturePython)
  Dunit = g/cm3
  Dvalue = 2.32
  Group = -> [K_element009,O_element085]
  conduct = 2
  density = 1
  expand = 3
  formula = G4_POTASSIUM_OXIDE
  name = G4_POTASSIUM_OXIDE
  specific = 4
FEATURE [App::DocumentObjectGroupPython] C_element096  label="C_element : 054"  # scripted group (container) (typed FeaturePython)
  n = 3
  ref = C_element
FEATURE [App::DocumentObjectGroupPython] H_element088  label="H_element : 049"  # scripted group (container) (typed FeaturePython)
  n = 8
  ref = H_element
FEATURE [App::DocumentObjectGroupPython] G4_PROPANE  # scripted group (container) (typed FeaturePython)
  Dunit = g/cm3
  Dvalue = 0.00187939
  Group = -> [C_element096,H_element088]
  conduct = 2
  density = 1
  expand = 3
  formula = G4_PROPANE
  name = G4_PROPANE
  specific = 4
FEATURE [App::DocumentObjectGroupPython] C_element097  label="C_element : 055"  # scripted group (container) (typed FeaturePython)
  n = 3
  ref = C_element
FEATURE [App::DocumentObjectGroupPython] H_element089  label="H_element : 050"  # scripted group (container) (typed FeaturePython)
  n = 8
  ref = H_element
FEATURE [App::DocumentObjectGroupPython] G4_lPROPANE  # scripted group (container) (typed FeaturePython)
  Dunit = g/cm3
  Dvalue = 0.43
  Group = -> [C_element097,H_element089]
  conduct = 2
  density = 1
  expand = 3
  formula = G4_lPROPANE
  name = G4_lPROPANE
  specific = 4
FEATURE [App::DocumentObjectGroupPython] C_element098  label="C_element : 056"  # scripted group (container) (typed FeaturePython)
  n = 3
  ref = C_element
FEATURE [App::DocumentObjectGroupPython] H_element090  label="H_element : 051"  # scripted group (container) (typed FeaturePython)
  n = 8
  ref = H_element
FEATURE [App::DocumentObjectGroupPython] O_element086  label="O_element : 047"  # scripted group (container) (typed FeaturePython)
  n = 1
  ref = O_element
FEATURE [App::DocumentObjectGroupPython] G4_N_PROPYL_ALCOHOL  label="G4_N-PROPYL_ALCOHOL"  # scripted group (container) (typed FeaturePython)
  Dunit = g/cm3
  Dvalue = 0.8035
  Group = -> [C_element098,H_element090,O_element086]
  conduct = 2
  density = 1
  expand = 3
  formula = G4_N-PROPYL_ALCOHOL
  name = G4_N-PROPYL_ALCOHOL
  specific = 4
FEATURE [App::DocumentObjectGroupPython] C_element099  label="C_element : 057"  # scripted group (container) (typed FeaturePython)
  n = 5
  ref = C_element
FEATURE [App::DocumentObjectGroupPython] H_element091  label="H_element : 052"  # scripted group (container) (typed FeaturePython)
  n = 5
  ref = H_element
FEATURE [App::DocumentObjectGroupPython] N_element038  label="N_element : 017"  # scripted group (container) (typed FeaturePython)
  n = 1
  ref = N_element
FEATURE [App::DocumentObjectGroupPython] G4_PYRIDINE  # scripted group (container) (typed FeaturePython)
  Dunit = g/cm3
  Dvalue = 0.9819
  Group = -> [C_element099,H_element091,N_element038]
  conduct = 2
  density = 1
  expand = 3
  formula = G4_PYRIDINE
  name = G4_PYRIDINE
  specific = 4
FEATURE [App::DocumentObjectGroupPython] H_element092  label="H_element : 0.144"  # scripted group (container) (typed FeaturePython)
  n = 0.143711
FEATURE [App::DocumentObjectGroupPython] C_element100  label="C_element : 0.856"  # scripted group (container) (typed FeaturePython)
  n = 0.856289
FEATURE [App::DocumentObjectGroupPython] G4_RUBBER_BUTYL  # scripted group (container) (typed FeaturePython)
  Dunit = g/cm3
  Dvalue = 0.92
  Group = -> [H_element092,C_element100]
  conduct = 2
  density = 1
  expand = 3
  formula = G4_RUBBER_BUTYL
  name = G4_RUBBER_BUTYL
  specific = 4
FEATURE [App::DocumentObjectGroupPython] H_element093  label="H_element : 0.118"  # scripted group (container) (typed FeaturePython)
  n = 0.118371
FEATURE [App::DocumentObjectGroupPython] C_element101  label="C_element : 0.882"  # scripted group (container) (typed FeaturePython)
  n = 0.881629
FEATURE [App::DocumentObjectGroupPython] G4_RUBBER_NATURAL  # scripted group (container) (typed FeaturePython)
  Dunit = g/cm3
  Dvalue = 0.92
  Group = -> [H_element093,C_element101]
  conduct = 2
  density = 1
  expand = 3
  formula = G4_RUBBER_NATURAL
  name = G4_RUBBER_NATURAL
  specific = 4
FEATURE [App::DocumentObjectGroupPython] H_element094  label="H_element : 0.145"  # scripted group (container) (typed FeaturePython)
  n = 0.05692
FEATURE [App::DocumentObjectGroupPython] C_element102  label="C_element : 0.543"  # scripted group (container) (typed FeaturePython)
  n = 0.542646
FEATURE [App::DocumentObjectGroupPython] Cl_element021  label="Cl_element : 0.400"  # scripted group (container) (typed FeaturePython)
  n = 0.400434
FEATURE [App::DocumentObjectGroupPython] G4_RUBBER_NEOPRENE  # scripted group (container) (typed FeaturePython)
  Dunit = g/cm3
  Dvalue = 1.23
  Group = -> [H_element094,C_element102,Cl_element021]
  conduct = 2
  density = 1
  expand = 3
  formula = G4_RUBBER_NEOPRENE
  name = G4_RUBBER_NEOPRENE
  specific = 4
FEATURE [App::DocumentObjectGroupPython] Si_element006  label="Si_element : 1"  # scripted group (container) (typed FeaturePython)
  n = 1
  ref = Si_element
FEATURE [App::DocumentObjectGroupPython] O_element087  label="O_element : 048"  # scripted group (container) (typed FeaturePython)
  n = 2
  ref = O_element
FEATURE [App::DocumentObjectGroupPython] G4_SILICON_DIOXIDE  # scripted group (container) (typed FeaturePython)
  Dunit = g/cm3
  Dvalue = 2.32
  Group = -> [Si_element006,O_element087]
  conduct = 2
  density = 1
  expand = 3
  formula = G4_SILICON_DIOXIDE
  name = G4_SILICON_DIOXIDE
  specific = 4
FEATURE [App::DocumentObjectGroupPython] Ag_element002  label="Ag_element : 1"  # scripted group (container) (typed FeaturePython)
  n = 1
  ref = Ag_element
FEATURE [App::DocumentObjectGroupPython] Br_element005  label="Br_element : 003"  # scripted group (container) (typed FeaturePython)
  n = 1
  ref = Br_element
FEATURE [App::DocumentObjectGroupPython] G4_SILVER_BROMIDE  # scripted group (container) (typed FeaturePython)
  Dunit = g/cm3
  Dvalue = 6.473
  Group = -> [Ag_element002,Br_element005]
  conduct = 2
  density = 1
  expand = 3
  formula = G4_SILVER_BROMIDE
  name = G4_SILVER_BROMIDE
  specific = 4
FEATURE [App::DocumentObjectGroupPython] Ag_element003  label="Ag_element : 002"  # scripted group (container) (typed FeaturePython)
  n = 1
  ref = Ag_element
FEATURE [App::DocumentObjectGroupPython] Cl_element022  label="Cl_element : 011"  # scripted group (container) (typed FeaturePython)
  n = 1
  ref = Cl_element
FEATURE [App::DocumentObjectGroupPython] G4_SILVER_CHLORIDE  # scripted group (container) (typed FeaturePython)
  Dunit = g/cm3
  Dvalue = 5.56
  Group = -> [Ag_element003,Cl_element022]
  conduct = 2
  density = 1
  expand = 3
  formula = G4_SILVER_CHLORIDE
  name = G4_SILVER_CHLORIDE
  specific = 4
FEATURE [App::DocumentObjectGroupPython] Br_element006  label="Br_element : 0.423"  # scripted group (container) (typed FeaturePython)
  n = 0.422895
FEATURE [App::DocumentObjectGroupPython] Ag_element004  label="Ag_element : 0.574"  # scripted group (container) (typed FeaturePython)
  n = 0.573748
FEATURE [App::DocumentObjectGroupPython] I_element007  label="I_element : 0.649"  # scripted group (container) (typed FeaturePython)
  n = 0.003357
FEATURE [App::DocumentObjectGroupPython] G4_SILVER_HALIDES  # scripted group (container) (typed FeaturePython)
  Dunit = g/cm3
  Dvalue = 6.47
  Group = -> [Br_element006,Ag_element004,I_element007]
  conduct = 2
  density = 1
  expand = 3
  formula = G4_SILVER_HALIDES
  name = G4_SILVER_HALIDES
  specific = 4
FEATURE [App::DocumentObjectGroupPython] Ag_element005  label="Ag_element : 003"  # scripted group (container) (typed FeaturePython)
  n = 1
  ref = Ag_element
FEATURE [App::DocumentObjectGroupPython] I_element008  label="I_element : 004"  # scripted group (container) (typed FeaturePython)
  n = 1
  ref = I_element
FEATURE [App::DocumentObjectGroupPython] G4_SILVER_IODIDE  # scripted group (container) (typed FeaturePython)
  Dunit = g/cm3
  Dvalue = 6.01
  Group = -> [Ag_element005,I_element008]
  conduct = 2
  density = 1
  expand = 3
  formula = G4_SILVER_IODIDE
  name = G4_SILVER_IODIDE
  specific = 4
FEATURE [App::DocumentObjectGroupPython] H_element095  label="H_element : 0.100"  # scripted group (container) (typed FeaturePython)
  n = 0.1
FEATURE [App::DocumentObjectGroupPython] C_element103  label="C_element : 0.204"  # scripted group (container) (typed FeaturePython)
  n = 0.204
FEATURE [App::DocumentObjectGroupPython] N_element039  label="N_element : 0.759"  # scripted group (container) (typed FeaturePython)
  n = 0.042
FEATURE [App::DocumentObjectGroupPython] O_element088  label="O_element : 0.645"  # scripted group (container) (typed FeaturePython)
  n = 0.645
FEATURE [App::DocumentObjectGroupPython] Na_element013  label="Na_element : 0.100"  # scripted group (container) (typed FeaturePython)
  n = 0.002
FEATURE [App::DocumentObjectGroupPython] P_element009  label="P_element : 0.107"  # scripted group (container) (typed FeaturePython)
  n = 0.001
FEATURE [App::DocumentObjectGroupPython] S_element020  label="S_element : 0.021"  # scripted group (container) (typed FeaturePython)
  n = 0.002
FEATURE [App::DocumentObjectGroupPython] Cl_element023  label="Cl_element : 0.590"  # scripted group (container) (typed FeaturePython)
  n = 0.003
FEATURE [App::DocumentObjectGroupPython] K_element010  label="K_element : 0.001"  # scripted group (container) (typed FeaturePython)
  n = 0.001
FEATURE [App::DocumentObjectGroupPython] G4_SKIN_ICRP  # scripted group (container) (typed FeaturePython)
  Dunit = g/cm3
  Dvalue = 1.09
  Group = -> [H_element095,C_element103,N_element039,O_element088,Na_element013,P_element009,S_element020,Cl_element023,K_element010]
  conduct = 2
  density = 1
  expand = 3
  formula = G4_SKIN_ICRP
  name = G4_SKIN_ICRP
  specific = 4
FEATURE [App::DocumentObjectGroupPython] Na_element014  label="Na_element : 2"  # scripted group (container) (typed FeaturePython)
  n = 2
  ref = Na_element
FEATURE [App::DocumentObjectGroupPython] C_element104  label="C_element : 058"  # scripted group (container) (typed FeaturePython)
  n = 1
  ref = C_element
FEATURE [App::DocumentObjectGroupPython] O_element089  label="O_element : 049"  # scripted group (container) (typed FeaturePython)
  n = 3
  ref = O_element
FEATURE [App::DocumentObjectGroupPython] G4_SODIUM_CARBONATE  # scripted group (container) (typed FeaturePython)
  Dunit = g/cm3
  Dvalue = 2.532
  Group = -> [Na_element014,C_element104,O_element089]
  conduct = 2
  density = 1
  expand = 3
  formula = G4_SODIUM_CARBONATE
  name = G4_SODIUM_CARBONATE
  specific = 4
FEATURE [App::DocumentObjectGroupPython] Na_element015  label="Na_element : 1"  # scripted group (container) (typed FeaturePython)
  n = 1
  ref = Na_element
FEATURE [App::DocumentObjectGroupPython] I_element009  label="I_element : 005"  # scripted group (container) (typed FeaturePython)
  n = 1
  ref = I_element
FEATURE [App::DocumentObjectGroupPython] G4_SODIUM_IODIDE  # scripted group (container) (typed FeaturePython)
  Dunit = g/cm3
  Dvalue = 3.667
  Group = -> [Na_element015,I_element009]
  conduct = 2
  density = 1
  expand = 3
  formula = G4_SODIUM_IODIDE
  name = G4_SODIUM_IODIDE
  specific = 4
FEATURE [App::DocumentObjectGroupPython] Na_element016  label="Na_element : 003"  # scripted group (container) (typed FeaturePython)
  n = 2
  ref = Na_element
FEATURE [App::DocumentObjectGroupPython] O_element090  label="O_element : 050"  # scripted group (container) (typed FeaturePython)
  n = 1
  ref = O_element
FEATURE [App::DocumentObjectGroupPython] G4_SODIUM_MONOXIDE  # scripted group (container) (typed FeaturePython)
  Dunit = g/cm3
  Dvalue = 2.27
  Group = -> [Na_element016,O_element090]
  conduct = 2
  density = 1
  expand = 3
  formula = G4_SODIUM_MONOXIDE
  name = G4_SODIUM_MONOXIDE
  specific = 4
FEATURE [App::DocumentObjectGroupPython] Na_element017  label="Na_element : 004"  # scripted group (container) (typed FeaturePython)
  n = 1
  ref = Na_element
FEATURE [App::DocumentObjectGroupPython] N_element040  label="N_element : 018"  # scripted group (container) (typed FeaturePython)
  n = 1
  ref = N_element
FEATURE [App::DocumentObjectGroupPython] O_element091  label="O_element : 051"  # scripted group (container) (typed FeaturePython)
  n = 3
  ref = O_element
FEATURE [App::DocumentObjectGroupPython] G4_SODIUM_NITRATE  # scripted group (container) (typed FeaturePython)
  Dunit = g/cm3
  Dvalue = 2.261
  Group = -> [Na_element017,N_element040,O_element091]
  conduct = 2
  density = 1
  expand = 3
  formula = G4_SODIUM_NITRATE
  name = G4_SODIUM_NITRATE
  specific = 4
FEATURE [App::DocumentObjectGroupPython] C_element105  label="C_element : 059"  # scripted group (container) (typed FeaturePython)
  n = 14
  ref = C_element
FEATURE [App::DocumentObjectGroupPython] H_element096  label="H_element : 053"  # scripted group (container) (typed FeaturePython)
  n = 12
  ref = H_element
FEATURE [App::DocumentObjectGroupPython] G4_STILBENE  # scripted group (container) (typed FeaturePython)
  Dunit = g/cm3
  Dvalue = 0.9707
  Group = -> [C_element105,H_element096]
  conduct = 2
  density = 1
  expand = 3
  formula = G4_STILBENE
  name = G4_STILBENE
  specific = 4
FEATURE [App::DocumentObjectGroupPython] C_element106  label="C_element : 12"  # scripted group (container) (typed FeaturePython)
  n = 12
  ref = C_element
FEATURE [App::DocumentObjectGroupPython] H_element097  label="H_element : 22"  # scripted group (container) (typed FeaturePython)
  n = 22
  ref = H_element
FEATURE [App::DocumentObjectGroupPython] O_element092  label="O_element : 11"  # scripted group (container) (typed FeaturePython)
  n = 11
  ref = O_element
FEATURE [App::DocumentObjectGroupPython] G4_SUCROSE  # scripted group (container) (typed FeaturePython)
  Dunit = g/cm3
  Dvalue = 1.5805
  Group = -> [C_element106,H_element097,O_element092]
  conduct = 2
  density = 1
  expand = 3
  formula = G4_SUCROSE
  name = G4_SUCROSE
  specific = 4
FEATURE [App::DocumentObjectGroupPython] C_element107  label="C_element : 18"  # scripted group (container) (typed FeaturePython)
  n = 18
  ref = C_element
FEATURE [App::DocumentObjectGroupPython] H_element098  label="H_element : 054"  # scripted group (container) (typed FeaturePython)
  n = 14
  ref = H_element
FEATURE [App::DocumentObjectGroupPython] G4_TERPHENYL  # scripted group (container) (typed FeaturePython)
  Dunit = g/cm3
  Dvalue = 1.24
  Group = -> [C_element107,H_element098]
  conduct = 2
  density = 1
  expand = 3
  formula = G4_TERPHENYL
  name = G4_TERPHENYL
  specific = 4
FEATURE [App::DocumentObjectGroupPython] H_element099  label="H_element : 0.146"  # scripted group (container) (typed FeaturePython)
  n = 0.106
FEATURE [App::DocumentObjectGroupPython] C_element108  label="C_element : 0.883"  # scripted group (container) (typed FeaturePython)
  n = 0.099
FEATURE [App::DocumentObjectGroupPython] N_element041  label="N_element : 0.020"  # scripted group (container) (typed FeaturePython)
  n = 0.02
FEATURE [App::DocumentObjectGroupPython] O_element093  label="O_element : 0.766"  # scripted group (container) (typed FeaturePython)
  n = 0.766
FEATURE [App::DocumentObjectGroupPython] Na_element018  label="Na_element : 0.101"  # scripted group (container) (typed FeaturePython)
  n = 0.002
FEATURE [App::DocumentObjectGroupPython] P_element010  label="P_element : 0.108"  # scripted group (container) (typed FeaturePython)
  n = 0.001
FEATURE [App::DocumentObjectGroupPython] S_element021  label="S_element : 0.022"  # scripted group (container) (typed FeaturePython)
  n = 0.002
FEATURE [App::DocumentObjectGroupPython] Cl_element024  label="Cl_element : 0.002"  # scripted group (container) (typed FeaturePython)
  n = 0.002
FEATURE [App::DocumentObjectGroupPython] K_element011  label="K_element : 0.017"  # scripted group (container) (typed FeaturePython)
  n = 0.002
FEATURE [App::DocumentObjectGroupPython] G4_TESTIS_ICRP  # scripted group (container) (typed FeaturePython)
  Dunit = g/cm3
  Dvalue = 1.04
  Group = -> [H_element099,C_element108,N_element041,O_element093,Na_element018,P_element010,S_element021,Cl_element024,K_element011]
  conduct = 2
  density = 1
  expand = 3
  formula = G4_TESTIS_ICRP
  name = G4_TESTIS_ICRP
  specific = 4
FEATURE [App::DocumentObjectGroupPython] C_element109  label="C_element : 060"  # scripted group (container) (typed FeaturePython)
  n = 2
  ref = C_element
FEATURE [App::DocumentObjectGroupPython] Cl_element025  label="Cl_element : 012"  # scripted group (container) (typed FeaturePython)
  n = 4
  ref = Cl_element
FEATURE [App::DocumentObjectGroupPython] G4_TETRACHLOROETHYLENE  # scripted group (container) (typed FeaturePython)
  Dunit = g/cm3
  Dvalue = 1.625
  Group = -> [C_element109,Cl_element025]
  conduct = 2
  density = 1
  expand = 3
  formula = G4_TETRACHLOROETHYLENE
  name = G4_TETRACHLOROETHYLENE
  specific = 4
FEATURE [App::DocumentObjectGroupPython] Tl_element001  label="Tl_element : 1"  # scripted group (container) (typed FeaturePython)
  n = 1
  ref = Tl_element
FEATURE [App::DocumentObjectGroupPython] Cl_element026  label="Cl_element : 013"  # scripted group (container) (typed FeaturePython)
  n = 1
  ref = Cl_element
FEATURE [App::DocumentObjectGroupPython] G4_THALLIUM_CHLORIDE  # scripted group (container) (typed FeaturePython)
  Dunit = g/cm3
  Dvalue = 7.004
  Group = -> [Tl_element001,Cl_element026]
  conduct = 2
  density = 1
  expand = 3
  formula = G4_THALLIUM_CHLORIDE
  name = G4_THALLIUM_CHLORIDE
  specific = 4
FEATURE [App::DocumentObjectGroupPython] H_element100  label="H_element : 0.147"  # scripted group (container) (typed FeaturePython)
  n = 0.105
FEATURE [App::DocumentObjectGroupPython] C_element110  label="C_element : 0.256"  # scripted group (container) (typed FeaturePython)
  n = 0.256
FEATURE [App::DocumentObjectGroupPython] N_element042  label="N_element : 0.760"  # scripted group (container) (typed FeaturePython)
  n = 0.027
FEATURE [App::DocumentObjectGroupPython] O_element094  label="O_element : 0.602"  # scripted group (container) (typed FeaturePython)
  n = 0.602
FEATURE [App::DocumentObjectGroupPython] Na_element019  label="Na_element : 0.102"  # scripted group (container) (typed FeaturePython)
  n = 0.001
FEATURE [App::DocumentObjectGroupPython] P_element011  label="P_element : 0.109"  # scripted group (container) (typed FeaturePython)
  n = 0.002
FEATURE [App::DocumentObjectGroupPython] S_element022  label="S_element : 0.023"  # scripted group (container) (typed FeaturePython)
  n = 0.003
FEATURE [App::DocumentObjectGroupPython] Cl_element027  label="Cl_element : 0.591"  # scripted group (container) (typed FeaturePython)
  n = 0.002
FEATURE [App::DocumentObjectGroupPython] K_element012  label="K_element : 0.018"  # scripted group (container) (typed FeaturePython)
  n = 0.002
FEATURE [App::DocumentObjectGroupPython] G4_TISSUE_SOFT_ICRP  # scripted group (container) (typed FeaturePython)
  Dunit = g/cm3
  Dvalue = 1.03
  Group = -> [H_element100,C_element110,N_element042,O_element094,Na_element019,P_element011,S_element022,Cl_element027,K_element012]
  conduct = 2
  density = 1
  expand = 3
  formula = G4_TISSUE_SOFT_ICRP
  name = G4_TISSUE_SOFT_ICRP
  specific = 4
FEATURE [App::DocumentObjectGroupPython] H_element101  label="H_element : 0.148"  # scripted group (container) (typed FeaturePython)
  n = 0.101
FEATURE [App::DocumentObjectGroupPython] C_element111  label="C_element : 0.111"  # scripted group (container) (typed FeaturePython)
  n = 0.111
FEATURE [App::DocumentObjectGroupPython] N_element043  label="N_element : 0.026"  # scripted group (container) (typed FeaturePython)
  n = 0.026
FEATURE [App::DocumentObjectGroupPython] O_element095  label="O_element : 0.762"  # scripted group (container) (typed FeaturePython)
  n = 0.762
FEATURE [App::DocumentObjectGroupPython] G4_TISSUE_SOFT_ICRU_4  label="G4_TISSUE_SOFT_ICRU-4"  # scripted group (container) (typed FeaturePython)
  Dunit = g/cm3
  Dvalue = 1
  Group = -> [H_element101,C_element111,N_element043,O_element095]
  conduct = 2
  density = 1
  expand = 3
  formula = G4_TISSUE_SOFT_ICRU-4
  name = G4_TISSUE_SOFT_ICRU-4
  specific = 4
FEATURE [App::DocumentObjectGroupPython] H_element102  label="H_element : 0.149"  # scripted group (container) (typed FeaturePython)
  n = 0.101869
FEATURE [App::DocumentObjectGroupPython] C_element112  label="C_element : 0.456"  # scripted group (container) (typed FeaturePython)
  n = 0.456179
FEATURE [App::DocumentObjectGroupPython] N_element044  label="N_element : 0.761"  # scripted group (container) (typed FeaturePython)
  n = 0.035172
FEATURE [App::DocumentObjectGroupPython] O_element096  label="O_element : 0.407"  # scripted group (container) (typed FeaturePython)
  n = 0.40678
FEATURE [App::DocumentObjectGroupPython] G4_TISSUE_METHANE  label="G4_TISSUE-METHANE"  # scripted group (container) (typed FeaturePython)
  Dunit = g/cm3
  Dvalue = 0.00106409
  Group = -> [H_element102,C_element112,N_element044,O_element096]
  conduct = 2
  density = 1
  expand = 3
  formula = G4_TISSUE-METHANE
  name = G4_TISSUE-METHANE
  specific = 4
FEATURE [App::DocumentObjectGroupPython] H_element103  label="H_element : 0.103"  # scripted group (container) (typed FeaturePython)
  n = 0.102672
FEATURE [App::DocumentObjectGroupPython] C_element113  label="C_element : 0.569"  # scripted group (container) (typed FeaturePython)
  n = 0.56894
FEATURE [App::DocumentObjectGroupPython] N_element045  label="N_element : 0.762"  # scripted group (container) (typed FeaturePython)
  n = 0.035022
FEATURE [App::DocumentObjectGroupPython] O_element097  label="O_element : 0.293"  # scripted group (container) (typed FeaturePython)
  n = 0.293366
FEATURE [App::DocumentObjectGroupPython] G4_TISSUE_PROPANE  label="G4_TISSUE-PROPANE"  # scripted group (container) (typed FeaturePython)
  Dunit = g/cm3
  Dvalue = 0.00182628
  Group = -> [H_element103,C_element113,N_element045,O_element097]
  conduct = 2
  density = 1
  expand = 3
  formula = G4_TISSUE-PROPANE
  name = G4_TISSUE-PROPANE
  specific = 4
FEATURE [App::DocumentObjectGroupPython] Ti_element003  label="Ti_element : 1"  # scripted group (container) (typed FeaturePython)
  n = 1
  ref = Ti_element
FEATURE [App::DocumentObjectGroupPython] O_element098  label="O_element : 052"  # scripted group (container) (typed FeaturePython)
  n = 2
  ref = O_element
FEATURE [App::DocumentObjectGroupPython] G4_TITANIUM_DIOXIDE  # scripted group (container) (typed FeaturePython)
  Dunit = g/cm3
  Dvalue = 4.26
  Group = -> [Ti_element003,O_element098]
  conduct = 2
  density = 1
  expand = 3
  formula = G4_TITANIUM_DIOXIDE
  name = G4_TITANIUM_DIOXIDE
  specific = 4
FEATURE [App::DocumentObjectGroupPython] C_element114  label="C_element : 061"  # scripted group (container) (typed FeaturePython)
  n = 7
  ref = C_element
FEATURE [App::DocumentObjectGroupPython] H_element104  label="H_element : 055"  # scripted group (container) (typed FeaturePython)
  n = 8
  ref = H_element
FEATURE [App::DocumentObjectGroupPython] G4_TOLUENE  # scripted group (container) (typed FeaturePython)
  Dunit = g/cm3
  Dvalue = 0.8669
  Group = -> [C_element114,H_element104]
  conduct = 2
  density = 1
  expand = 3
  formula = G4_TOLUENE
  name = G4_TOLUENE
  specific = 4
FEATURE [App::DocumentObjectGroupPython] C_element115  label="C_element : 062"  # scripted group (container) (typed FeaturePython)
  n = 2
  ref = C_element
FEATURE [App::DocumentObjectGroupPython] H_element105  label="H_element : 056"  # scripted group (container) (typed FeaturePython)
  n = 1
  ref = H_element
FEATURE [App::DocumentObjectGroupPython] Cl_element028  label="Cl_element : 014"  # scripted group (container) (typed FeaturePython)
  n = 3
  ref = Cl_element
FEATURE [App::DocumentObjectGroupPython] G4_TRICHLOROETHYLENE  # scripted group (container) (typed FeaturePython)
  Dunit = g/cm3
  Dvalue = 1.46
  Group = -> [C_element115,H_element105,Cl_element028]
  conduct = 2
  density = 1
  expand = 3
  formula = G4_TRICHLOROETHYLENE
  name = G4_TRICHLOROETHYLENE
  specific = 4
FEATURE [App::DocumentObjectGroupPython] C_element116  label="C_element : 063"  # scripted group (container) (typed FeaturePython)
  n = 6
  ref = C_element
FEATURE [App::DocumentObjectGroupPython] H_element106  label="H_element : 15"  # scripted group (container) (typed FeaturePython)
  n = 15
  ref = H_element
FEATURE [App::DocumentObjectGroupPython] O_element099  label="O_element : 053"  # scripted group (container) (typed FeaturePython)
  n = 4
  ref = O_element
FEATURE [App::DocumentObjectGroupPython] P_element012  label="P_element : 1"  # scripted group (container) (typed FeaturePython)
  n = 1
  ref = P_element
FEATURE [App::DocumentObjectGroupPython] G4_TRIETHYL_PHOSPHATE  # scripted group (container) (typed FeaturePython)
  Dunit = g/cm3
  Dvalue = 1.07
  Group = -> [C_element116,H_element106,O_element099,P_element012]
  conduct = 2
  density = 1
  expand = 3
  formula = G4_TRIETHYL_PHOSPHATE
  name = G4_TRIETHYL_PHOSPHATE
  specific = 4
FEATURE [App::DocumentObjectGroupPython] W_element003  label="W_element : 003"  # scripted group (container) (typed FeaturePython)
  n = 1
  ref = W_element
FEATURE [App::DocumentObjectGroupPython] F_element017  label="F_element : 6"  # scripted group (container) (typed FeaturePython)
  n = 6
  ref = F_element
FEATURE [App::DocumentObjectGroupPython] G4_TUNGSTEN_HEXAFLUORIDE  # scripted group (container) (typed FeaturePython)
  Dunit = g/cm3
  Dvalue = 2.4
  Group = -> [W_element003,F_element017]
  conduct = 2
  density = 1
  expand = 3
  formula = G4_TUNGSTEN_HEXAFLUORIDE
  name = G4_TUNGSTEN_HEXAFLUORIDE
  specific = 4
FEATURE [App::DocumentObjectGroupPython] U_element001  label="U_element : 1"  # scripted group (container) (typed FeaturePython)
  n = 1
  ref = U_element
FEATURE [App::DocumentObjectGroupPython] C_element117  label="C_element : 064"  # scripted group (container) (typed FeaturePython)
  n = 2
  ref = C_element
FEATURE [App::DocumentObjectGroupPython] G4_URANIUM_DICARBIDE  # scripted group (container) (typed FeaturePython)
  Dunit = g/cm3
  Dvalue = 11.28
  Group = -> [U_element001,C_element117]
  conduct = 2
  density = 1
  expand = 3
  formula = G4_URANIUM_DICARBIDE
  name = G4_URANIUM_DICARBIDE
  specific = 4
FEATURE [App::DocumentObjectGroupPython] U_element002  label="U_element : 002"  # scripted group (container) (typed FeaturePython)
  n = 1
  ref = U_element
FEATURE [App::DocumentObjectGroupPython] C_element118  label="C_element : 065"  # scripted group (container) (typed FeaturePython)
  n = 1
  ref = C_element
FEATURE [App::DocumentObjectGroupPython] G4_URANIUM_MONOCARBIDE  # scripted group (container) (typed FeaturePython)
  Dunit = g/cm3
  Dvalue = 13.63
  Group = -> [U_element002,C_element118]
  conduct = 2
  density = 1
  expand = 3
  formula = G4_URANIUM_MONOCARBIDE
  name = G4_URANIUM_MONOCARBIDE
  specific = 4
FEATURE [App::DocumentObjectGroupPython] U_element003  label="U_element : 003"  # scripted group (container) (typed FeaturePython)
  n = 1
  ref = U_element
FEATURE [App::DocumentObjectGroupPython] O_element100  label="O_element : 054"  # scripted group (container) (typed FeaturePython)
  n = 2
  ref = O_element
FEATURE [App::DocumentObjectGroupPython] G4_URANIUM_OXIDE  # scripted group (container) (typed FeaturePython)
  Dunit = g/cm3
  Dvalue = 10.96
  Group = -> [U_element003,O_element100]
  conduct = 2
  density = 1
  expand = 3
  formula = G4_URANIUM_OXIDE
  name = G4_URANIUM_OXIDE
  specific = 4
FEATURE [App::DocumentObjectGroupPython] C_element119  label="C_element : 066"  # scripted group (container) (typed FeaturePython)
  n = 1
  ref = C_element
FEATURE [App::DocumentObjectGroupPython] H_element107  label="H_element : 057"  # scripted group (container) (typed FeaturePython)
  n = 4
  ref = H_element
FEATURE [App::DocumentObjectGroupPython] N_element046  label="N_element : 019"  # scripted group (container) (typed FeaturePython)
  n = 2
  ref = N_element
FEATURE [App::DocumentObjectGroupPython] O_element101  label="O_element : 055"  # scripted group (container) (typed FeaturePython)
  n = 1
  ref = O_element
FEATURE [App::DocumentObjectGroupPython] G4_UREA  # scripted group (container) (typed FeaturePython)
  Dunit = g/cm3
  Dvalue = 1.323
  Group = -> [C_element119,H_element107,N_element046,O_element101]
  conduct = 2
  density = 1
  expand = 3
  formula = G4_UREA
  name = G4_UREA
  specific = 4
FEATURE [App::DocumentObjectGroupPython] C_element120  label="C_element : 067"  # scripted group (container) (typed FeaturePython)
  n = 5
  ref = C_element
FEATURE [App::DocumentObjectGroupPython] H_element108  label="H_element : 058"  # scripted group (container) (typed FeaturePython)
  n = 11
  ref = H_element
FEATURE [App::DocumentObjectGroupPython] N_element047  label="N_element : 020"  # scripted group (container) (typed FeaturePython)
  n = 1
  ref = N_element
FEATURE [App::DocumentObjectGroupPython] O_element102  label="O_element : 056"  # scripted group (container) (typed FeaturePython)
  n = 2
  ref = O_element
FEATURE [App::DocumentObjectGroupPython] G4_VALINE  # scripted group (container) (typed FeaturePython)
  Dunit = g/cm3
  Dvalue = 1.23
  Group = -> [C_element120,H_element108,N_element047,O_element102]
  conduct = 2
  density = 1
  expand = 3
  formula = G4_VALINE
  name = G4_VALINE
  specific = 4
FEATURE [App::DocumentObjectGroupPython] H_element109  label="H_element : 0.009"  # scripted group (container) (typed FeaturePython)
  n = 0.009417
FEATURE [App::DocumentObjectGroupPython] C_element121  label="C_element : 0.281"  # scripted group (container) (typed FeaturePython)
  n = 0.280555
FEATURE [App::DocumentObjectGroupPython] F_element018  label="F_element : 0.710"  # scripted group (container) (typed FeaturePython)
  n = 0.710028
FEATURE [App::DocumentObjectGroupPython] G4_VITON  # scripted group (container) (typed FeaturePython)
  Dunit = g/cm3
  Dvalue = 1.8
  Group = -> [H_element109,C_element121,F_element018]
  conduct = 2
  density = 1
  expand = 3
  formula = G4_VITON
  name = G4_VITON
  specific = 4
FEATURE [App::DocumentObjectGroupPython] H_element110  label="H_element : 059"  # scripted group (container) (typed FeaturePython)
  n = 2
  ref = H_element
FEATURE [App::DocumentObjectGroupPython] O_element103  label="O_element : 057"  # scripted group (container) (typed FeaturePython)
  n = 1
  ref = O_element
FEATURE [App::DocumentObjectGroupPython] G4_WATER  # scripted group (container) (typed FeaturePython)
  Dunit = g/cm3
  Dvalue = 1
  Group = -> [H_element110,O_element103]
  conduct = 2
  density = 1
  expand = 3
  formula = G4_WATER
  name = G4_WATER
  specific = 4
FEATURE [App::DocumentObjectGroupPython] H_element111  label="H_element : 060"  # scripted group (container) (typed FeaturePython)
  n = 2
  ref = H_element
FEATURE [App::DocumentObjectGroupPython] O_element104  label="O_element : 058"  # scripted group (container) (typed FeaturePython)
  n = 1
  ref = O_element
FEATURE [App::DocumentObjectGroupPython] G4_WATER_VAPOR  # scripted group (container) (typed FeaturePython)
  Dunit = g/cm3
  Dvalue = 0.000756182
  Group = -> [H_element111,O_element104]
  conduct = 2
  density = 1
  expand = 3
  formula = G4_WATER_VAPOR
  name = G4_WATER_VAPOR
  specific = 4
FEATURE [App::DocumentObjectGroupPython] C_element122  label="C_element : 068"  # scripted group (container) (typed FeaturePython)
  n = 8
  ref = C_element
FEATURE [App::DocumentObjectGroupPython] H_element112  label="H_element : 061"  # scripted group (container) (typed FeaturePython)
  n = 10
  ref = H_element
FEATURE [App::DocumentObjectGroupPython] G4_XYLENE  # scripted group (container) (typed FeaturePython)
  Dunit = g/cm3
  Dvalue = 0.87
  Group = -> [C_element122,H_element112]
  conduct = 2
  density = 1
  expand = 3
  formula = G4_XYLENE
  name = G4_XYLENE
  specific = 4
FEATURE [App::DocumentObjectGroupPython] C_element123  label="C_element : 069"  # scripted group (container) (typed FeaturePython)
  n = 1
  ref = C_element
FEATURE [App::DocumentObjectGroupPython] G4_GRAPHITE  # scripted group (container) (typed FeaturePython)
  Dunit = g/cm3
  Dvalue = 2.21
  Group = -> [C_element123]
  conduct = 2
  density = 1
  expand = 3
  formula = G4_GRAPHITE
  name = G4_GRAPHITE
  specific = 4
FEATURE [App::DocumentObjectGroupPython] NIST  # scripted group (container) (typed FeaturePython)
  Group = -> [G4_A_150_TISSUE,G4_ACETONE,G4_ACETYLENE,G4_ADENINE,G4_ADIPOSE_TISSUE_ICRP,G4_AIR,G4_ALANINE,G4_ALUMINUM_OXIDE,G4_AMBER,G4_AMMONIA,G4_ANILINE,G4_ANTHRACENE,G4_B_100_BONE,G4_BAKELITE,G4_BARIUM_FLUORIDE,G4_BARIUM_SULFATE,G4_BENZENE,G4_BERYLLIUM_OXIDE,G4_BGO,G4_BLOOD_ICRP,G4_BONE_COMPACT_ICRU,G4_BONE_CORTICAL_ICRP,G4_BORON_CARBIDE,G4_BORON_OXIDE,G4_BRAIN_ICRP,G4_BUTANE,G4_N_BUTYL_ALCOHOL,G4_C_552,+152 more]
FEATURE [App::DocumentObjectGroupPython] H_element113  label="H_element : 062"  # scripted group (container) (typed FeaturePython)
  n = 1
  ref = H_element
FEATURE [App::DocumentObjectGroupPython] G4_H  # scripted group (container) (typed FeaturePython)
  Dunit = g/cm3
  Dvalue = 8.3748e-05
  Group = -> [H_element113]
  conduct = 2
  density = 1
  expand = 3
  formula = H
  name = G4_H
  specific = 4
FEATURE [App::DocumentObjectGroupPython] He_element001  label="He_element : 1"  # scripted group (container) (typed FeaturePython)
  n = 1
  ref = He_element
FEATURE [App::DocumentObjectGroupPython] G4_He  # scripted group (container) (typed FeaturePython)
  Dunit = g/cm3
  Dvalue = 0.000166322
  Group = -> [He_element001]
  conduct = 2
  density = 1
  expand = 3
  formula = He
  name = G4_He
  specific = 4
FEATURE [App::DocumentObjectGroupPython] Li_element008  label="Li_element : 008"  # scripted group (container) (typed FeaturePython)
  n = 1
  ref = Li_element
FEATURE [App::DocumentObjectGroupPython] G4_Li  # scripted group (container) (typed FeaturePython)
  Dunit = g/cm3
  Dvalue = 0.534
  Group = -> [Li_element008]
  conduct = 2
  density = 1
  expand = 3
  formula = Li
  name = G4_Li
  specific = 4
FEATURE [App::DocumentObjectGroupPython] Be_element002  label="Be_element : 002"  # scripted group (container) (typed FeaturePython)
  n = 1
  ref = Be_element
FEATURE [App::DocumentObjectGroupPython] G4_Be  # scripted group (container) (typed FeaturePython)
  Dunit = g/cm3
  Dvalue = 1.848
  Group = -> [Be_element002]
  conduct = 2
  density = 1
  expand = 3
  formula = Be
  name = G4_Be
  specific = 4
FEATURE [App::DocumentObjectGroupPython] B_element007  label="B_element : 007"  # scripted group (container) (typed FeaturePython)
  n = 1
  ref = B_element
FEATURE [App::DocumentObjectGroupPython] G4_B  # scripted group (container) (typed FeaturePython)
  Dunit = g/cm3
  Dvalue = 2.37
  Group = -> [B_element007]
  conduct = 2
  density = 1
  expand = 3
  formula = B
  name = G4_B
  specific = 4
FEATURE [App::DocumentObjectGroupPython] C_element124  label="C_element : 070"  # scripted group (container) (typed FeaturePython)
  n = 1
  ref = C_element
FEATURE [App::DocumentObjectGroupPython] G4_C  # scripted group (container) (typed FeaturePython)
  Dunit = g/cm3
  Dvalue = 2
  Group = -> [C_element124]
  conduct = 2
  density = 1
  expand = 3
  formula = C
  name = G4_C
  specific = 4
FEATURE [App::DocumentObjectGroupPython] N_element048  label="N_element : 021"  # scripted group (container) (typed FeaturePython)
  n = 1
  ref = N_element
FEATURE [App::DocumentObjectGroupPython] G4_N  # scripted group (container) (typed FeaturePython)
  Dunit = g/cm3
  Dvalue = 0.0011652
  Group = -> [N_element048]
  conduct = 2
  density = 1
  expand = 3
  formula = N
  name = G4_N
  specific = 4
FEATURE [App::DocumentObjectGroupPython] O_element105  label="O_element : 059"  # scripted group (container) (typed FeaturePython)
  n = 1
  ref = O_element
FEATURE [App::DocumentObjectGroupPython] G4_O  # scripted group (container) (typed FeaturePython)
  Dunit = g/cm3
  Dvalue = 0.00133151
  Group = -> [O_element105]
  conduct = 2
  density = 1
  expand = 3
  formula = O
  name = G4_O
  specific = 4
FEATURE [App::DocumentObjectGroupPython] F_element019  label="F_element : 008"  # scripted group (container) (typed FeaturePython)
  n = 1
  ref = F_element
FEATURE [App::DocumentObjectGroupPython] G4_F  # scripted group (container) (typed FeaturePython)
  Dunit = g/cm3
  Dvalue = 0.00158029
  Group = -> [F_element019]
  conduct = 2
  density = 1
  expand = 3
  formula = F
  name = G4_F
  specific = 4
FEATURE [App::DocumentObjectGroupPython] Ne_element001  label="Ne_element : 1"  # scripted group (container) (typed FeaturePython)
  n = 1
  ref = Ne_element
FEATURE [App::DocumentObjectGroupPython] G4_Ne  # scripted group (container) (typed FeaturePython)
  Dunit = g/cm3
  Dvalue = 0.000838505
  Group = -> [Ne_element001]
  conduct = 2
  density = 1
  expand = 3
  formula = Ne
  name = G4_Ne
  specific = 4
FEATURE [App::DocumentObjectGroupPython] Na_element020  label="Na_element : 005"  # scripted group (container) (typed FeaturePython)
  n = 1
  ref = Na_element
FEATURE [App::DocumentObjectGroupPython] G4_Na  # scripted group (container) (typed FeaturePython)
  Dunit = g/cm3
  Dvalue = 0.971
  Group = -> [Na_element020]
  conduct = 2
  density = 1
  expand = 3
  formula = Na
  name = G4_Na
  specific = 4
FEATURE [App::DocumentObjectGroupPython] Mg_element011  label="Mg_element : 005"  # scripted group (container) (typed FeaturePython)
  n = 1
  ref = Mg_element
FEATURE [App::DocumentObjectGroupPython] G4_Mg  # scripted group (container) (typed FeaturePython)
  Dunit = g/cm3
  Dvalue = 1.74
  Group = -> [Mg_element011]
  conduct = 2
  density = 1
  expand = 3
  formula = Mg
  name = G4_Mg
  specific = 4
FEATURE [App::DocumentObjectGroupPython] Al_element004  label="Al_element : 1"  # scripted group (container) (typed FeaturePython)
  n = 1
  ref = Al_element
FEATURE [App::DocumentObjectGroupPython] G4_Al  # scripted group (container) (typed FeaturePython)
  Dunit = g/cm3
  Dvalue = 2.699
  Group = -> [Al_element004]
  conduct = 2
  density = 1
  expand = 3
  formula = Al
  name = G4_Al
  specific = 4
FEATURE [App::DocumentObjectGroupPython] Si_element007  label="Si_element : 002"  # scripted group (container) (typed FeaturePython)
  n = 1
  ref = Si_element
FEATURE [App::DocumentObjectGroupPython] G4_Si  # scripted group (container) (typed FeaturePython)
  Dunit = g/cm3
  Dvalue = 2.33
  Group = -> [Si_element007]
  conduct = 2
  density = 1
  expand = 3
  formula = Si
  name = G4_Si
  specific = 4
FEATURE [App::DocumentObjectGroupPython] P_element013  label="P_element : 002"  # scripted group (container) (typed FeaturePython)
  n = 1
  ref = P_element
FEATURE [App::DocumentObjectGroupPython] G4_P  # scripted group (container) (typed FeaturePython)
  Dunit = g/cm3
  Dvalue = 2.2
  Group = -> [P_element013]
  conduct = 2
  density = 1
  expand = 3
  formula = P
  name = G4_P
  specific = 4
FEATURE [App::DocumentObjectGroupPython] S_element023  label="S_element : 007"  # scripted group (container) (typed FeaturePython)
  n = 1
  ref = S_element
FEATURE [App::DocumentObjectGroupPython] G4_S  # scripted group (container) (typed FeaturePython)
  Dunit = g/cm3
  Dvalue = 2
  Group = -> [S_element023]
  conduct = 2
  density = 1
  expand = 3
  formula = S
  name = G4_S
  specific = 4
FEATURE [App::DocumentObjectGroupPython] Cl_element029  label="Cl_element : 015"  # scripted group (container) (typed FeaturePython)
  n = 1
  ref = Cl_element
FEATURE [App::DocumentObjectGroupPython] G4_Cl  # scripted group (container) (typed FeaturePython)
  Dunit = g/cm3
  Dvalue = 0.00299473
  Group = -> [Cl_element029]
  conduct = 2
  density = 1
  expand = 3
  formula = Cl
  name = G4_Cl
  specific = 4
FEATURE [App::DocumentObjectGroupPython] Ar_element002  label="Ar_element : 1"  # scripted group (container) (typed FeaturePython)
  n = 1
  ref = Ar_element
FEATURE [App::DocumentObjectGroupPython] G4_Ar  # scripted group (container) (typed FeaturePython)
  Dunit = g/cm3
  Dvalue = 0.00166201
  Group = -> [Ar_element002]
  conduct = 2
  density = 1
  expand = 3
  formula = Ar
  name = G4_Ar
  specific = 4
FEATURE [App::DocumentObjectGroupPython] K_element013  label="K_element : 003"  # scripted group (container) (typed FeaturePython)
  n = 1
  ref = K_element
FEATURE [App::DocumentObjectGroupPython] G4_K  # scripted group (container) (typed FeaturePython)
  Dunit = g/cm3
  Dvalue = 0.862
  Group = -> [K_element013]
  conduct = 2
  density = 1
  expand = 3
  formula = K
  name = G4_K
  specific = 4
FEATURE [App::DocumentObjectGroupPython] Ca_element014  label="Ca_element : 007"  # scripted group (container) (typed FeaturePython)
  n = 1
  ref = Ca_element
FEATURE [App::DocumentObjectGroupPython] G4_Ca  # scripted group (container) (typed FeaturePython)
  Dunit = g/cm3
  Dvalue = 1.55
  Group = -> [Ca_element014]
  conduct = 2
  density = 1
  expand = 3
  formula = Ca
  name = G4_Ca
  specific = 4
FEATURE [App::DocumentObjectGroupPython] Sc_element001  label="Sc_element : 1"  # scripted group (container) (typed FeaturePython)
  n = 1
  ref = Sc_element
FEATURE [App::DocumentObjectGroupPython] G4_Sc  # scripted group (container) (typed FeaturePython)
  Dunit = g/cm3
  Dvalue = 2.989
  Group = -> [Sc_element001]
  conduct = 2
  density = 1
  expand = 3
  formula = Sc
  name = G4_Sc
  specific = 4
FEATURE [App::DocumentObjectGroupPython] Ti_element004  label="Ti_element : 002"  # scripted group (container) (typed FeaturePython)
  n = 1
  ref = Ti_element
FEATURE [App::DocumentObjectGroupPython] G4_Ti  # scripted group (container) (typed FeaturePython)
  Dunit = g/cm3
  Dvalue = 4.54
  Group = -> [Ti_element004]
  conduct = 2
  density = 1
  expand = 3
  formula = Ti
  name = G4_Ti
  specific = 4
FEATURE [App::DocumentObjectGroupPython] V_element001  label="V_element : 1"  # scripted group (container) (typed FeaturePython)
  n = 1
  ref = V_element
FEATURE [App::DocumentObjectGroupPython] G4_V  # scripted group (container) (typed FeaturePython)
  Dunit = g/cm3
  Dvalue = 6.11
  Group = -> [V_element001]
  conduct = 2
  density = 1
  expand = 3
  formula = V
  name = G4_V
  specific = 4
FEATURE [App::DocumentObjectGroupPython] Cr_element001  label="Cr_element : 1"  # scripted group (container) (typed FeaturePython)
  n = 1
  ref = Cr_element
FEATURE [App::DocumentObjectGroupPython] G4_Cr  # scripted group (container) (typed FeaturePython)
  Dunit = g/cm3
  Dvalue = 7.18
  Group = -> [Cr_element001]
  conduct = 2
  density = 1
  expand = 3
  formula = Cr
  name = G4_Cr
  specific = 4
FEATURE [App::DocumentObjectGroupPython] Mn_element001  label="Mn_element : 1"  # scripted group (container) (typed FeaturePython)
  n = 1
  ref = Mn_element
FEATURE [App::DocumentObjectGroupPython] G4_Mn  # scripted group (container) (typed FeaturePython)
  Dunit = g/cm3
  Dvalue = 7.44
  Group = -> [Mn_element001]
  conduct = 2
  density = 1
  expand = 3
  formula = Mn
  name = G4_Mn
  specific = 4
FEATURE [App::DocumentObjectGroupPython] Fe_element007  label="Fe_element : 004"  # scripted group (container) (typed FeaturePython)
  n = 1
  ref = Fe_element
FEATURE [App::DocumentObjectGroupPython] G4_Fe  # scripted group (container) (typed FeaturePython)
  Dunit = g/cm3
  Dvalue = 7.874
  Group = -> [Fe_element007]
  conduct = 2
  density = 1
  expand = 3
  formula = Fe
  name = G4_Fe
  specific = 4
FEATURE [App::DocumentObjectGroupPython] Co_element001  label="Co_element : 1"  # scripted group (container) (typed FeaturePython)
  n = 1
  ref = Co_element
FEATURE [App::DocumentObjectGroupPython] G4_Co  # scripted group (container) (typed FeaturePython)
  Dunit = g/cm3
  Dvalue = 8.9
  Group = -> [Co_element001]
  conduct = 2
  density = 1
  expand = 3
  formula = Co
  name = G4_Co
  specific = 4
FEATURE [App::DocumentObjectGroupPython] Ni_element001  label="Ni_element : 1"  # scripted group (container) (typed FeaturePython)
  n = 1
  ref = Ni_element
FEATURE [App::DocumentObjectGroupPython] G4_Ni  # scripted group (container) (typed FeaturePython)
  Dunit = g/cm3
  Dvalue = 8.902
  Group = -> [Ni_element001]
  conduct = 2
  density = 1
  expand = 3
  formula = Ni
  name = G4_Ni
  specific = 4
FEATURE [App::DocumentObjectGroupPython] Cu_element001  label="Cu_element : 1"  # scripted group (container) (typed FeaturePython)
  n = 1
  ref = Cu_element
FEATURE [App::DocumentObjectGroupPython] G4_Cu  # scripted group (container) (typed FeaturePython)
  Dunit = g/cm3
  Dvalue = 8.96
  Group = -> [Cu_element001]
  conduct = 2
  density = 1
  expand = 3
  formula = Cu
  name = G4_Cu
  specific = 4
FEATURE [App::DocumentObjectGroupPython] Zn_element001  label="Zn_element : 1"  # scripted group (container) (typed FeaturePython)
  n = 1
  ref = Zn_element
FEATURE [App::DocumentObjectGroupPython] G4_Zn  # scripted group (container) (typed FeaturePython)
  Dunit = g/cm3
  Dvalue = 7.133
  Group = -> [Zn_element001]
  conduct = 2
  density = 1
  expand = 3
  formula = Zn
  name = G4_Zn
  specific = 4
FEATURE [App::DocumentObjectGroupPython] Ga_element002  label="Ga_element : 002"  # scripted group (container) (typed FeaturePython)
  n = 1
  ref = Ga_element
FEATURE [App::DocumentObjectGroupPython] G4_Ga  # scripted group (container) (typed FeaturePython)
  Dunit = g/cm3
  Dvalue = 5.904
  Group = -> [Ga_element002]
  conduct = 2
  density = 1
  expand = 3
  formula = Ga
  name = G4_Ga
  specific = 4
FEATURE [App::DocumentObjectGroupPython] Ge_element002  label="Ge_element : 1"  # scripted group (container) (typed FeaturePython)
  n = 1
  ref = Ge_element
FEATURE [App::DocumentObjectGroupPython] G4_Ge  # scripted group (container) (typed FeaturePython)
  Dunit = g/cm3
  Dvalue = 5.323
  Group = -> [Ge_element002]
  conduct = 2
  density = 1
  expand = 3
  formula = Ge
  name = G4_Ge
  specific = 4
FEATURE [App::DocumentObjectGroupPython] As_element003  label="As_element : 002"  # scripted group (container) (typed FeaturePython)
  n = 1
  ref = As_element
FEATURE [App::DocumentObjectGroupPython] G4_As  # scripted group (container) (typed FeaturePython)
  Dunit = g/cm3
  Dvalue = 5.73
  Group = -> [As_element003]
  conduct = 2
  density = 1
  expand = 3
  formula = As
  name = G4_As
  specific = 4
FEATURE [App::DocumentObjectGroupPython] Se_element001  label="Se_element : 1"  # scripted group (container) (typed FeaturePython)
  n = 1
  ref = Se_element
FEATURE [App::DocumentObjectGroupPython] G4_Se  # scripted group (container) (typed FeaturePython)
  Dunit = g/cm3
  Dvalue = 4.5
  Group = -> [Se_element001]
  conduct = 2
  density = 1
  expand = 3
  formula = Se
  name = G4_Se
  specific = 4
FEATURE [App::DocumentObjectGroupPython] Br_element007  label="Br_element : 004"  # scripted group (container) (typed FeaturePython)
  n = 1
  ref = Br_element
FEATURE [App::DocumentObjectGroupPython] G4_Br  # scripted group (container) (typed FeaturePython)
  Dunit = g/cm3
  Dvalue = 0.0070721
  Group = -> [Br_element007]
  conduct = 2
  density = 1
  expand = 3
  formula = Br
  name = G4_Br
  specific = 4
FEATURE [App::DocumentObjectGroupPython] Kr_element001  label="Kr_element : 1"  # scripted group (container) (typed FeaturePython)
  n = 1
  ref = Kr_element
FEATURE [App::DocumentObjectGroupPython] G4_Kr  # scripted group (container) (typed FeaturePython)
  Dunit = g/cm3
  Dvalue = 0.00347832
  Group = -> [Kr_element001]
  conduct = 2
  density = 1
  expand = 3
  formula = Kr
  name = G4_Kr
  specific = 4
FEATURE [App::DocumentObjectGroupPython] Rb_element001  label="Rb_element : 1"  # scripted group (container) (typed FeaturePython)
  n = 1
  ref = Rb_element
FEATURE [App::DocumentObjectGroupPython] G4_Rb  # scripted group (container) (typed FeaturePython)
  Dunit = g/cm3
  Dvalue = 1.532
  Group = -> [Rb_element001]
  conduct = 2
  density = 1
  expand = 3
  formula = Rb
  name = G4_Rb
  specific = 4
FEATURE [App::DocumentObjectGroupPython] Sr_element001  label="Sr_element : 1"  # scripted group (container) (typed FeaturePython)
  n = 1
  ref = Sr_element
FEATURE [App::DocumentObjectGroupPython] G4_Sr  # scripted group (container) (typed FeaturePython)
  Dunit = g/cm3
  Dvalue = 2.54
  Group = -> [Sr_element001]
  conduct = 2
  density = 1
  expand = 3
  formula = Sr
  name = G4_Sr
  specific = 4
FEATURE [App::DocumentObjectGroupPython] Y_element001  label="Y_element : 1"  # scripted group (container) (typed FeaturePython)
  n = 1
  ref = Y_element
FEATURE [App::DocumentObjectGroupPython] G4_Y  # scripted group (container) (typed FeaturePython)
  Dunit = g/cm3
  Dvalue = 4.469
  Group = -> [Y_element001]
  conduct = 2
  density = 1
  expand = 3
  formula = Y
  name = G4_Y
  specific = 4
FEATURE [App::DocumentObjectGroupPython] Zr_element001  label="Zr_element : 1"  # scripted group (container) (typed FeaturePython)
  n = 1
  ref = Zr_element
FEATURE [App::DocumentObjectGroupPython] G4_Zr  # scripted group (container) (typed FeaturePython)
  Dunit = g/cm3
  Dvalue = 6.506
  Group = -> [Zr_element001]
  conduct = 2
  density = 1
  expand = 3
  formula = Zr
  name = G4_Zr
  specific = 4
FEATURE [App::DocumentObjectGroupPython] Nb_element001  label="Nb_element : 1"  # scripted group (container) (typed FeaturePython)
  n = 1
  ref = Nb_element
FEATURE [App::DocumentObjectGroupPython] G4_Nb  # scripted group (container) (typed FeaturePython)
  Dunit = g/cm3
  Dvalue = 8.57
  Group = -> [Nb_element001]
  conduct = 2
  density = 1
  expand = 3
  formula = Nb
  name = G4_Nb
  specific = 4
FEATURE [App::DocumentObjectGroupPython] Mo_element001  label="Mo_element : 1"  # scripted group (container) (typed FeaturePython)
  n = 1
  ref = Mo_element
FEATURE [App::DocumentObjectGroupPython] G4_Mo  # scripted group (container) (typed FeaturePython)
  Dunit = g/cm3
  Dvalue = 10.22
  Group = -> [Mo_element001]
  conduct = 2
  density = 1
  expand = 3
  formula = Mo
  name = G4_Mo
  specific = 4
FEATURE [App::DocumentObjectGroupPython] Tc_element001  label="Tc_element : 1"  # scripted group (container) (typed FeaturePython)
  n = 1
  ref = Tc_element
FEATURE [App::DocumentObjectGroupPython] G4_Tc  # scripted group (container) (typed FeaturePython)
  Dunit = g/cm3
  Dvalue = 11.5
  Group = -> [Tc_element001]
  conduct = 2
  density = 1
  expand = 3
  formula = Tc
  name = G4_Tc
  specific = 4
FEATURE [App::DocumentObjectGroupPython] Ru_element001  label="Ru_element : 1"  # scripted group (container) (typed FeaturePython)
  n = 1
  ref = Ru_element
FEATURE [App::DocumentObjectGroupPython] G4_Ru  # scripted group (container) (typed FeaturePython)
  Dunit = g/cm3
  Dvalue = 12.41
  Group = -> [Ru_element001]
  conduct = 2
  density = 1
  expand = 3
  formula = Ru
  name = G4_Ru
  specific = 4
FEATURE [App::DocumentObjectGroupPython] Rh_element001  label="Rh_element : 1"  # scripted group (container) (typed FeaturePython)
  n = 1
  ref = Rh_element
FEATURE [App::DocumentObjectGroupPython] G4_Rh  # scripted group (container) (typed FeaturePython)
  Dunit = g/cm3
  Dvalue = 12.41
  Group = -> [Rh_element001]
  conduct = 2
  density = 1
  expand = 3
  formula = Rh
  name = G4_Rh
  specific = 4
FEATURE [App::DocumentObjectGroupPython] Pd_element001  label="Pd_element : 1"  # scripted group (container) (typed FeaturePython)
  n = 1
  ref = Pd_element
FEATURE [App::DocumentObjectGroupPython] G4_Pd  # scripted group (container) (typed FeaturePython)
  Dunit = g/cm3
  Dvalue = 12.02
  Group = -> [Pd_element001]
  conduct = 2
  density = 1
  expand = 3
  formula = Pd
  name = G4_Pd
  specific = 4
FEATURE [App::DocumentObjectGroupPython] Ag_element006  label="Ag_element : 004"  # scripted group (container) (typed FeaturePython)
  n = 1
  ref = Ag_element
FEATURE [App::DocumentObjectGroupPython] G4_Ag  # scripted group (container) (typed FeaturePython)
  Dunit = g/cm3
  Dvalue = 10.5
  Group = -> [Ag_element006]
  conduct = 2
  density = 1
  expand = 3
  formula = Ag
  name = G4_Ag
  specific = 4
FEATURE [App::DocumentObjectGroupPython] Cd_element003  label="Cd_element : 003"  # scripted group (container) (typed FeaturePython)
  n = 1
  ref = Cd_element
FEATURE [App::DocumentObjectGroupPython] G4_Cd  # scripted group (container) (typed FeaturePython)
  Dunit = g/cm3
  Dvalue = 8.65
  Group = -> [Cd_element003]
  conduct = 2
  density = 1
  expand = 3
  formula = Cd
  name = G4_Cd
  specific = 4
FEATURE [App::DocumentObjectGroupPython] In_element001  label="In_element : 1"  # scripted group (container) (typed FeaturePython)
  n = 1
  ref = In_element
FEATURE [App::DocumentObjectGroupPython] G4_In  # scripted group (container) (typed FeaturePython)
  Dunit = g/cm3
  Dvalue = 7.31
  Group = -> [In_element001]
  conduct = 2
  density = 1
  expand = 3
  formula = In
  name = G4_In
  specific = 4
FEATURE [App::DocumentObjectGroupPython] Sn_element001  label="Sn_element : 1"  # scripted group (container) (typed FeaturePython)
  n = 1
  ref = Sn_element
FEATURE [App::DocumentObjectGroupPython] G4_Sn  # scripted group (container) (typed FeaturePython)
  Dunit = g/cm3
  Dvalue = 7.31
  Group = -> [Sn_element001]
  conduct = 2
  density = 1
  expand = 3
  formula = Sn
  name = G4_Sn
  specific = 4
FEATURE [App::DocumentObjectGroupPython] Sb_element001  label="Sb_element : 1"  # scripted group (container) (typed FeaturePython)
  n = 1
  ref = Sb_element
FEATURE [App::DocumentObjectGroupPython] G4_Sb  # scripted group (container) (typed FeaturePython)
  Dunit = g/cm3
  Dvalue = 6.691
  Group = -> [Sb_element001]
  conduct = 2
  density = 1
  expand = 3
  formula = Sb
  name = G4_Sb
  specific = 4
FEATURE [App::DocumentObjectGroupPython] Te_element002  label="Te_element : 002"  # scripted group (container) (typed FeaturePython)
  n = 1
  ref = Te_element
FEATURE [App::DocumentObjectGroupPython] G4_Te  # scripted group (container) (typed FeaturePython)
  Dunit = g/cm3
  Dvalue = 6.24
  Group = -> [Te_element002]
  conduct = 2
  density = 1
  expand = 3
  formula = Te
  name = G4_Te
  specific = 4
FEATURE [App::DocumentObjectGroupPython] I_element010  label="I_element : 006"  # scripted group (container) (typed FeaturePython)
  n = 1
  ref = I_element
FEATURE [App::DocumentObjectGroupPython] G4_I  # scripted group (container) (typed FeaturePython)
  Dunit = g/cm3
  Dvalue = 4.93
  Group = -> [I_element010]
  conduct = 2
  density = 1
  expand = 3
  formula = I
  name = G4_I
  specific = 4
FEATURE [App::DocumentObjectGroupPython] Xe_element001  label="Xe_element : 1"  # scripted group (container) (typed FeaturePython)
  n = 1
  ref = Xe_element
FEATURE [App::DocumentObjectGroupPython] G4_Xe  # scripted group (container) (typed FeaturePython)
  Dunit = g/cm3
  Dvalue = 0.00548536
  Group = -> [Xe_element001]
  conduct = 2
  density = 1
  expand = 3
  formula = Xe
  name = G4_Xe
  specific = 4
FEATURE [App::DocumentObjectGroupPython] Cs_element003  label="Cs_element : 003"  # scripted group (container) (typed FeaturePython)
  n = 1
  ref = Cs_element
FEATURE [App::DocumentObjectGroupPython] G4_Cs  # scripted group (container) (typed FeaturePython)
  Dunit = g/cm3
  Dvalue = 1.873
  Group = -> [Cs_element003]
  conduct = 2
  density = 1
  expand = 3
  formula = Cs
  name = G4_Cs
  specific = 4
FEATURE [App::DocumentObjectGroupPython] Ba_element003  label="Ba_element : 003"  # scripted group (container) (typed FeaturePython)
  n = 1
  ref = Ba_element
FEATURE [App::DocumentObjectGroupPython] G4_Ba  # scripted group (container) (typed FeaturePython)
  Dunit = g/cm3
  Dvalue = 3.5
  Group = -> [Ba_element003]
  conduct = 2
  density = 1
  expand = 3
  formula = Ba
  name = G4_Ba
  specific = 4
FEATURE [App::DocumentObjectGroupPython] La_element003  label="La_element : 003"  # scripted group (container) (typed FeaturePython)
  n = 1
  ref = La_element
FEATURE [App::DocumentObjectGroupPython] G4_La  # scripted group (container) (typed FeaturePython)
  Dunit = g/cm3
  Dvalue = 6.154
  Group = -> [La_element003]
  conduct = 2
  density = 1
  expand = 3
  formula = La
  name = G4_La
  specific = 4
FEATURE [App::DocumentObjectGroupPython] Ce_element002  label="Ce_element : 1"  # scripted group (container) (typed FeaturePython)
  n = 1
  ref = Ce_element
FEATURE [App::DocumentObjectGroupPython] G4_Ce  # scripted group (container) (typed FeaturePython)
  Dunit = g/cm3
  Dvalue = 6.657
  Group = -> [Ce_element002]
  conduct = 2
  density = 1
  expand = 3
  formula = Ce
  name = G4_Ce
  specific = 4
FEATURE [App::DocumentObjectGroupPython] Pr_element001  label="Pr_element : 1"  # scripted group (container) (typed FeaturePython)
  n = 1
  ref = Pr_element
FEATURE [App::DocumentObjectGroupPython] G4_Pr  # scripted group (container) (typed FeaturePython)
  Dunit = g/cm3
  Dvalue = 6.71
  Group = -> [Pr_element001]
  conduct = 2
  density = 1
  expand = 3
  formula = Pr
  name = G4_Pr
  specific = 4
FEATURE [App::DocumentObjectGroupPython] Nd_element001  label="Nd_element : 1"  # scripted group (container) (typed FeaturePython)
  n = 1
  ref = Nd_element
FEATURE [App::DocumentObjectGroupPython] G4_Nd  # scripted group (container) (typed FeaturePython)
  Dunit = g/cm3
  Dvalue = 6.9
  Group = -> [Nd_element001]
  conduct = 2
  density = 1
  expand = 3
  formula = Nd
  name = G4_Nd
  specific = 4
FEATURE [App::DocumentObjectGroupPython] Pm_element001  label="Pm_element : 1"  # scripted group (container) (typed FeaturePython)
  n = 1
  ref = Pm_element
FEATURE [App::DocumentObjectGroupPython] G4_Pm  # scripted group (container) (typed FeaturePython)
  Dunit = g/cm3
  Dvalue = 7.22
  Group = -> [Pm_element001]
  conduct = 2
  density = 1
  expand = 3
  formula = Pm
  name = G4_Pm
  specific = 4
FEATURE [App::DocumentObjectGroupPython] Sm_element001  label="Sm_element : 1"  # scripted group (container) (typed FeaturePython)
  n = 1
  ref = Sm_element
FEATURE [App::DocumentObjectGroupPython] G4_Sm  # scripted group (container) (typed FeaturePython)
  Dunit = g/cm3
  Dvalue = 7.46
  Group = -> [Sm_element001]
  conduct = 2
  density = 1
  expand = 3
  formula = Sm
  name = G4_Sm
  specific = 4
FEATURE [App::DocumentObjectGroupPython] Eu_element001  label="Eu_element : 1"  # scripted group (container) (typed FeaturePython)
  n = 1
  ref = Eu_element
FEATURE [App::DocumentObjectGroupPython] G4_Eu  # scripted group (container) (typed FeaturePython)
  Dunit = g/cm3
  Dvalue = 5.243
  Group = -> [Eu_element001]
  conduct = 2
  density = 1
  expand = 3
  formula = Eu
  name = G4_Eu
  specific = 4
FEATURE [App::DocumentObjectGroupPython] Gd_element002  label="Gd_element : 1"  # scripted group (container) (typed FeaturePython)
  n = 1
  ref = Gd_element
FEATURE [App::DocumentObjectGroupPython] G4_Gd  # scripted group (container) (typed FeaturePython)
  Dunit = g/cm3
  Dvalue = 7.9004
  Group = -> [Gd_element002]
  conduct = 2
  density = 1
  expand = 3
  formula = Gd
  name = G4_Gd
  specific = 4
FEATURE [App::DocumentObjectGroupPython] Tb_element001  label="Tb_element : 1"  # scripted group (container) (typed FeaturePython)
  n = 1
  ref = Tb_element
FEATURE [App::DocumentObjectGroupPython] G4_Tb  # scripted group (container) (typed FeaturePython)
  Dunit = g/cm3
  Dvalue = 8.229
  Group = -> [Tb_element001]
  conduct = 2
  density = 1
  expand = 3
  formula = Tb
  name = G4_Tb
  specific = 4
FEATURE [App::DocumentObjectGroupPython] Dy_element001  label="Dy_element : 1"  # scripted group (container) (typed FeaturePython)
  n = 1
  ref = Dy_element
FEATURE [App::DocumentObjectGroupPython] G4_Dy  # scripted group (container) (typed FeaturePython)
  Dunit = g/cm3
  Dvalue = 8.55
  Group = -> [Dy_element001]
  conduct = 2
  density = 1
  expand = 3
  formula = Dy
  name = G4_Dy
  specific = 4
FEATURE [App::DocumentObjectGroupPython] Ho_element001  label="Ho_element : 1"  # scripted group (container) (typed FeaturePython)
  n = 1
  ref = Ho_element
FEATURE [App::DocumentObjectGroupPython] G4_Ho  # scripted group (container) (typed FeaturePython)
  Dunit = g/cm3
  Dvalue = 8.795
  Group = -> [Ho_element001]
  conduct = 2
  density = 1
  expand = 3
  formula = Ho
  name = G4_Ho
  specific = 4
FEATURE [App::DocumentObjectGroupPython] Er_element001  label="Er_element : 1"  # scripted group (container) (typed FeaturePython)
  n = 1
  ref = Er_element
FEATURE [App::DocumentObjectGroupPython] G4_Er  # scripted group (container) (typed FeaturePython)
  Dunit = g/cm3
  Dvalue = 9.066
  Group = -> [Er_element001]
  conduct = 2
  density = 1
  expand = 3
  formula = Er
  name = G4_Er
  specific = 4
FEATURE [App::DocumentObjectGroupPython] Tm_element001  label="Tm_element : 1"  # scripted group (container) (typed FeaturePython)
  n = 1
  ref = Tm_element
FEATURE [App::DocumentObjectGroupPython] G4_Tm  # scripted group (container) (typed FeaturePython)
  Dunit = g/cm3
  Dvalue = 9.321
  Group = -> [Tm_element001]
  conduct = 2
  density = 1
  expand = 3
  formula = Tm
  name = G4_Tm
  specific = 4
FEATURE [App::DocumentObjectGroupPython] Yb_element001  label="Yb_element : 1"  # scripted group (container) (typed FeaturePython)
  n = 1
  ref = Yb_element
FEATURE [App::DocumentObjectGroupPython] G4_Yb  # scripted group (container) (typed FeaturePython)
  Dunit = g/cm3
  Dvalue = 6.73
  Group = -> [Yb_element001]
  conduct = 2
  density = 1
  expand = 3
  formula = Yb
  name = G4_Yb
  specific = 4
FEATURE [App::DocumentObjectGroupPython] Lu_element001  label="Lu_element : 1"  # scripted group (container) (typed FeaturePython)
  n = 1
  ref = Lu_element
FEATURE [App::DocumentObjectGroupPython] G4_Lu  # scripted group (container) (typed FeaturePython)
  Dunit = g/cm3
  Dvalue = 9.84
  Group = -> [Lu_element001]
  conduct = 2
  density = 1
  expand = 3
  formula = Lu
  name = G4_Lu
  specific = 4
FEATURE [App::DocumentObjectGroupPython] Hf_element001  label="Hf_element : 1"  # scripted group (container) (typed FeaturePython)
  n = 1
  ref = Hf_element
FEATURE [App::DocumentObjectGroupPython] G4_Hf  # scripted group (container) (typed FeaturePython)
  Dunit = g/cm3
  Dvalue = 13.31
  Group = -> [Hf_element001]
  conduct = 2
  density = 1
  expand = 3
  formula = Hf
  name = G4_Hf
  specific = 4
FEATURE [App::DocumentObjectGroupPython] Ta_element001  label="Ta_element : 1"  # scripted group (container) (typed FeaturePython)
  n = 1
  ref = Ta_element
FEATURE [App::DocumentObjectGroupPython] G4_Ta  # scripted group (container) (typed FeaturePython)
  Dunit = g/cm3
  Dvalue = 16.654
  Group = -> [Ta_element001]
  conduct = 2
  density = 1
  expand = 3
  formula = Ta
  name = G4_Ta
  specific = 4
FEATURE [App::DocumentObjectGroupPython] W_element004  label="W_element : 004"  # scripted group (container) (typed FeaturePython)
  n = 1
  ref = W_element
FEATURE [App::DocumentObjectGroupPython] G4_W  # scripted group (container) (typed FeaturePython)
  Dunit = g/cm3
  Dvalue = 19.3
  Group = -> [W_element004]
  conduct = 2
  density = 1
  expand = 3
  formula = W
  name = G4_W
  specific = 4
FEATURE [App::DocumentObjectGroupPython] Re_element001  label="Re_element : 1"  # scripted group (container) (typed FeaturePython)
  n = 1
  ref = Re_element
FEATURE [App::DocumentObjectGroupPython] G4_Re  # scripted group (container) (typed FeaturePython)
  Dunit = g/cm3
  Dvalue = 21.02
  Group = -> [Re_element001]
  conduct = 2
  density = 1
  expand = 3
  formula = Re
  name = G4_Re
  specific = 4
FEATURE [App::DocumentObjectGroupPython] Os_element001  label="Os_element : 1"  # scripted group (container) (typed FeaturePython)
  n = 1
  ref = Os_element
FEATURE [App::DocumentObjectGroupPython] G4_Os  # scripted group (container) (typed FeaturePython)
  Dunit = g/cm3
  Dvalue = 22.57
  Group = -> [Os_element001]
  conduct = 2
  density = 1
  expand = 3
  formula = Os
  name = G4_Os
  specific = 4
FEATURE [App::DocumentObjectGroupPython] Ir_element001  label="Ir_element : 1"  # scripted group (container) (typed FeaturePython)
  n = 1
  ref = Ir_element
FEATURE [App::DocumentObjectGroupPython] G4_Ir  # scripted group (container) (typed FeaturePython)
  Dunit = g/cm3
  Dvalue = 22.42
  Group = -> [Ir_element001]
  conduct = 2
  density = 1
  expand = 3
  formula = Ir
  name = G4_Ir
  specific = 4
FEATURE [App::DocumentObjectGroupPython] Pt_element001  label="Pt_element : 1"  # scripted group (container) (typed FeaturePython)
  n = 1
  ref = Pt_element
FEATURE [App::DocumentObjectGroupPython] G4_Pt  # scripted group (container) (typed FeaturePython)
  Dunit = g/cm3
  Dvalue = 21.45
  Group = -> [Pt_element001]
  conduct = 2
  density = 1
  expand = 3
  formula = Pt
  name = G4_Pt
  specific = 4
FEATURE [App::DocumentObjectGroupPython] Au_element001  label="Au_element : 1"  # scripted group (container) (typed FeaturePython)
  n = 1
  ref = Au_element
FEATURE [App::DocumentObjectGroupPython] G4_Au  # scripted group (container) (typed FeaturePython)
  Dunit = g/cm3
  Dvalue = 19.32
  Group = -> [Au_element001]
  conduct = 2
  density = 1
  expand = 3
  formula = Au
  name = G4_Au
  specific = 4
FEATURE [App::DocumentObjectGroupPython] Hg_element002  label="Hg_element : 002"  # scripted group (container) (typed FeaturePython)
  n = 1
  ref = Hg_element
FEATURE [App::DocumentObjectGroupPython] G4_Hg  # scripted group (container) (typed FeaturePython)
  Dunit = g/cm3
  Dvalue = 13.546
  Group = -> [Hg_element002]
  conduct = 2
  density = 1
  expand = 3
  formula = Hg
  name = G4_Hg
  specific = 4
FEATURE [App::DocumentObjectGroupPython] Tl_element002  label="Tl_element : 002"  # scripted group (container) (typed FeaturePython)
  n = 1
  ref = Tl_element
FEATURE [App::DocumentObjectGroupPython] G4_Tl  # scripted group (container) (typed FeaturePython)
  Dunit = g/cm3
  Dvalue = 11.72
  Group = -> [Tl_element002]
  conduct = 2
  density = 1
  expand = 3
  formula = Tl
  name = G4_Tl
  specific = 4
FEATURE [App::DocumentObjectGroupPython] Pb_element003  label="Pb_element : 1"  # scripted group (container) (typed FeaturePython)
  n = 1
  ref = Pb_element
FEATURE [App::DocumentObjectGroupPython] G4_Pb  # scripted group (container) (typed FeaturePython)
  Dunit = g/cm3
  Dvalue = 11.35
  Group = -> [Pb_element003]
  conduct = 2
  density = 1
  expand = 3
  formula = Pb
  name = G4_Pb
  specific = 4
FEATURE [App::DocumentObjectGroupPython] Bi_element002  label="Bi_element : 1"  # scripted group (container) (typed FeaturePython)
  n = 1
  ref = Bi_element
FEATURE [App::DocumentObjectGroupPython] G4_Bi  # scripted group (container) (typed FeaturePython)
  Dunit = g/cm3
  Dvalue = 9.747
  Group = -> [Bi_element002]
  conduct = 2
  density = 1
  expand = 3
  formula = Bi
  name = G4_Bi
  specific = 4
FEATURE [App::DocumentObjectGroupPython] Po_element001  label="Po_element : 1"  # scripted group (container) (typed FeaturePython)
  n = 1
  ref = Po_element
FEATURE [App::DocumentObjectGroupPython] G4_Po  # scripted group (container) (typed FeaturePython)
  Dunit = g/cm3
  Dvalue = 9.32
  Group = -> [Po_element001]
  conduct = 2
  density = 1
  expand = 3
  formula = Po
  name = G4_Po
  specific = 4
FEATURE [App::DocumentObjectGroupPython] At_element001  label="At_element : 1"  # scripted group (container) (typed FeaturePython)
  n = 1
  ref = At_element
FEATURE [App::DocumentObjectGroupPython] G4_At  # scripted group (container) (typed FeaturePython)
  Dunit = g/cm3
  Dvalue = 9.32
  Group = -> [At_element001]
  conduct = 2
  density = 1
  expand = 3
  formula = At
  name = G4_At
  specific = 4
FEATURE [App::DocumentObjectGroupPython] Rn_element001  label="Rn_element : 1"  # scripted group (container) (typed FeaturePython)
  n = 1
  ref = Rn_element
FEATURE [App::DocumentObjectGroupPython] G4_Rn  # scripted group (container) (typed FeaturePython)
  Dunit = g/cm3
  Dvalue = 0.00900662
  Group = -> [Rn_element001]
  conduct = 2
  density = 1
  expand = 3
  formula = Rn
  name = G4_Rn
  specific = 4
FEATURE [App::DocumentObjectGroupPython] Fr_element001  label="Fr_element : 1"  # scripted group (container) (typed FeaturePython)
  n = 1
  ref = Fr_element
FEATURE [App::DocumentObjectGroupPython] G4_Fr  # scripted group (container) (typed FeaturePython)
  Dunit = g/cm3
  Dvalue = 1
  Group = -> [Fr_element001]
  conduct = 2
  density = 1
  expand = 3
  formula = Fr
  name = G4_Fr
  specific = 4
FEATURE [App::DocumentObjectGroupPython] Ra_element001  label="Ra_element : 1"  # scripted group (container) (typed FeaturePython)
  n = 1
  ref = Ra_element
FEATURE [App::DocumentObjectGroupPython] G4_Ra  # scripted group (container) (typed FeaturePython)
  Dunit = g/cm3
  Dvalue = 5
  Group = -> [Ra_element001]
  conduct = 2
  density = 1
  expand = 3
  formula = Ra
  name = G4_Ra
  specific = 4
FEATURE [App::DocumentObjectGroupPython] Ac_element001  label="Ac_element : 1"  # scripted group (container) (typed FeaturePython)
  n = 1
  ref = Ac_element
FEATURE [App::DocumentObjectGroupPython] G4_Ac  # scripted group (container) (typed FeaturePython)
  Dunit = g/cm3
  Dvalue = 10.07
  Group = -> [Ac_element001]
  conduct = 2
  density = 1
  expand = 3
  formula = Ac
  name = G4_Ac
  specific = 4
FEATURE [App::DocumentObjectGroupPython] Th_element001  label="Th_element : 1"  # scripted group (container) (typed FeaturePython)
  n = 1
  ref = Th_element
FEATURE [App::DocumentObjectGroupPython] G4_Th  # scripted group (container) (typed FeaturePython)
  Dunit = g/cm3
  Dvalue = 11.72
  Group = -> [Th_element001]
  conduct = 2
  density = 1
  expand = 3
  formula = Th
  name = G4_Th
  specific = 4
FEATURE [App::DocumentObjectGroupPython] Pa_element001  label="Pa_element : 1"  # scripted group (container) (typed FeaturePython)
  n = 1
  ref = Pa_element
FEATURE [App::DocumentObjectGroupPython] G4_Pa  # scripted group (container) (typed FeaturePython)
  Dunit = g/cm3
  Dvalue = 15.37
  Group = -> [Pa_element001]
  conduct = 2
  density = 1
  expand = 3
  formula = Pa
  name = G4_Pa
  specific = 4
FEATURE [App::DocumentObjectGroupPython] U_element004  label="U_element : 004"  # scripted group (container) (typed FeaturePython)
  n = 1
  ref = U_element
FEATURE [App::DocumentObjectGroupPython] G4_U  # scripted group (container) (typed FeaturePython)
  Dunit = g/cm3
  Dvalue = 18.95
  Group = -> [U_element004]
  conduct = 2
  density = 1
  expand = 3
  formula = U
  name = G4_U
  specific = 4
FEATURE [App::DocumentObjectGroupPython] Np_element001  label="Np_element : 1"  # scripted group (container) (typed FeaturePython)
  n = 1
  ref = Np_element
FEATURE [App::DocumentObjectGroupPython] G4_Np  # scripted group (container) (typed FeaturePython)
  Dunit = g/cm3
  Dvalue = 20.25
  Group = -> [Np_element001]
  conduct = 2
  density = 1
  expand = 3
  formula = Np
  name = G4_Np
  specific = 4
FEATURE [App::DocumentObjectGroupPython] Pu_element002  label="Pu_element : 002"  # scripted group (container) (typed FeaturePython)
  n = 1
  ref = Pu_element
FEATURE [App::DocumentObjectGroupPython] G4_Pu  # scripted group (container) (typed FeaturePython)
  Dunit = g/cm3
  Dvalue = 19.84
  Group = -> [Pu_element002]
  conduct = 2
  density = 1
  expand = 3
  formula = Pu
  name = G4_Pu
  specific = 4
FEATURE [App::DocumentObjectGroupPython] Am_element001  label="Am_element : 1"  # scripted group (container) (typed FeaturePython)
  n = 1
  ref = Am_element
FEATURE [App::DocumentObjectGroupPython] G4_Am  # scripted group (container) (typed FeaturePython)
  Dunit = g/cm3
  Dvalue = 13.67
  Group = -> [Am_element001]
  conduct = 2
  density = 1
  expand = 3
  formula = Am
  name = G4_Am
  specific = 4
FEATURE [App::DocumentObjectGroupPython] Cm_element001  label="Cm_element : 1"  # scripted group (container) (typed FeaturePython)
  n = 1
  ref = Cm_element
FEATURE [App::DocumentObjectGroupPython] G4_Cm  # scripted group (container) (typed FeaturePython)
  Dunit = g/cm3
  Dvalue = 13.51
  Group = -> [Cm_element001]
  conduct = 2
  density = 1
  expand = 3
  formula = Cm
  name = G4_Cm
  specific = 4
FEATURE [App::DocumentObjectGroupPython] Bk_element001  label="Bk_element : 1"  # scripted group (container) (typed FeaturePython)
  n = 1
  ref = Bk_element
FEATURE [App::DocumentObjectGroupPython] G4_Bk  # scripted group (container) (typed FeaturePython)
  Dunit = g/cm3
  Dvalue = 14
  Group = -> [Bk_element001]
  conduct = 2
  density = 1
  expand = 3
  formula = Bk
  name = G4_Bk
  specific = 4
FEATURE [App::DocumentObjectGroupPython] Cf_element001  label="Cf_element : 1"  # scripted group (container) (typed FeaturePython)
  n = 1
  ref = Cf_element
FEATURE [App::DocumentObjectGroupPython] G4_Cf  # scripted group (container) (typed FeaturePython)
  Dunit = g/cm3
  Dvalue = 10
  Group = -> [Cf_element001]
  conduct = 2
  density = 1
  expand = 3
  formula = Cf
  name = G4_Cf
  specific = 4
FEATURE [App::DocumentObjectGroupPython] Element  # scripted group (container) (typed FeaturePython)
  Group = -> [G4_H,G4_He,G4_Li,G4_Be,G4_B,G4_C,G4_N,G4_O,G4_F,G4_Ne,G4_Na,G4_Mg,G4_Al,G4_Si,G4_P,G4_S,G4_Cl,G4_Ar,G4_K,G4_Ca,G4_Sc,G4_Ti,G4_V,G4_Cr,G4_Mn,G4_Fe,G4_Co,G4_Ni,G4_Cu,G4_Zn,G4_Ga,G4_Ge,G4_As,G4_Se,G4_Br,G4_Kr,G4_Rb,G4_Sr,G4_Y,G4_Zr,G4_Nb,G4_Mo,G4_Tc,G4_Ru,G4_Rh,G4_Pd,G4_Ag,G4_Cd,G4_In,G4_Sn,G4_Sb,G4_Te,G4_I,G4_Xe,G4_Cs,G4_Ba,G4_La,G4_Ce,G4_Pr,G4_Nd,G4_Pm,G4_Sm,G4_Eu,G4_Gd,G4_Tb,G4_Dy,G4_Ho,G4_Er,+30 more]
FEATURE [App::DocumentObjectGroupPython] H_element114  label="H_element : 063"  # scripted group (container) (typed FeaturePython)
  n = 2
  ref = H_element
FEATURE [App::DocumentObjectGroupPython] G4_lH2  # scripted group (container) (typed FeaturePython)
  Dunit = g/cm3
  Dvalue = 0.0708
  Group = -> [H_element114]
  conduct = 2
  density = 1
  expand = 3
  formula = G4_lH2
  name = G4_lH2
  specific = 4
FEATURE [App::DocumentObjectGroupPython] N_element049  label="N_element : 022"  # scripted group (container) (typed FeaturePython)
  n = 2
  ref = N_element
FEATURE [App::DocumentObjectGroupPython] G4_lN2  # scripted group (container) (typed FeaturePython)
  Dunit = g/cm3
  Dvalue = 0.807
  Group = -> [N_element049]
  conduct = 2
  density = 1
  expand = 3
  formula = G4_lN2
  name = G4_lN2
  specific = 4
FEATURE [App::DocumentObjectGroupPython] O_element106  label="O_element : 060"  # scripted group (container) (typed FeaturePython)
  n = 2
  ref = O_element
FEATURE [App::DocumentObjectGroupPython] G4_lO2  # scripted group (container) (typed FeaturePython)
  Dunit = g/cm3
  Dvalue = 1.141
  Group = -> [O_element106]
  conduct = 2
  density = 1
  expand = 3
  formula = G4_lO2
  name = G4_lO2
  specific = 4
FEATURE [App::DocumentObjectGroupPython] Ar_element003  label="Ar_element : 002"  # scripted group (container) (typed FeaturePython)
  n = 1
  ref = Ar_element
FEATURE [App::DocumentObjectGroupPython] G4_lAr  # scripted group (container) (typed FeaturePython)
  Dunit = g/cm3
  Dvalue = 1.396
  Group = -> [Ar_element003]
  conduct = 2
  density = 1
  expand = 3
  formula = G4_lAr
  name = G4_lAr
  specific = 4
FEATURE [App::DocumentObjectGroupPython] Br_element008  label="Br_element : 005"  # scripted group (container) (typed FeaturePython)
  n = 1
  ref = Br_element
FEATURE [App::DocumentObjectGroupPython] G4_lBr  # scripted group (container) (typed FeaturePython)
  Dunit = g/cm3
  Dvalue = 3.1028
  Group = -> [Br_element008]
  conduct = 2
  density = 1
  expand = 3
  formula = G4_lBr
  name = G4_lBr
  specific = 4
FEATURE [App::DocumentObjectGroupPython] Kr_element002  label="Kr_element : 002"  # scripted group (container) (typed FeaturePython)
  n = 1
  ref = Kr_element
FEATURE [App::DocumentObjectGroupPython] G4_lKr  # scripted group (container) (typed FeaturePython)
  Dunit = g/cm3
  Dvalue = 2.418
  Group = -> [Kr_element002]
  conduct = 2
  density = 1
  expand = 3
  formula = G4_lKr
  name = G4_lKr
  specific = 4
FEATURE [App::DocumentObjectGroupPython] Xe_element002  label="Xe_element : 002"  # scripted group (container) (typed FeaturePython)
  n = 1
  ref = Xe_element
FEATURE [App::DocumentObjectGroupPython] G4_lXe  # scripted group (container) (typed FeaturePython)
  Dunit = g/cm3
  Dvalue = 2.953
  Group = -> [Xe_element002]
  conduct = 2
  density = 1
  expand = 3
  formula = G4_lXe
  name = G4_lXe
  specific = 4
FEATURE [App::DocumentObjectGroupPython] O_element107  label="O_element : 061"  # scripted group (container) (typed FeaturePython)
  n = 4
  ref = O_element
FEATURE [App::DocumentObjectGroupPython] Pb_element004  label="Pb_element : 002"  # scripted group (container) (typed FeaturePython)
  n = 1
  ref = Pb_element
FEATURE [App::DocumentObjectGroupPython] W_element005  label="W_element : 005"  # scripted group (container) (typed FeaturePython)
  n = 1
  ref = W_element
FEATURE [App::DocumentObjectGroupPython] G4_PbWO4  # scripted group (container) (typed FeaturePython)
  Dunit = g/cm3
  Dvalue = 8.28
  Group = -> [O_element107,Pb_element004,W_element005]
  conduct = 2
  density = 1
  expand = 3
  formula = G4_PbWO4
  name = G4_PbWO4
  specific = 4
FEATURE [App::DocumentObjectGroupPython] H_element115  label="H_element : 064"  # scripted group (container) (typed FeaturePython)
  n = 1
  ref = H_element
FEATURE [App::DocumentObjectGroupPython] G4_Galactic  # scripted group (container) (typed FeaturePython)
  Dunit = g/cm3
  Dvalue = 0
  Group = -> [H_element115]
  conduct = 2
  density = 1
  expand = 3
  formula = G4_Galactic
  name = G4_Galactic
  specific = 4
FEATURE [App::DocumentObjectGroupPython] C_element125  label="C_element : 071"  # scripted group (container) (typed FeaturePython)
  n = 1
  ref = C_element
FEATURE [App::DocumentObjectGroupPython] G4_GRAPHITE_POROUS  # scripted group (container) (typed FeaturePython)
  Dunit = g/cm3
  Dvalue = 1.7
  Group = -> [C_element125]
  conduct = 2
  density = 1
  expand = 3
  formula = G4_GRAPHITE_POROUS
  name = G4_GRAPHITE_POROUS
  specific = 4
FEATURE [App::DocumentObjectGroupPython] H_element116  label="H_element : 0.150"  # scripted group (container) (typed FeaturePython)
  n = 0.080538
FEATURE [App::DocumentObjectGroupPython] C_element126  label="C_element : 0.600"  # scripted group (container) (typed FeaturePython)
  n = 0.599848
FEATURE [App::DocumentObjectGroupPython] O_element108  label="O_element : 0.320"  # scripted group (container) (typed FeaturePython)
  n = 0.319614
FEATURE [App::DocumentObjectGroupPython] G4_LUCITE  # scripted group (container) (typed FeaturePython)
  Dunit = g/cm3
  Dvalue = 1.19
  Group = -> [H_element116,C_element126,O_element108]
  conduct = 2
  density = 1
  expand = 3
  formula = G4_LUCITE
  name = G4_LUCITE
  specific = 4
FEATURE [App::DocumentObjectGroupPython] Cu_element002  label="Cu_element : 62"  # scripted group (container) (typed FeaturePython)
  n = 62
  ref = Cu_element
FEATURE [App::DocumentObjectGroupPython] Zn_element002  label="Zn_element : 35"  # scripted group (container) (typed FeaturePython)
  n = 35
  ref = Zn_element
FEATURE [App::DocumentObjectGroupPython] Pb_element005  label="Pb_element : 3"  # scripted group (container) (typed FeaturePython)
  n = 3
  ref = Pb_element
FEATURE [App::DocumentObjectGroupPython] G4_BRASS  # scripted group (container) (typed FeaturePython)
  Dunit = g/cm3
  Dvalue = 8.52
  Group = -> [Cu_element002,Zn_element002,Pb_element005]
  conduct = 2
  density = 1
  expand = 3
  formula = G4_BRASS
  name = G4_BRASS
  specific = 4
FEATURE [App::DocumentObjectGroupPython] Cu_element003  label="Cu_element : 89"  # scripted group (container) (typed FeaturePython)
  n = 89
  ref = Cu_element
FEATURE [App::DocumentObjectGroupPython] Zn_element003  label="Zn_element : 9"  # scripted group (container) (typed FeaturePython)
  n = 9
  ref = Zn_element
FEATURE [App::DocumentObjectGroupPython] Pb_element006  label="Pb_element : 2"  # scripted group (container) (typed FeaturePython)
  n = 2
  ref = Pb_element
FEATURE [App::DocumentObjectGroupPython] G4_BRONZE  # scripted group (container) (typed FeaturePython)
  Dunit = g/cm3
  Dvalue = 8.82
  Group = -> [Cu_element003,Zn_element003,Pb_element006]
  conduct = 2
  density = 1
  expand = 3
  formula = G4_BRONZE
  name = G4_BRONZE
  specific = 4
FEATURE [App::DocumentObjectGroupPython] Fe_element008  label="Fe_element : 74"  # scripted group (container) (typed FeaturePython)
  n = 74
  ref = Fe_element
FEATURE [App::DocumentObjectGroupPython] Cr_element002  label="Cr_element : 18"  # scripted group (container) (typed FeaturePython)
  n = 18
  ref = Cr_element
FEATURE [App::DocumentObjectGroupPython] Ni_element002  label="Ni_element : 8"  # scripted group (container) (typed FeaturePython)
  n = 8
  ref = Ni_element
FEATURE [App::DocumentObjectGroupPython] G4_STAINLESS_STEEL  label="G4_STAINLESS-STEEL"  # scripted group (container) (typed FeaturePython)
  Dunit = g/cm3
  Dvalue = 8
  Group = -> [Fe_element008,Cr_element002,Ni_element002]
  conduct = 2
  density = 1
  expand = 3
  formula = G4_STAINLESS-STEEL
  name = G4_STAINLESS-STEEL
  specific = 4
FEATURE [App::DocumentObjectGroupPython] H_element117  label="H_element : 065"  # scripted group (container) (typed FeaturePython)
  n = 18
  ref = H_element
FEATURE [App::DocumentObjectGroupPython] C_element127  label="C_element : 072"  # scripted group (container) (typed FeaturePython)
  n = 12
  ref = C_element
FEATURE [App::DocumentObjectGroupPython] O_element109  label="O_element : 062"  # scripted group (container) (typed FeaturePython)
  n = 7
  ref = O_element
FEATURE [App::DocumentObjectGroupPython] G4_CR39  # scripted group (container) (typed FeaturePython)
  Dunit = g/cm3
  Dvalue = 1.32
  Group = -> [H_element117,C_element127,O_element109]
  conduct = 2
  density = 1
  expand = 3
  formula = G4_CR39
  name = G4_CR39
  specific = 4
FEATURE [App::DocumentObjectGroupPython] H_element118  label="H_element : 38"  # scripted group (container) (typed FeaturePython)
  n = 38
  ref = H_element
FEATURE [App::DocumentObjectGroupPython] C_element128  label="C_element : 073"  # scripted group (container) (typed FeaturePython)
  n = 18
  ref = C_element
FEATURE [App::DocumentObjectGroupPython] O_element110  label="O_element : 063"  # scripted group (container) (typed FeaturePython)
  n = 1
  ref = O_element
FEATURE [App::DocumentObjectGroupPython] G4_OCTADECANOL  # scripted group (container) (typed FeaturePython)
  Dunit = g/cm3
  Dvalue = 0.812
  Group = -> [H_element118,C_element128,O_element110]
  conduct = 2
  density = 1
  expand = 3
  formula = G4_OCTADECANOL
  name = G4_OCTADECANOL
  specific = 4
FEATURE [App::DocumentObjectGroupPython] HEP  # scripted group (container) (typed FeaturePython)
  Group = -> [G4_lH2,G4_lN2,G4_lO2,G4_lAr,G4_lBr,G4_lKr,G4_lXe,G4_PbWO4,G4_Galactic,G4_GRAPHITE_POROUS,G4_LUCITE,G4_BRASS,G4_BRONZE,G4_STAINLESS_STEEL,G4_CR39,G4_OCTADECANOL]
FEATURE [App::DocumentObjectGroupPython] C_element129  label="C_element : 074"  # scripted group (container) (typed FeaturePython)
  n = 14
  ref = C_element
FEATURE [App::DocumentObjectGroupPython] H_element119  label="H_element : 066"  # scripted group (container) (typed FeaturePython)
  n = 10
  ref = H_element
FEATURE [App::DocumentObjectGroupPython] O_element111  label="O_element : 064"  # scripted group (container) (typed FeaturePython)
  n = 2
  ref = O_element
FEATURE [App::DocumentObjectGroupPython] N_element050  label="N_element : 023"  # scripted group (container) (typed FeaturePython)
  n = 2
  ref = N_element
FEATURE [App::DocumentObjectGroupPython] G4_KEVLAR  # scripted group (container) (typed FeaturePython)
  Dunit = g/cm3
  Dvalue = 1.44
  Group = -> [C_element129,H_element119,O_element111,N_element050]
  conduct = 2
  density = 1
  expand = 3
  formula = G4_KEVLAR
  name = G4_KEVLAR
  specific = 4
FEATURE [App::DocumentObjectGroupPython] C_element130  label="C_element : 075"  # scripted group (container) (typed FeaturePython)
  n = 10
  ref = C_element
FEATURE [App::DocumentObjectGroupPython] H_element120  label="H_element : 067"  # scripted group (container) (typed FeaturePython)
  n = 8
  ref = H_element
FEATURE [App::DocumentObjectGroupPython] O_element112  label="O_element : 065"  # scripted group (container) (typed FeaturePython)
  n = 4
  ref = O_element
FEATURE [App::DocumentObjectGroupPython] G4_DACRON  # scripted group (container) (typed FeaturePython)
  Dunit = g/cm3
  Dvalue = 1.4
  Group = -> [C_element130,H_element120,O_element112]
  conduct = 2
  density = 1
  expand = 3
  formula = G4_DACRON
  name = G4_DACRON
  specific = 4
FEATURE [App::DocumentObjectGroupPython] C_element131  label="C_element : 076"  # scripted group (container) (typed FeaturePython)
  n = 4
  ref = C_element
FEATURE [App::DocumentObjectGroupPython] H_element121  label="H_element : 068"  # scripted group (container) (typed FeaturePython)
  n = 5
  ref = H_element
FEATURE [App::DocumentObjectGroupPython] Cl_element030  label="Cl_element : 016"  # scripted group (container) (typed FeaturePython)
  n = 1
  ref = Cl_element
FEATURE [App::DocumentObjectGroupPython] G4_NEOPRENE  # scripted group (container) (typed FeaturePython)
  Dunit = g/cm3
  Dvalue = 1.23
  Group = -> [C_element131,H_element121,Cl_element030]
  conduct = 2
  density = 1
  expand = 3
  formula = G4_NEOPRENE
  name = G4_NEOPRENE
  specific = 4
FEATURE [App::DocumentObjectGroupPython] Space  # scripted group (container) (typed FeaturePython)
  Group = -> [G4_KEVLAR,G4_DACRON,G4_NEOPRENE]
FEATURE [App::DocumentObjectGroupPython] H_element122  label="H_element : 069"  # scripted group (container) (typed FeaturePython)
  n = 5
  ref = H_element
FEATURE [App::DocumentObjectGroupPython] C_element132  label="C_element : 077"  # scripted group (container) (typed FeaturePython)
  n = 4
  ref = C_element
FEATURE [App::DocumentObjectGroupPython] N_element051  label="N_element : 3"  # scripted group (container) (typed FeaturePython)
  n = 3
  ref = N_element
FEATURE [App::DocumentObjectGroupPython] O_element113  label="O_element : 066"  # scripted group (container) (typed FeaturePython)
  n = 1
  ref = O_element
FEATURE [App::DocumentObjectGroupPython] G4_CYTOSINE  # scripted group (container) (typed FeaturePython)
  Dunit = g/cm3
  Dvalue = 1.55
  Group = -> [H_element122,C_element132,N_element051,O_element113]
  conduct = 2
  density = 1
  expand = 3
  formula = G4_CYTOSINE
  name = G4_CYTOSINE
  specific = 4
FEATURE [App::DocumentObjectGroupPython] H_element123  label="H_element : 070"  # scripted group (container) (typed FeaturePython)
  n = 6
  ref = H_element
FEATURE [App::DocumentObjectGroupPython] C_element133  label="C_element : 078"  # scripted group (container) (typed FeaturePython)
  n = 5
  ref = C_element
FEATURE [App::DocumentObjectGroupPython] N_element052  label="N_element : 024"  # scripted group (container) (typed FeaturePython)
  n = 2
  ref = N_element
FEATURE [App::DocumentObjectGroupPython] O_element114  label="O_element : 067"  # scripted group (container) (typed FeaturePython)
  n = 2
  ref = O_element
FEATURE [App::DocumentObjectGroupPython] G4_THYMINE  # scripted group (container) (typed FeaturePython)
  Dunit = g/cm3
  Dvalue = 1.23
  Group = -> [H_element123,C_element133,N_element052,O_element114]
  conduct = 2
  density = 1
  expand = 3
  formula = G4_THYMINE
  name = G4_THYMINE
  specific = 4
FEATURE [App::DocumentObjectGroupPython] H_element124  label="H_element : 071"  # scripted group (container) (typed FeaturePython)
  n = 4
  ref = H_element
FEATURE [App::DocumentObjectGroupPython] C_element134  label="C_element : 079"  # scripted group (container) (typed FeaturePython)
  n = 4
  ref = C_element
FEATURE [App::DocumentObjectGroupPython] N_element053  label="N_element : 025"  # scripted group (container) (typed FeaturePython)
  n = 2
  ref = N_element
FEATURE [App::DocumentObjectGroupPython] O_element115  label="O_element : 068"  # scripted group (container) (typed FeaturePython)
  n = 2
  ref = O_element
FEATURE [App::DocumentObjectGroupPython] G4_URACIL  # scripted group (container) (typed FeaturePython)
  Dunit = g/cm3
  Dvalue = 1.32
  Group = -> [H_element124,C_element134,N_element053,O_element115]
  conduct = 2
  density = 1
  expand = 3
  formula = G4_URACIL
  name = G4_URACIL
  specific = 4
FEATURE [App::DocumentObjectGroupPython] H_element125  label="H_element : 072"  # scripted group (container) (typed FeaturePython)
  n = 4
  ref = H_element
FEATURE [App::DocumentObjectGroupPython] C_element135  label="C_element : 080"  # scripted group (container) (typed FeaturePython)
  n = 5
  ref = C_element
FEATURE [App::DocumentObjectGroupPython] N_element054  label="N_element : 026"  # scripted group (container) (typed FeaturePython)
  n = 5
  ref = N_element
FEATURE [App::DocumentObjectGroupPython] G4_DNA_ADENINE  # scripted group (container) (typed FeaturePython)
  Dunit = g/cm3
  Dvalue = 1
  Group = -> [H_element125,C_element135,N_element054]
  conduct = 2
  density = 1
  expand = 3
  formula = G4_DNA_ADENINE
  name = G4_DNA_ADENINE
  specific = 4
FEATURE [App::DocumentObjectGroupPython] H_element126  label="H_element : 073"  # scripted group (container) (typed FeaturePython)
  n = 4
  ref = H_element
FEATURE [App::DocumentObjectGroupPython] C_element136  label="C_element : 081"  # scripted group (container) (typed FeaturePython)
  n = 5
  ref = C_element
FEATURE [App::DocumentObjectGroupPython] N_element055  label="N_element : 027"  # scripted group (container) (typed FeaturePython)
  n = 5
  ref = N_element
FEATURE [App::DocumentObjectGroupPython] O_element116  label="O_element : 069"  # scripted group (container) (typed FeaturePython)
  n = 1
  ref = O_element
FEATURE [App::DocumentObjectGroupPython] G4_DNA_GUANINE  # scripted group (container) (typed FeaturePython)
  Dunit = g/cm3
  Dvalue = 1
  Group = -> [H_element126,C_element136,N_element055,O_element116]
  conduct = 2
  density = 1
  expand = 3
  formula = G4_DNA_GUANINE
  name = G4_DNA_GUANINE
  specific = 4
FEATURE [App::DocumentObjectGroupPython] H_element127  label="H_element : 074"  # scripted group (container) (typed FeaturePython)
  n = 4
  ref = H_element
FEATURE [App::DocumentObjectGroupPython] C_element137  label="C_element : 082"  # scripted group (container) (typed FeaturePython)
  n = 4
  ref = C_element
FEATURE [App::DocumentObjectGroupPython] N_element056  label="N_element : 028"  # scripted group (container) (typed FeaturePython)
  n = 3
  ref = N_element
FEATURE [App::DocumentObjectGroupPython] O_element117  label="O_element : 070"  # scripted group (container) (typed FeaturePython)
  n = 1
  ref = O_element
FEATURE [App::DocumentObjectGroupPython] G4_DNA_CYTOSINE  # scripted group (container) (typed FeaturePython)
  Dunit = g/cm3
  Dvalue = 1
  Group = -> [H_element127,C_element137,N_element056,O_element117]
  conduct = 2
  density = 1
  expand = 3
  formula = G4_DNA_CYTOSINE
  name = G4_DNA_CYTOSINE
  specific = 4
FEATURE [App::DocumentObjectGroupPython] H_element128  label="H_element : 075"  # scripted group (container) (typed FeaturePython)
  n = 5
  ref = H_element
FEATURE [App::DocumentObjectGroupPython] C_element138  label="C_element : 083"  # scripted group (container) (typed FeaturePython)
  n = 5
  ref = C_element
FEATURE [App::DocumentObjectGroupPython] N_element057  label="N_element : 029"  # scripted group (container) (typed FeaturePython)
  n = 2
  ref = N_element
FEATURE [App::DocumentObjectGroupPython] O_element118  label="O_element : 071"  # scripted group (container) (typed FeaturePython)
  n = 2
  ref = O_element
FEATURE [App::DocumentObjectGroupPython] G4_DNA_THYMINE  # scripted group (container) (typed FeaturePython)
  Dunit = g/cm3
  Dvalue = 1
  Group = -> [H_element128,C_element138,N_element057,O_element118]
  conduct = 2
  density = 1
  expand = 3
  formula = G4_DNA_THYMINE
  name = G4_DNA_THYMINE
  specific = 4
FEATURE [App::DocumentObjectGroupPython] H_element129  label="H_element : 076"  # scripted group (container) (typed FeaturePython)
  n = 3
  ref = H_element
FEATURE [App::DocumentObjectGroupPython] C_element139  label="C_element : 084"  # scripted group (container) (typed FeaturePython)
  n = 4
  ref = C_element
FEATURE [App::DocumentObjectGroupPython] N_element058  label="N_element : 030"  # scripted group (container) (typed FeaturePython)
  n = 2
  ref = N_element
FEATURE [App::DocumentObjectGroupPython] O_element119  label="O_element : 072"  # scripted group (container) (typed FeaturePython)
  n = 2
  ref = O_element
FEATURE [App::DocumentObjectGroupPython] G4_DNA_URACIL  # scripted group (container) (typed FeaturePython)
  Dunit = g/cm3
  Dvalue = 1
  Group = -> [H_element129,C_element139,N_element058,O_element119]
  conduct = 2
  density = 1
  expand = 3
  formula = G4_DNA_URACIL
  name = G4_DNA_URACIL
  specific = 4
FEATURE [App::DocumentObjectGroupPython] H_element130  label="H_element : 077"  # scripted group (container) (typed FeaturePython)
  n = 10
  ref = H_element
FEATURE [App::DocumentObjectGroupPython] C_element140  label="C_element : 085"  # scripted group (container) (typed FeaturePython)
  n = 10
  ref = C_element
FEATURE [App::DocumentObjectGroupPython] N_element059  label="N_element : 031"  # scripted group (container) (typed FeaturePython)
  n = 5
  ref = N_element
FEATURE [App::DocumentObjectGroupPython] O_element120  label="O_element : 073"  # scripted group (container) (typed FeaturePython)
  n = 4
  ref = O_element
FEATURE [App::DocumentObjectGroupPython] G4_DNA_ADENOSINE  # scripted group (container) (typed FeaturePython)
  Dunit = g/cm3
  Dvalue = 1
  Group = -> [H_element130,C_element140,N_element059,O_element120]
  conduct = 2
  density = 1
  expand = 3
  formula = G4_DNA_ADENOSINE
  name = G4_DNA_ADENOSINE
  specific = 4
FEATURE [App::DocumentObjectGroupPython] H_element131  label="H_element : 078"  # scripted group (container) (typed FeaturePython)
  n = 10
  ref = H_element
FEATURE [App::DocumentObjectGroupPython] C_element141  label="C_element : 086"  # scripted group (container) (typed FeaturePython)
  n = 10
  ref = C_element
FEATURE [App::DocumentObjectGroupPython] N_element060  label="N_element : 032"  # scripted group (container) (typed FeaturePython)
  n = 5
  ref = N_element
FEATURE [App::DocumentObjectGroupPython] O_element121  label="O_element : 074"  # scripted group (container) (typed FeaturePython)
  n = 5
  ref = O_element
FEATURE [App::DocumentObjectGroupPython] G4_DNA_GUANOSINE  # scripted group (container) (typed FeaturePython)
  Dunit = g/cm3
  Dvalue = 1
  Group = -> [H_element131,C_element141,N_element060,O_element121]
  conduct = 2
  density = 1
  expand = 3
  formula = G4_DNA_GUANOSINE
  name = G4_DNA_GUANOSINE
  specific = 4
FEATURE [App::DocumentObjectGroupPython] H_element132  label="H_element : 079"  # scripted group (container) (typed FeaturePython)
  n = 10
  ref = H_element
FEATURE [App::DocumentObjectGroupPython] C_element142  label="C_element : 087"  # scripted group (container) (typed FeaturePython)
  n = 9
  ref = C_element
FEATURE [App::DocumentObjectGroupPython] N_element061  label="N_element : 033"  # scripted group (container) (typed FeaturePython)
  n = 3
  ref = N_element
FEATURE [App::DocumentObjectGroupPython] O_element122  label="O_element : 075"  # scripted group (container) (typed FeaturePython)
  n = 5
  ref = O_element
FEATURE [App::DocumentObjectGroupPython] G4_DNA_CYTIDINE  # scripted group (container) (typed FeaturePython)
  Dunit = g/cm3
  Dvalue = 1
  Group = -> [H_element132,C_element142,N_element061,O_element122]
  conduct = 2
  density = 1
  expand = 3
  formula = G4_DNA_CYTIDINE
  name = G4_DNA_CYTIDINE
  specific = 4
FEATURE [App::DocumentObjectGroupPython] H_element133  label="H_element : 080"  # scripted group (container) (typed FeaturePython)
  n = 9
  ref = H_element
FEATURE [App::DocumentObjectGroupPython] C_element143  label="C_element : 088"  # scripted group (container) (typed FeaturePython)
  n = 9
  ref = C_element
FEATURE [App::DocumentObjectGroupPython] N_element062  label="N_element : 034"  # scripted group (container) (typed FeaturePython)
  n = 2
  ref = N_element
FEATURE [App::DocumentObjectGroupPython] O_element123  label="O_element : 076"  # scripted group (container) (typed FeaturePython)
  n = 6
  ref = O_element
FEATURE [App::DocumentObjectGroupPython] G4_DNA_URIDINE  # scripted group (container) (typed FeaturePython)
  Dunit = g/cm3
  Dvalue = 1
  Group = -> [H_element133,C_element143,N_element062,O_element123]
  conduct = 2
  density = 1
  expand = 3
  formula = G4_DNA_URIDINE
  name = G4_DNA_URIDINE
  specific = 4
FEATURE [App::DocumentObjectGroupPython] H_element134  label="H_element : 081"  # scripted group (container) (typed FeaturePython)
  n = 11
  ref = H_element
FEATURE [App::DocumentObjectGroupPython] C_element144  label="C_element : 089"  # scripted group (container) (typed FeaturePython)
  n = 10
  ref = C_element
FEATURE [App::DocumentObjectGroupPython] N_element063  label="N_element : 035"  # scripted group (container) (typed FeaturePython)
  n = 2
  ref = N_element
FEATURE [App::DocumentObjectGroupPython] O_element124  label="O_element : 077"  # scripted group (container) (typed FeaturePython)
  n = 6
  ref = O_element
FEATURE [App::DocumentObjectGroupPython] G4_DNA_METHYLURIDINE  # scripted group (container) (typed FeaturePython)
  Dunit = g/cm3
  Dvalue = 1
  Group = -> [H_element134,C_element144,N_element063,O_element124]
  conduct = 2
  density = 1
  expand = 3
  formula = G4_DNA_METHYLURIDINE
  name = G4_DNA_METHYLURIDINE
  specific = 4
FEATURE [App::DocumentObjectGroupPython] P_element014  label="P_element : 003"  # scripted group (container) (typed FeaturePython)
  n = 1
  ref = P_element
FEATURE [App::DocumentObjectGroupPython] O_element125  label="O_element : 078"  # scripted group (container) (typed FeaturePython)
  n = 3
  ref = O_element
FEATURE [App::DocumentObjectGroupPython] G4_DNA_MONOPHOSPHATE  # scripted group (container) (typed FeaturePython)
  Dunit = g/cm3
  Dvalue = 1
  Group = -> [P_element014,O_element125]
  conduct = 2
  density = 1
  expand = 3
  formula = G4_DNA_MONOPHOSPHATE
  name = G4_DNA_MONOPHOSPHATE
  specific = 4
FEATURE [App::DocumentObjectGroupPython] H_element135  label="H_element : 082"  # scripted group (container) (typed FeaturePython)
  n = 10
  ref = H_element
FEATURE [App::DocumentObjectGroupPython] C_element145  label="C_element : 090"  # scripted group (container) (typed FeaturePython)
  n = 10
  ref = C_element
FEATURE [App::DocumentObjectGroupPython] N_element064  label="N_element : 036"  # scripted group (container) (typed FeaturePython)
  n = 5
  ref = N_element
FEATURE [App::DocumentObjectGroupPython] O_element126  label="O_element : 079"  # scripted group (container) (typed FeaturePython)
  n = 7
  ref = O_element
FEATURE [App::DocumentObjectGroupPython] P_element015  label="P_element : 004"  # scripted group (container) (typed FeaturePython)
  n = 1
  ref = P_element
FEATURE [App::DocumentObjectGroupPython] G4_DNA_A  # scripted group (container) (typed FeaturePython)
  Dunit = g/cm3
  Dvalue = 1
  Group = -> [H_element135,C_element145,N_element064,O_element126,P_element015]
  conduct = 2
  density = 1
  expand = 3
  formula = G4_DNA_A
  name = G4_DNA_A
  specific = 4
FEATURE [App::DocumentObjectGroupPython] H_element136  label="H_element : 083"  # scripted group (container) (typed FeaturePython)
  n = 10
  ref = H_element
FEATURE [App::DocumentObjectGroupPython] C_element146  label="C_element : 091"  # scripted group (container) (typed FeaturePython)
  n = 10
  ref = C_element
FEATURE [App::DocumentObjectGroupPython] N_element065  label="N_element : 037"  # scripted group (container) (typed FeaturePython)
  n = 5
  ref = N_element
FEATURE [App::DocumentObjectGroupPython] O_element127  label="O_element : 8"  # scripted group (container) (typed FeaturePython)
  n = 8
  ref = O_element
FEATURE [App::DocumentObjectGroupPython] P_element016  label="P_element : 005"  # scripted group (container) (typed FeaturePython)
  n = 1
  ref = P_element
FEATURE [App::DocumentObjectGroupPython] G4_DNA_G  # scripted group (container) (typed FeaturePython)
  Dunit = g/cm3
  Dvalue = 1
  Group = -> [H_element136,C_element146,N_element065,O_element127,P_element016]
  conduct = 2
  density = 1
  expand = 3
  formula = G4_DNA_G
  name = G4_DNA_G
  specific = 4
FEATURE [App::DocumentObjectGroupPython] H_element137  label="H_element : 084"  # scripted group (container) (typed FeaturePython)
  n = 10
  ref = H_element
FEATURE [App::DocumentObjectGroupPython] C_element147  label="C_element : 092"  # scripted group (container) (typed FeaturePython)
  n = 9
  ref = C_element
FEATURE [App::DocumentObjectGroupPython] N_element066  label="N_element : 038"  # scripted group (container) (typed FeaturePython)
  n = 3
  ref = N_element
FEATURE [App::DocumentObjectGroupPython] O_element128  label="O_element : 080"  # scripted group (container) (typed FeaturePython)
  n = 8
  ref = O_element
FEATURE [App::DocumentObjectGroupPython] P_element017  label="P_element : 006"  # scripted group (container) (typed FeaturePython)
  n = 1
  ref = P_element
FEATURE [App::DocumentObjectGroupPython] G4_DNA_C  # scripted group (container) (typed FeaturePython)
  Dunit = g/cm3
  Dvalue = 1
  Group = -> [H_element137,C_element147,N_element066,O_element128,P_element017]
  conduct = 2
  density = 1
  expand = 3
  formula = G4_DNA_C
  name = G4_DNA_C
  specific = 4
FEATURE [App::DocumentObjectGroupPython] H_element138  label="H_element : 085"  # scripted group (container) (typed FeaturePython)
  n = 9
  ref = H_element
FEATURE [App::DocumentObjectGroupPython] C_element148  label="C_element : 093"  # scripted group (container) (typed FeaturePython)
  n = 9
  ref = C_element
FEATURE [App::DocumentObjectGroupPython] N_element067  label="N_element : 039"  # scripted group (container) (typed FeaturePython)
  n = 2
  ref = N_element
FEATURE [App::DocumentObjectGroupPython] O_element129  label="O_element : 9"  # scripted group (container) (typed FeaturePython)
  n = 9
  ref = O_element
FEATURE [App::DocumentObjectGroupPython] P_element018  label="P_element : 007"  # scripted group (container) (typed FeaturePython)
  n = 1
  ref = P_element
FEATURE [App::DocumentObjectGroupPython] G4_DNA_U  # scripted group (container) (typed FeaturePython)
  Dunit = g/cm3
  Dvalue = 1
  Group = -> [H_element138,C_element148,N_element067,O_element129,P_element018]
  conduct = 2
  density = 1
  expand = 3
  formula = G4_DNA_U
  name = G4_DNA_U
  specific = 4
FEATURE [App::DocumentObjectGroupPython] H_element139  label="H_element : 086"  # scripted group (container) (typed FeaturePython)
  n = 11
  ref = H_element
FEATURE [App::DocumentObjectGroupPython] C_element149  label="C_element : 094"  # scripted group (container) (typed FeaturePython)
  n = 10
  ref = C_element
FEATURE [App::DocumentObjectGroupPython] N_element068  label="N_element : 040"  # scripted group (container) (typed FeaturePython)
  n = 2
  ref = N_element
FEATURE [App::DocumentObjectGroupPython] O_element130  label="O_element : 081"  # scripted group (container) (typed FeaturePython)
  n = 9
  ref = O_element
FEATURE [App::DocumentObjectGroupPython] P_element019  label="P_element : 008"  # scripted group (container) (typed FeaturePython)
  n = 1
  ref = P_element
FEATURE [App::DocumentObjectGroupPython] G4_DNA_MU  # scripted group (container) (typed FeaturePython)
  Dunit = g/cm3
  Dvalue = 1
  Group = -> [H_element139,C_element149,N_element068,O_element130,P_element019]
  conduct = 2
  density = 1
  expand = 3
  formula = G4_DNA_MU
  name = G4_DNA_MU
  specific = 4
FEATURE [App::DocumentObjectGroupPython] BioChemical  # scripted group (container) (typed FeaturePython)
  Group = -> [G4_CYTOSINE,G4_THYMINE,G4_URACIL,G4_DNA_ADENINE,G4_DNA_GUANINE,G4_DNA_CYTOSINE,G4_DNA_THYMINE,G4_DNA_URACIL,G4_DNA_ADENOSINE,G4_DNA_GUANOSINE,G4_DNA_CYTIDINE,G4_DNA_URIDINE,G4_DNA_METHYLURIDINE,G4_DNA_MONOPHOSPHATE,G4_DNA_A,G4_DNA_G,G4_DNA_C,G4_DNA_U,G4_DNA_MU]
FEATURE [App::DocumentObjectGroupPython] G4Materials  # scripted group (container) (typed FeaturePython)
  Group = -> [NIST,Element,HEP,Space,BioChemical]
  version = 1
FEATURE [App::DocumentObjectGroupPython] Geant4  # scripted group (container) (typed FeaturePython)
  Group = -> [G4Isotopes,G4Elements,G4Materials]
FEATURE [App::DocumentObjectGroupPython] Materials  # scripted group (container) (typed FeaturePython)
  Group = -> [Geant4]
FEATURE [Part::FeaturePython] GDMLBox_WorldBox  # WARN: FeaturePython — macro-defined, semantics opaque (R4)
  lunit = 2
  material = 5
  x = 100
  y = 100
  z = 100
FEATURE [Part::FeaturePython] GDMLBox_Box  # WARN: FeaturePython — macro-defined, semantics opaque (R4)
  Placement = pos=(30,0,0) rot=(0,0,1;0rad)
  lunit = 2
  material = 0
  x = 10
  y = 10
  z = 10
FEATURE [Part::FeaturePython] GDMLTorus  # WARN: FeaturePython — macro-defined, semantics opaque (R4)
  Placement = pos=(30,0,0) rot=(0,1,0;1.5708rad)
  aunit = deg
  deltaphi = 360
  lunit = 2
  material = 0
  rmax = 2
  rmin = 0
  rtor = 8
  startphi = 0
FEATURE [Part::MultiFuse] Fusion
  Shapes = -> [GDMLBox_Box,GDMLTorus]
FEATURE [Part::FeaturePython] Array  # Draft array (typed FeaturePython)
  AlwaysSyncPlacement = false
  Angle = 180
  ArrayType = 1
  Axis = (0,0,1)
  Base = -> Fusion
  Center = (0,0,0)
  Count = 5
  ExpandArray = false
  Fuse = false
  IntervalAxis = (0,0,0)
  IntervalX = (50,0,0)
  IntervalY = (0,50,0)
  IntervalZ = (0,0,50)
  NumberCircles = 3
  NumberPolar = 5
  NumberX = 2
  NumberY = 2
  NumberZ = 1
  PlacementList = 5 placements: [(0,0,0),(0,0,0),(0,0,0),(0,0,0),(0,0,0)]
  RadialDistance = 50
  ScaleList = (5) [(1,1,1),(1,1,1),(1,1,1),(1,1,1),(1,1,1)]
  Symmetry = 1
  TangentialDistance = 25
FEATURE [App::Part] Part001
  Group = -> [Array]
  Origin = -> Origin004
FEATURE [App::Part] worldVOL
  Group = -> [GDMLBox_WorldBox,Part001]
  Origin = -> Origin
